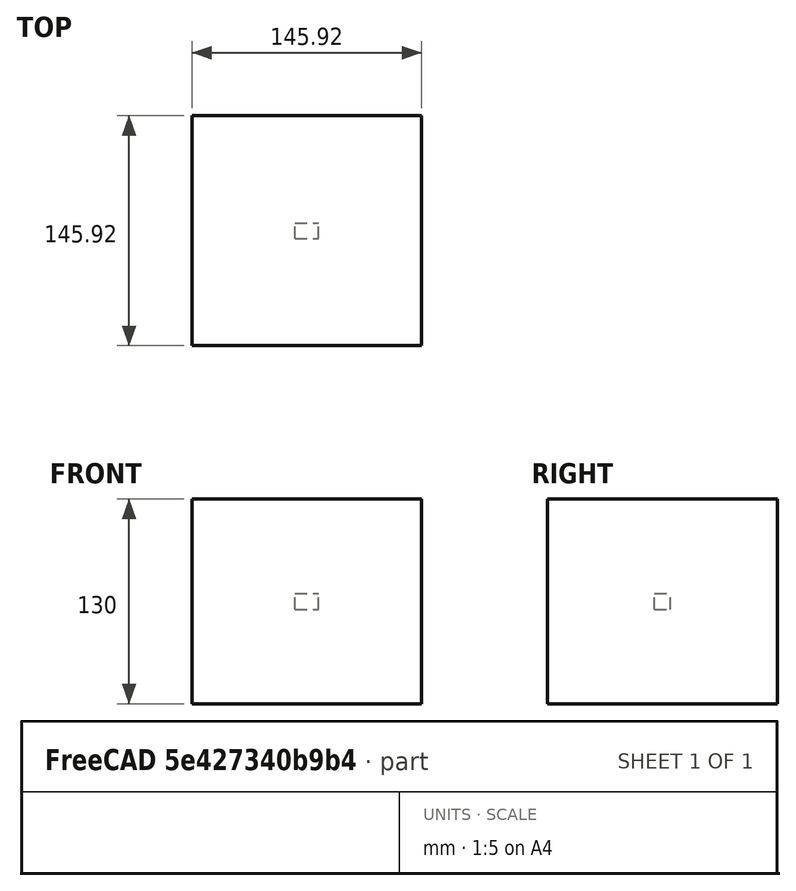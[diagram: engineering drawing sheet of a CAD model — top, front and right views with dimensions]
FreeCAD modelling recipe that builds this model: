
FCSTD DOCUMENT  (FreeCAD 0.20RUnknown)
Label: array-rotation-test
License: All rights reserved
objects: App::DocumentObjectGroupPython×1251, Part::FeaturePython×3, App::Part×3
note: 2 computed .brp shape members not serialized (recipe doc carries the construction recipe); baked Part::Feature solids carry a one-line shape summary decoded from their .brp

FEATURE [App::DocumentObjectGroupPython] HALFPI  # scripted group (container) (typed FeaturePython)
  name = HALFPI
  value = pi/2.
FEATURE [App::DocumentObjectGroupPython] PI  # scripted group (container) (typed FeaturePython)
  name = PI
  value = 1.*pi
FEATURE [App::DocumentObjectGroupPython] TWOPI  # scripted group (container) (typed FeaturePython)
  name = TWOPI
  value = 2.*pi
FEATURE [App::DocumentObjectGroupPython] Constants  # scripted group (container) (typed FeaturePython)
  Group = -> [HALFPI,PI,TWOPI]
FEATURE [App::DocumentObjectGroupPython] Variables  # scripted group (container) (typed FeaturePython)
FEATURE [App::DocumentObjectGroupPython] Quantities  # scripted group (container) (typed FeaturePython)
FEATURE [App::DocumentObjectGroupPython] Isotopes  # scripted group (container) (typed FeaturePython)
FEATURE [App::DocumentObjectGroupPython] Elements  # scripted group (container) (typed FeaturePython)
FEATURE [App::DocumentObjectGroupPython] Matrix  # scripted group (container) (typed FeaturePython)
FEATURE [App::DocumentObjectGroupPython] Surfaces  # scripted group (container) (typed FeaturePython)
FEATURE [App::DocumentObjectGroupPython] Opticals  # scripted group (container) (typed FeaturePython)
  Group = -> [Matrix,Surfaces]
FEATURE [App::DocumentObjectGroupPython] G4Isotopes  # scripted group (container) (typed FeaturePython)
FEATURE [App::DocumentObjectGroupPython] H_element  # scripted group (container) (typed FeaturePython)
  Z = 1
  atom_value = 1.008
  formula = H
  name = H_element
FEATURE [App::DocumentObjectGroupPython] He_element  # scripted group (container) (typed FeaturePython)
  Z = 2
  atom_value = 4.0026
  formula = He
  name = He_element
FEATURE [App::DocumentObjectGroupPython] Li_element  # scripted group (container) (typed FeaturePython)
  Z = 3
  atom_value = 6.94
  formula = Li
  name = Li_element
FEATURE [App::DocumentObjectGroupPython] Be_element  # scripted group (container) (typed FeaturePython)
  Z = 4
  atom_value = 9.01218
  formula = Be
  name = Be_element
FEATURE [App::DocumentObjectGroupPython] B_element  # scripted group (container) (typed FeaturePython)
  Z = 5
  atom_value = 10.81
  formula = B
  name = B_element
FEATURE [App::DocumentObjectGroupPython] C_element  # scripted group (container) (typed FeaturePython)
  Z = 6
  atom_value = 12.011
  formula = C
  name = C_element
FEATURE [App::DocumentObjectGroupPython] N_element  # scripted group (container) (typed FeaturePython)
  Z = 7
  atom_value = 14.007
  formula = N
  name = N_element
FEATURE [App::DocumentObjectGroupPython] O_element  # scripted group (container) (typed FeaturePython)
  Z = 8
  atom_value = 15.999
  formula = O
  name = O_element
FEATURE [App::DocumentObjectGroupPython] F_element  # scripted group (container) (typed FeaturePython)
  Z = 9
  atom_value = 18.9984
  formula = F
  name = F_element
FEATURE [App::DocumentObjectGroupPython] Ne_element  # scripted group (container) (typed FeaturePython)
  Z = 10
  atom_value = 20.1797
  formula = Ne
  name = Ne_element
FEATURE [App::DocumentObjectGroupPython] Na_element  # scripted group (container) (typed FeaturePython)
  Z = 11
  atom_value = 22.9898
  formula = Na
  name = Na_element
FEATURE [App::DocumentObjectGroupPython] Mg_element  # scripted group (container) (typed FeaturePython)
  Z = 12
  atom_value = 24.305
  formula = Mg
  name = Mg_element
FEATURE [App::DocumentObjectGroupPython] Al_element  # scripted group (container) (typed FeaturePython)
  Z = 13
  atom_value = 26.9815
  formula = Al
  name = Al_element
FEATURE [App::DocumentObjectGroupPython] Si_element  # scripted group (container) (typed FeaturePython)
  Z = 14
  atom_value = 28.085
  formula = Si
  name = Si_element
FEATURE [App::DocumentObjectGroupPython] P_element  # scripted group (container) (typed FeaturePython)
  Z = 15
  atom_value = 30.9738
  formula = P
  name = P_element
FEATURE [App::DocumentObjectGroupPython] S_element  # scripted group (container) (typed FeaturePython)
  Z = 16
  atom_value = 32.06
  formula = S
  name = S_element
FEATURE [App::DocumentObjectGroupPython] Cl_element  # scripted group (container) (typed FeaturePython)
  Z = 17
  atom_value = 35.45
  formula = Cl
  name = Cl_element
FEATURE [App::DocumentObjectGroupPython] Ar_element  # scripted group (container) (typed FeaturePython)
  Z = 18
  atom_value = 39.95
  formula = Ar
  name = Ar_element
FEATURE [App::DocumentObjectGroupPython] K_element  # scripted group (container) (typed FeaturePython)
  Z = 19
  atom_value = 39.0983
  formula = K
  name = K_element
FEATURE [App::DocumentObjectGroupPython] Ca_element  # scripted group (container) (typed FeaturePython)
  Z = 20
  atom_value = 40.078
  formula = Ca
  name = Ca_element
FEATURE [App::DocumentObjectGroupPython] Sc_element  # scripted group (container) (typed FeaturePython)
  Z = 21
  atom_value = 44.9559
  formula = Sc
  name = Sc_element
FEATURE [App::DocumentObjectGroupPython] Ti_element  # scripted group (container) (typed FeaturePython)
  Z = 22
  atom_value = 47.867
  formula = Ti
  name = Ti_element
FEATURE [App::DocumentObjectGroupPython] V_element  # scripted group (container) (typed FeaturePython)
  Z = 23
  atom_value = 50.9415
  formula = V
  name = V_element
FEATURE [App::DocumentObjectGroupPython] Cr_element  # scripted group (container) (typed FeaturePython)
  Z = 24
  atom_value = 51.9961
  formula = Cr
  name = Cr_element
FEATURE [App::DocumentObjectGroupPython] Mn_element  # scripted group (container) (typed FeaturePython)
  Z = 25
  atom_value = 54.938
  formula = Mn
  name = Mn_element
FEATURE [App::DocumentObjectGroupPython] Fe_element  # scripted group (container) (typed FeaturePython)
  Z = 26
  atom_value = 55.845
  formula = Fe
  name = Fe_element
FEATURE [App::DocumentObjectGroupPython] Co_element  # scripted group (container) (typed FeaturePython)
  Z = 27
  atom_value = 58.9332
  formula = Co
  name = Co_element
FEATURE [App::DocumentObjectGroupPython] Ni_element  # scripted group (container) (typed FeaturePython)
  Z = 28
  atom_value = 58.6934
  formula = Ni
  name = Ni_element
FEATURE [App::DocumentObjectGroupPython] Cu_element  # scripted group (container) (typed FeaturePython)
  Z = 29
  atom_value = 63.546
  formula = Cu
  name = Cu_element
FEATURE [App::DocumentObjectGroupPython] Zn_element  # scripted group (container) (typed FeaturePython)
  Z = 30
  atom_value = 65.38
  formula = Zn
  name = Zn_element
FEATURE [App::DocumentObjectGroupPython] Ga_element  # scripted group (container) (typed FeaturePython)
  Z = 31
  atom_value = 69.723
  formula = Ga
  name = Ga_element
FEATURE [App::DocumentObjectGroupPython] Ge_element  # scripted group (container) (typed FeaturePython)
  Z = 32
  atom_value = 72.63
  formula = Ge
  name = Ge_element
FEATURE [App::DocumentObjectGroupPython] As_element  # scripted group (container) (typed FeaturePython)
  Z = 33
  atom_value = 74.9216
  formula = As
  name = As_element
FEATURE [App::DocumentObjectGroupPython] Se_element  # scripted group (container) (typed FeaturePython)
  Z = 34
  atom_value = 78.971
  formula = Se
  name = Se_element
FEATURE [App::DocumentObjectGroupPython] Br_element  # scripted group (container) (typed FeaturePython)
  Z = 35
  atom_value = 79.904
  formula = Br
  name = Br_element
FEATURE [App::DocumentObjectGroupPython] Kr_element  # scripted group (container) (typed FeaturePython)
  Z = 36
  atom_value = 83.798
  formula = Kr
  name = Kr_element
FEATURE [App::DocumentObjectGroupPython] Rb_element  # scripted group (container) (typed FeaturePython)
  Z = 37
  atom_value = 85.4678
  formula = Rb
  name = Rb_element
FEATURE [App::DocumentObjectGroupPython] Sr_element  # scripted group (container) (typed FeaturePython)
  Z = 38
  atom_value = 87.62
  formula = Sr
  name = Sr_element
FEATURE [App::DocumentObjectGroupPython] Y_element  # scripted group (container) (typed FeaturePython)
  Z = 39
  atom_value = 88.9058
  formula = Y
  name = Y_element
FEATURE [App::DocumentObjectGroupPython] Zr_element  # scripted group (container) (typed FeaturePython)
  Z = 40
  atom_value = 91.224
  formula = Zr
  name = Zr_element
FEATURE [App::DocumentObjectGroupPython] Nb_element  # scripted group (container) (typed FeaturePython)
  Z = 41
  atom_value = 92.9064
  formula = Nb
  name = Nb_element
FEATURE [App::DocumentObjectGroupPython] Mo_element  # scripted group (container) (typed FeaturePython)
  Z = 42
  atom_value = 95.95
  formula = Mo
  name = Mo_element
FEATURE [App::DocumentObjectGroupPython] Tc_element  # scripted group (container) (typed FeaturePython)
  Z = 43
  atom_value = 97
  formula = Tc
  name = Tc_element
FEATURE [App::DocumentObjectGroupPython] Ru_element  # scripted group (container) (typed FeaturePython)
  Z = 44
  atom_value = 101.07
  formula = Ru
  name = Ru_element
FEATURE [App::DocumentObjectGroupPython] Rh_element  # scripted group (container) (typed FeaturePython)
  Z = 45
  atom_value = 102.905
  formula = Rh
  name = Rh_element
FEATURE [App::DocumentObjectGroupPython] Pd_element  # scripted group (container) (typed FeaturePython)
  Z = 46
  atom_value = 106.42
  formula = Pd
  name = Pd_element
FEATURE [App::DocumentObjectGroupPython] Ag_element  # scripted group (container) (typed FeaturePython)
  Z = 47
  atom_value = 107.868
  formula = Ag
  name = Ag_element
FEATURE [App::DocumentObjectGroupPython] Cd_element  # scripted group (container) (typed FeaturePython)
  Z = 48
  atom_value = 112.414
  formula = Cd
  name = Cd_element
FEATURE [App::DocumentObjectGroupPython] In_element  # scripted group (container) (typed FeaturePython)
  Z = 49
  atom_value = 114.818
  formula = In
  name = In_element
FEATURE [App::DocumentObjectGroupPython] Sn_element  # scripted group (container) (typed FeaturePython)
  Z = 50
  atom_value = 118.71
  formula = Sn
  name = Sn_element
FEATURE [App::DocumentObjectGroupPython] Sb_element  # scripted group (container) (typed FeaturePython)
  Z = 51
  atom_value = 121.76
  formula = Sb
  name = Sb_element
FEATURE [App::DocumentObjectGroupPython] Te_element  # scripted group (container) (typed FeaturePython)
  Z = 52
  atom_value = 127.6
  formula = Te
  name = Te_element
FEATURE [App::DocumentObjectGroupPython] I_element  # scripted group (container) (typed FeaturePython)
  Z = 53
  atom_value = 126.904
  formula = I
  name = I_element
FEATURE [App::DocumentObjectGroupPython] Xe_element  # scripted group (container) (typed FeaturePython)
  Z = 54
  atom_value = 131.293
  formula = Xe
  name = Xe_element
FEATURE [App::DocumentObjectGroupPython] Cs_element  # scripted group (container) (typed FeaturePython)
  Z = 55
  atom_value = 132.905
  formula = Cs
  name = Cs_element
FEATURE [App::DocumentObjectGroupPython] Ba_element  # scripted group (container) (typed FeaturePython)
  Z = 56
  atom_value = 137.327
  formula = Ba
  name = Ba_element
FEATURE [App::DocumentObjectGroupPython] La_element  # scripted group (container) (typed FeaturePython)
  Z = 57
  atom_value = 138.905
  formula = La
  name = La_element
FEATURE [App::DocumentObjectGroupPython] Ce_element  # scripted group (container) (typed FeaturePython)
  Z = 58
  atom_value = 140.116
  formula = Ce
  name = Ce_element
FEATURE [App::DocumentObjectGroupPython] Pr_element  # scripted group (container) (typed FeaturePython)
  Z = 59
  atom_value = 140.908
  formula = Pr
  name = Pr_element
FEATURE [App::DocumentObjectGroupPython] Nd_element  # scripted group (container) (typed FeaturePython)
  Z = 60
  atom_value = 144.242
  formula = Nd
  name = Nd_element
FEATURE [App::DocumentObjectGroupPython] Pm_element  # scripted group (container) (typed FeaturePython)
  Z = 61
  atom_value = 145
  formula = Pm
  name = Pm_element
FEATURE [App::DocumentObjectGroupPython] Sm_element  # scripted group (container) (typed FeaturePython)
  Z = 62
  atom_value = 150.36
  formula = Sm
  name = Sm_element
FEATURE [App::DocumentObjectGroupPython] Eu_element  # scripted group (container) (typed FeaturePython)
  Z = 63
  atom_value = 151.964
  formula = Eu
  name = Eu_element
FEATURE [App::DocumentObjectGroupPython] Gd_element  # scripted group (container) (typed FeaturePython)
  Z = 64
  atom_value = 157.25
  formula = Gd
  name = Gd_element
FEATURE [App::DocumentObjectGroupPython] Tb_element  # scripted group (container) (typed FeaturePython)
  Z = 65
  atom_value = 158.925
  formula = Tb
  name = Tb_element
FEATURE [App::DocumentObjectGroupPython] Dy_element  # scripted group (container) (typed FeaturePython)
  Z = 66
  atom_value = 162.5
  formula = Dy
  name = Dy_element
FEATURE [App::DocumentObjectGroupPython] Ho_element  # scripted group (container) (typed FeaturePython)
  Z = 67
  atom_value = 164.93
  formula = Ho
  name = Ho_element
FEATURE [App::DocumentObjectGroupPython] Er_element  # scripted group (container) (typed FeaturePython)
  Z = 68
  atom_value = 167.259
  formula = Er
  name = Er_element
FEATURE [App::DocumentObjectGroupPython] Tm_element  # scripted group (container) (typed FeaturePython)
  Z = 69
  atom_value = 168.934
  formula = Tm
  name = Tm_element
FEATURE [App::DocumentObjectGroupPython] Yb_element  # scripted group (container) (typed FeaturePython)
  Z = 70
  atom_value = 173.045
  formula = Yb
  name = Yb_element
FEATURE [App::DocumentObjectGroupPython] Lu_element  # scripted group (container) (typed FeaturePython)
  Z = 71
  atom_value = 174.967
  formula = Lu
  name = Lu_element
FEATURE [App::DocumentObjectGroupPython] Hf_element  # scripted group (container) (typed FeaturePython)
  Z = 72
  atom_value = 178.49
  formula = Hf
  name = Hf_element
FEATURE [App::DocumentObjectGroupPython] Ta_element  # scripted group (container) (typed FeaturePython)
  Z = 73
  atom_value = 180.948
  formula = Ta
  name = Ta_element
FEATURE [App::DocumentObjectGroupPython] W_element  # scripted group (container) (typed FeaturePython)
  Z = 74
  atom_value = 183.84
  formula = W
  name = W_element
FEATURE [App::DocumentObjectGroupPython] Re_element  # scripted group (container) (typed FeaturePython)
  Z = 75
  atom_value = 186.207
  formula = Re
  name = Re_element
FEATURE [App::DocumentObjectGroupPython] Os_element  # scripted group (container) (typed FeaturePython)
  Z = 76
  atom_value = 190.23
  formula = Os
  name = Os_element
FEATURE [App::DocumentObjectGroupPython] Ir_element  # scripted group (container) (typed FeaturePython)
  Z = 77
  atom_value = 192.217
  formula = Ir
  name = Ir_element
FEATURE [App::DocumentObjectGroupPython] Pt_element  # scripted group (container) (typed FeaturePython)
  Z = 78
  atom_value = 195.084
  formula = Pt
  name = Pt_element
FEATURE [App::DocumentObjectGroupPython] Au_element  # scripted group (container) (typed FeaturePython)
  Z = 79
  atom_value = 196.967
  formula = Au
  name = Au_element
FEATURE [App::DocumentObjectGroupPython] Hg_element  # scripted group (container) (typed FeaturePython)
  Z = 80
  atom_value = 200.592
  formula = Hg
  name = Hg_element
FEATURE [App::DocumentObjectGroupPython] Tl_element  # scripted group (container) (typed FeaturePython)
  Z = 81
  atom_value = 204.38
  formula = Tl
  name = Tl_element
FEATURE [App::DocumentObjectGroupPython] Pb_element  # scripted group (container) (typed FeaturePython)
  Z = 82
  atom_value = 207.2
  formula = Pb
  name = Pb_element
FEATURE [App::DocumentObjectGroupPython] Bi_element  # scripted group (container) (typed FeaturePython)
  Z = 83
  atom_value = 208.98
  formula = Bi
  name = Bi_element
FEATURE [App::DocumentObjectGroupPython] Po_element  # scripted group (container) (typed FeaturePython)
  Z = 84
  atom_value = 209
  formula = Po
  name = Po_element
FEATURE [App::DocumentObjectGroupPython] At_element  # scripted group (container) (typed FeaturePython)
  Z = 85
  atom_value = 210
  formula = At
  name = At_element
FEATURE [App::DocumentObjectGroupPython] Rn_element  # scripted group (container) (typed FeaturePython)
  Z = 86
  atom_value = 222
  formula = Rn
  name = Rn_element
FEATURE [App::DocumentObjectGroupPython] Fr_element  # scripted group (container) (typed FeaturePython)
  Z = 87
  atom_value = 223
  formula = Fr
  name = Fr_element
FEATURE [App::DocumentObjectGroupPython] Ra_element  # scripted group (container) (typed FeaturePython)
  Z = 88
  atom_value = 226
  formula = Ra
  name = Ra_element
FEATURE [App::DocumentObjectGroupPython] Ac_element  # scripted group (container) (typed FeaturePython)
  Z = 89
  atom_value = 227
  formula = Ac
  name = Ac_element
FEATURE [App::DocumentObjectGroupPython] Th_element  # scripted group (container) (typed FeaturePython)
  Z = 90
  atom_value = 232.038
  formula = Th
  name = Th_element
FEATURE [App::DocumentObjectGroupPython] Pa_element  # scripted group (container) (typed FeaturePython)
  Z = 91
  atom_value = 231.036
  formula = Pa
  name = Pa_element
FEATURE [App::DocumentObjectGroupPython] U_element  # scripted group (container) (typed FeaturePython)
  Z = 92
  atom_value = 238.029
  formula = U
  name = U_element
FEATURE [App::DocumentObjectGroupPython] Np_element  # scripted group (container) (typed FeaturePython)
  Z = 93
  atom_value = 237
  formula = Np
  name = Np_element
FEATURE [App::DocumentObjectGroupPython] Pu_element  # scripted group (container) (typed FeaturePython)
  Z = 94
  atom_value = 244
  formula = Pu
  name = Pu_element
FEATURE [App::DocumentObjectGroupPython] Am_element  # scripted group (container) (typed FeaturePython)
  Z = 95
  atom_value = 243
  formula = Am
  name = Am_element
FEATURE [App::DocumentObjectGroupPython] Cm_element  # scripted group (container) (typed FeaturePython)
  Z = 96
  atom_value = 247
  formula = Cm
  name = Cm_element
FEATURE [App::DocumentObjectGroupPython] Bk_element  # scripted group (container) (typed FeaturePython)
  Z = 97
  atom_value = 247
  formula = Bk
  name = Bk_element
FEATURE [App::DocumentObjectGroupPython] Cf_element  # scripted group (container) (typed FeaturePython)
  Z = 98
  atom_value = 251
  formula = Cf
  name = Cf_element
FEATURE [App::DocumentObjectGroupPython] G4Elements  # scripted group (container) (typed FeaturePython)
  Group = -> [H_element,He_element,Li_element,Be_element,B_element,C_element,N_element,O_element,F_element,Ne_element,Na_element,Mg_element,Al_element,Si_element,P_element,S_element,Cl_element,Ar_element,K_element,Ca_element,Sc_element,Ti_element,V_element,Cr_element,Mn_element,Fe_element,Co_element,Ni_element,Cu_element,Zn_element,Ga_element,Ge_element,As_element,Se_element,Br_element,Kr_element,Rb_element,+61 more]
FEATURE [App::DocumentObjectGroupPython] H_element001  label="H_element : 0.101"  # scripted group (container) (typed FeaturePython)
  n = 0.101327
FEATURE [App::DocumentObjectGroupPython] C_element001  label="C_element : 0.775"  # scripted group (container) (typed FeaturePython)
  n = 0.7755
FEATURE [App::DocumentObjectGroupPython] N_element001  label="N_element : 0.035"  # scripted group (container) (typed FeaturePython)
  n = 0.035057
FEATURE [App::DocumentObjectGroupPython] O_element001  label="O_element : 0.052"  # scripted group (container) (typed FeaturePython)
  n = 0.0523159
FEATURE [App::DocumentObjectGroupPython] F_element001  label="F_element : 0.017"  # scripted group (container) (typed FeaturePython)
  n = 0.017422
FEATURE [App::DocumentObjectGroupPython] Ca_element001  label="Ca_element : 0.018"  # scripted group (container) (typed FeaturePython)
  n = 0.018378
FEATURE [App::DocumentObjectGroupPython] G4_A_150_TISSUE  label="G4_A-150_TISSUE"  # scripted group (container) (typed FeaturePython)
  Dunit = g/cm3
  Dvalue = 1.127
  Group = -> [H_element001,C_element001,N_element001,O_element001,F_element001,Ca_element001]
  conduct = 2
  density = 1
  expand = 3
  formula = G4_A-150_TISSUE
  name = G4_A-150_TISSUE
  specific = 4
FEATURE [App::DocumentObjectGroupPython] C_element002  label="C_element : 3"  # scripted group (container) (typed FeaturePython)
  n = 3
  ref = C_element
FEATURE [App::DocumentObjectGroupPython] H_element002  label="H_element : 6"  # scripted group (container) (typed FeaturePython)
  n = 6
  ref = H_element
FEATURE [App::DocumentObjectGroupPython] O_element002  label="O_element : 1"  # scripted group (container) (typed FeaturePython)
  n = 1
  ref = O_element
FEATURE [App::DocumentObjectGroupPython] G4_ACETONE  # scripted group (container) (typed FeaturePython)
  Dunit = g/cm3
  Dvalue = 0.7899
  Group = -> [C_element002,H_element002,O_element002]
  conduct = 2
  density = 1
  expand = 3
  formula = G4_ACETONE
  name = G4_ACETONE
  specific = 4
FEATURE [App::DocumentObjectGroupPython] C_element003  label="C_element : 2"  # scripted group (container) (typed FeaturePython)
  n = 2
  ref = C_element
FEATURE [App::DocumentObjectGroupPython] H_element003  label="H_element : 2"  # scripted group (container) (typed FeaturePython)
  n = 2
  ref = H_element
FEATURE [App::DocumentObjectGroupPython] G4_ACETYLENE  # scripted group (container) (typed FeaturePython)
  Dunit = g/cm3
  Dvalue = 0.0010967
  Group = -> [C_element003,H_element003]
  conduct = 2
  density = 1
  expand = 3
  formula = G4_ACETYLENE
  name = G4_ACETYLENE
  specific = 4
FEATURE [App::DocumentObjectGroupPython] C_element004  label="C_element : 5"  # scripted group (container) (typed FeaturePython)
  n = 5
  ref = C_element
FEATURE [App::DocumentObjectGroupPython] H_element004  label="H_element : 5"  # scripted group (container) (typed FeaturePython)
  n = 5
  ref = H_element
FEATURE [App::DocumentObjectGroupPython] N_element002  label="N_element : 5"  # scripted group (container) (typed FeaturePython)
  n = 5
  ref = N_element
FEATURE [App::DocumentObjectGroupPython] G4_ADENINE  # scripted group (container) (typed FeaturePython)
  Dunit = g/cm3
  Dvalue = 1.6
  Group = -> [C_element004,H_element004,N_element002]
  conduct = 2
  density = 1
  expand = 3
  formula = G4_ADENINE
  name = G4_ADENINE
  specific = 4
FEATURE [App::DocumentObjectGroupPython] H_element005  label="H_element : 0.114"  # scripted group (container) (typed FeaturePython)
  n = 0.114
FEATURE [App::DocumentObjectGroupPython] C_element005  label="C_element : 0.598"  # scripted group (container) (typed FeaturePython)
  n = 0.598
FEATURE [App::DocumentObjectGroupPython] N_element003  label="N_element : 0.007"  # scripted group (container) (typed FeaturePython)
  n = 0.007
FEATURE [App::DocumentObjectGroupPython] O_element003  label="O_element : 0.278"  # scripted group (container) (typed FeaturePython)
  n = 0.278
FEATURE [App::DocumentObjectGroupPython] Na_element001  label="Na_element : 0.001"  # scripted group (container) (typed FeaturePython)
  n = 0.001
FEATURE [App::DocumentObjectGroupPython] S_element001  label="S_element : 0.001"  # scripted group (container) (typed FeaturePython)
  n = 0.001
FEATURE [App::DocumentObjectGroupPython] Cl_element001  label="Cl_element : 0.001"  # scripted group (container) (typed FeaturePython)
  n = 0.001
FEATURE [App::DocumentObjectGroupPython] G4_ADIPOSE_TISSUE_ICRP  # scripted group (container) (typed FeaturePython)
  Dunit = g/cm3
  Dvalue = 0.95
  Group = -> [H_element005,C_element005,N_element003,O_element003,Na_element001,S_element001,Cl_element001]
  conduct = 2
  density = 1
  expand = 3
  formula = G4_ADIPOSE_TISSUE_ICRP
  name = G4_ADIPOSE_TISSUE_ICRP
  specific = 4
FEATURE [App::DocumentObjectGroupPython] C_element006  label="C_element : 0.000"  # scripted group (container) (typed FeaturePython)
  n = 0.000124
FEATURE [App::DocumentObjectGroupPython] N_element004  label="N_element : 0.755"  # scripted group (container) (typed FeaturePython)
  n = 0.755268
FEATURE [App::DocumentObjectGroupPython] O_element004  label="O_element : 0.232"  # scripted group (container) (typed FeaturePython)
  n = 0.231781
FEATURE [App::DocumentObjectGroupPython] Ar_element001  label="Ar_element : 0.013"  # scripted group (container) (typed FeaturePython)
  n = 0.012827
FEATURE [App::DocumentObjectGroupPython] G4_AIR  # scripted group (container) (typed FeaturePython)
  Dunit = g/cm3
  Dvalue = 0.00120479
  Group = -> [C_element006,N_element004,O_element004,Ar_element001]
  conduct = 2
  density = 1
  expand = 3
  formula = G4_AIR
  name = G4_AIR
  specific = 4
FEATURE [App::DocumentObjectGroupPython] C_element007  label="C_element : 006"  # scripted group (container) (typed FeaturePython)
  n = 3
  ref = C_element
FEATURE [App::DocumentObjectGroupPython] H_element006  label="H_element : 7"  # scripted group (container) (typed FeaturePython)
  n = 7
  ref = H_element
FEATURE [App::DocumentObjectGroupPython] N_element005  label="N_element : 1"  # scripted group (container) (typed FeaturePython)
  n = 1
  ref = N_element
FEATURE [App::DocumentObjectGroupPython] O_element005  label="O_element : 2"  # scripted group (container) (typed FeaturePython)
  n = 2
  ref = O_element
FEATURE [App::DocumentObjectGroupPython] G4_ALANINE  # scripted group (container) (typed FeaturePython)
  Dunit = g/cm3
  Dvalue = 1.42
  Group = -> [C_element007,H_element006,N_element005,O_element005]
  conduct = 2
  density = 1
  expand = 3
  formula = G4_ALANINE
  name = G4_ALANINE
  specific = 4
FEATURE [App::DocumentObjectGroupPython] Al_element001  label="Al_element : 2"  # scripted group (container) (typed FeaturePython)
  n = 2
  ref = Al_element
FEATURE [App::DocumentObjectGroupPython] O_element006  label="O_element : 3"  # scripted group (container) (typed FeaturePython)
  n = 3
  ref = O_element
FEATURE [App::DocumentObjectGroupPython] G4_ALUMINUM_OXIDE  # scripted group (container) (typed FeaturePython)
  Dunit = g/cm3
  Dvalue = 3.97
  Group = -> [Al_element001,O_element006]
  conduct = 2
  density = 1
  expand = 3
  formula = G4_ALUMINUM_OXIDE
  name = G4_ALUMINUM_OXIDE
  specific = 4
FEATURE [App::DocumentObjectGroupPython] H_element007  label="H_element : 0.106"  # scripted group (container) (typed FeaturePython)
  n = 0.10593
FEATURE [App::DocumentObjectGroupPython] C_element008  label="C_element : 0.789"  # scripted group (container) (typed FeaturePython)
  n = 0.788974
FEATURE [App::DocumentObjectGroupPython] O_element007  label="O_element : 0.105"  # scripted group (container) (typed FeaturePython)
  n = 0.105096
FEATURE [App::DocumentObjectGroupPython] G4_AMBER  # scripted group (container) (typed FeaturePython)
  Dunit = g/cm3
  Dvalue = 1.1
  Group = -> [H_element007,C_element008,O_element007]
  conduct = 2
  density = 1
  expand = 3
  formula = G4_AMBER
  name = G4_AMBER
  specific = 4
FEATURE [App::DocumentObjectGroupPython] N_element006  label="N_element : 006"  # scripted group (container) (typed FeaturePython)
  n = 1
  ref = N_element
FEATURE [App::DocumentObjectGroupPython] H_element008  label="H_element : 3"  # scripted group (container) (typed FeaturePython)
  n = 3
  ref = H_element
FEATURE [App::DocumentObjectGroupPython] G4_AMMONIA  # scripted group (container) (typed FeaturePython)
  Dunit = g/cm3
  Dvalue = 0.000826019
  Group = -> [N_element006,H_element008]
  conduct = 2
  density = 1
  expand = 3
  formula = G4_AMMONIA
  name = G4_AMMONIA
  specific = 4
FEATURE [App::DocumentObjectGroupPython] C_element009  label="C_element : 6"  # scripted group (container) (typed FeaturePython)
  n = 6
  ref = C_element
FEATURE [App::DocumentObjectGroupPython] H_element009  label="H_element : 008"  # scripted group (container) (typed FeaturePython)
  n = 7
  ref = H_element
FEATURE [App::DocumentObjectGroupPython] N_element007  label="N_element : 007"  # scripted group (container) (typed FeaturePython)
  n = 1
  ref = N_element
FEATURE [App::DocumentObjectGroupPython] G4_ANILINE  # scripted group (container) (typed FeaturePython)
  Dunit = g/cm3
  Dvalue = 1.0235
  Group = -> [C_element009,H_element009,N_element007]
  conduct = 2
  density = 1
  expand = 3
  formula = G4_ANILINE
  name = G4_ANILINE
  specific = 4
FEATURE [App::DocumentObjectGroupPython] C_element010  label="C_element : 14"  # scripted group (container) (typed FeaturePython)
  n = 14
  ref = C_element
FEATURE [App::DocumentObjectGroupPython] H_element010  label="H_element : 10"  # scripted group (container) (typed FeaturePython)
  n = 10
  ref = H_element
FEATURE [App::DocumentObjectGroupPython] G4_ANTHRACENE  # scripted group (container) (typed FeaturePython)
  Dunit = g/cm3
  Dvalue = 1.283
  Group = -> [C_element010,H_element010]
  conduct = 2
  density = 1
  expand = 3
  formula = G4_ANTHRACENE
  name = G4_ANTHRACENE
  specific = 4
FEATURE [App::DocumentObjectGroupPython] H_element011  label="H_element : 0.065"  # scripted group (container) (typed FeaturePython)
  n = 0.0654709
FEATURE [App::DocumentObjectGroupPython] C_element011  label="C_element : 0.537"  # scripted group (container) (typed FeaturePython)
  n = 0.536944
FEATURE [App::DocumentObjectGroupPython] N_element008  label="N_element : 0.021"  # scripted group (container) (typed FeaturePython)
  n = 0.0215
FEATURE [App::DocumentObjectGroupPython] O_element008  label="O_element : 0.032"  # scripted group (container) (typed FeaturePython)
  n = 0.032085
FEATURE [App::DocumentObjectGroupPython] F_element002  label="F_element : 0.167"  # scripted group (container) (typed FeaturePython)
  n = 0.167411
FEATURE [App::DocumentObjectGroupPython] Ca_element002  label="Ca_element : 0.177"  # scripted group (container) (typed FeaturePython)
  n = 0.176589
FEATURE [App::DocumentObjectGroupPython] G4_B_100_BONE  label="G4_B-100_BONE"  # scripted group (container) (typed FeaturePython)
  Dunit = g/cm3
  Dvalue = 1.45
  Group = -> [H_element011,C_element011,N_element008,O_element008,F_element002,Ca_element002]
  conduct = 2
  density = 1
  expand = 3
  formula = G4_B-100_BONE
  name = G4_B-100_BONE
  specific = 4
FEATURE [App::DocumentObjectGroupPython] H_element012  label="H_element : 0.057"  # scripted group (container) (typed FeaturePython)
  n = 0.057441
FEATURE [App::DocumentObjectGroupPython] C_element012  label="C_element : 0.790"  # scripted group (container) (typed FeaturePython)
  n = 0.774591
FEATURE [App::DocumentObjectGroupPython] O_element009  label="O_element : 0.168"  # scripted group (container) (typed FeaturePython)
  n = 0.167968
FEATURE [App::DocumentObjectGroupPython] G4_BAKELITE  # scripted group (container) (typed FeaturePython)
  Dunit = g/cm3
  Dvalue = 1.25
  Group = -> [H_element012,C_element012,O_element009]
  conduct = 2
  density = 1
  expand = 3
  formula = G4_BAKELITE
  name = G4_BAKELITE
  specific = 4
FEATURE [App::DocumentObjectGroupPython] Ba_element001  label="Ba_element : 1"  # scripted group (container) (typed FeaturePython)
  n = 1
  ref = Ba_element
FEATURE [App::DocumentObjectGroupPython] F_element003  label="F_element : 2"  # scripted group (container) (typed FeaturePython)
  n = 2
  ref = F_element
FEATURE [App::DocumentObjectGroupPython] G4_BARIUM_FLUORIDE  # scripted group (container) (typed FeaturePython)
  Dunit = g/cm3
  Dvalue = 4.89
  Group = -> [Ba_element001,F_element003]
  conduct = 2
  density = 1
  expand = 3
  formula = G4_BARIUM_FLUORIDE
  name = G4_BARIUM_FLUORIDE
  specific = 4
FEATURE [App::DocumentObjectGroupPython] Ba_element002  label="Ba_element : 002"  # scripted group (container) (typed FeaturePython)
  n = 1
  ref = Ba_element
FEATURE [App::DocumentObjectGroupPython] S_element002  label="S_element : 1"  # scripted group (container) (typed FeaturePython)
  n = 1
  ref = S_element
FEATURE [App::DocumentObjectGroupPython] O_element010  label="O_element : 4"  # scripted group (container) (typed FeaturePython)
  n = 4
  ref = O_element
FEATURE [App::DocumentObjectGroupPython] G4_BARIUM_SULFATE  # scripted group (container) (typed FeaturePython)
  Dunit = g/cm3
  Dvalue = 4.5
  Group = -> [Ba_element002,S_element002,O_element010]
  conduct = 2
  density = 1
  expand = 3
  formula = G4_BARIUM_SULFATE
  name = G4_BARIUM_SULFATE
  specific = 4
FEATURE [App::DocumentObjectGroupPython] C_element013  label="C_element : 007"  # scripted group (container) (typed FeaturePython)
  n = 6
  ref = C_element
FEATURE [App::DocumentObjectGroupPython] H_element013  label="H_element : 009"  # scripted group (container) (typed FeaturePython)
  n = 6
  ref = H_element
FEATURE [App::DocumentObjectGroupPython] G4_BENZENE  # scripted group (container) (typed FeaturePython)
  Dunit = g/cm3
  Dvalue = 0.87865
  Group = -> [C_element013,H_element013]
  conduct = 2
  density = 1
  expand = 3
  formula = G4_BENZENE
  name = G4_BENZENE
  specific = 4
FEATURE [App::DocumentObjectGroupPython] Be_element001  label="Be_element : 1"  # scripted group (container) (typed FeaturePython)
  n = 1
  ref = Be_element
FEATURE [App::DocumentObjectGroupPython] O_element011  label="O_element : 005"  # scripted group (container) (typed FeaturePython)
  n = 1
  ref = O_element
FEATURE [App::DocumentObjectGroupPython] G4_BERYLLIUM_OXIDE  # scripted group (container) (typed FeaturePython)
  Dunit = g/cm3
  Dvalue = 3.01
  Group = -> [Be_element001,O_element011]
  conduct = 2
  density = 1
  expand = 3
  formula = G4_BERYLLIUM_OXIDE
  name = G4_BERYLLIUM_OXIDE
  specific = 4
FEATURE [App::DocumentObjectGroupPython] Bi_element001  label="Bi_element : 4"  # scripted group (container) (typed FeaturePython)
  n = 4
  ref = Bi_element
FEATURE [App::DocumentObjectGroupPython] Ge_element001  label="Ge_element : 3"  # scripted group (container) (typed FeaturePython)
  n = 3
  ref = Ge_element
FEATURE [App::DocumentObjectGroupPython] O_element012  label="O_element : 12"  # scripted group (container) (typed FeaturePython)
  n = 12
  ref = O_element
FEATURE [App::DocumentObjectGroupPython] G4_BGO  # scripted group (container) (typed FeaturePython)
  Dunit = g/cm3
  Dvalue = 7.13
  Group = -> [Bi_element001,Ge_element001,O_element012]
  conduct = 2
  density = 1
  expand = 3
  formula = G4_BGO
  name = G4_BGO
  specific = 4
FEATURE [App::DocumentObjectGroupPython] H_element014  label="H_element : 0.102"  # scripted group (container) (typed FeaturePython)
  n = 0.102
FEATURE [App::DocumentObjectGroupPython] C_element014  label="C_element : 0.110"  # scripted group (container) (typed FeaturePython)
  n = 0.11
FEATURE [App::DocumentObjectGroupPython] N_element009  label="N_element : 0.033"  # scripted group (container) (typed FeaturePython)
  n = 0.033
FEATURE [App::DocumentObjectGroupPython] O_element013  label="O_element : 0.745"  # scripted group (container) (typed FeaturePython)
  n = 0.745
FEATURE [App::DocumentObjectGroupPython] Na_element002  label="Na_element : 0.002"  # scripted group (container) (typed FeaturePython)
  n = 0.001
FEATURE [App::DocumentObjectGroupPython] P_element001  label="P_element : 0.001"  # scripted group (container) (typed FeaturePython)
  n = 0.001
FEATURE [App::DocumentObjectGroupPython] S_element003  label="S_element : 0.002"  # scripted group (container) (typed FeaturePython)
  n = 0.002
FEATURE [App::DocumentObjectGroupPython] Cl_element002  label="Cl_element : 0.003"  # scripted group (container) (typed FeaturePython)
  n = 0.003
FEATURE [App::DocumentObjectGroupPython] K_element001  label="K_element : 0.002"  # scripted group (container) (typed FeaturePython)
  n = 0.002
FEATURE [App::DocumentObjectGroupPython] Fe_element001  label="Fe_element : 0.001"  # scripted group (container) (typed FeaturePython)
  n = 0.001
FEATURE [App::DocumentObjectGroupPython] G4_BLOOD_ICRP  # scripted group (container) (typed FeaturePython)
  Dunit = g/cm3
  Dvalue = 1.06
  Group = -> [H_element014,C_element014,N_element009,O_element013,Na_element002,P_element001,S_element003,Cl_element002,K_element001,Fe_element001]
  conduct = 2
  density = 1
  expand = 3
  formula = G4_BLOOD_ICRP
  name = G4_BLOOD_ICRP
  specific = 4
FEATURE [App::DocumentObjectGroupPython] H_element015  label="H_element : 0.064"  # scripted group (container) (typed FeaturePython)
  n = 0.064
FEATURE [App::DocumentObjectGroupPython] C_element015  label="C_element : 0.278"  # scripted group (container) (typed FeaturePython)
  n = 0.278
FEATURE [App::DocumentObjectGroupPython] N_element010  label="N_element : 0.027"  # scripted group (container) (typed FeaturePython)
  n = 0.027
FEATURE [App::DocumentObjectGroupPython] O_element014  label="O_element : 0.410"  # scripted group (container) (typed FeaturePython)
  n = 0.41
FEATURE [App::DocumentObjectGroupPython] Mg_element001  label="Mg_element : 0.002"  # scripted group (container) (typed FeaturePython)
  n = 0.002
FEATURE [App::DocumentObjectGroupPython] P_element002  label="P_element : 0.070"  # scripted group (container) (typed FeaturePython)
  n = 0.07
FEATURE [App::DocumentObjectGroupPython] S_element004  label="S_element : 0.003"  # scripted group (container) (typed FeaturePython)
  n = 0.002
FEATURE [App::DocumentObjectGroupPython] Ca_element003  label="Ca_element : 0.147"  # scripted group (container) (typed FeaturePython)
  n = 0.147
FEATURE [App::DocumentObjectGroupPython] G4_BONE_COMPACT_ICRU  # scripted group (container) (typed FeaturePython)
  Dunit = g/cm3
  Dvalue = 1.85
  Group = -> [H_element015,C_element015,N_element010,O_element014,Mg_element001,P_element002,S_element004,Ca_element003]
  conduct = 2
  density = 1
  expand = 3
  formula = G4_BONE_COMPACT_ICRU
  name = G4_BONE_COMPACT_ICRU
  specific = 4
FEATURE [App::DocumentObjectGroupPython] H_element016  label="H_element : 0.034"  # scripted group (container) (typed FeaturePython)
  n = 0.034
FEATURE [App::DocumentObjectGroupPython] C_element016  label="C_element : 0.155"  # scripted group (container) (typed FeaturePython)
  n = 0.155
FEATURE [App::DocumentObjectGroupPython] N_element011  label="N_element : 0.042"  # scripted group (container) (typed FeaturePython)
  n = 0.042
FEATURE [App::DocumentObjectGroupPython] O_element015  label="O_element : 0.435"  # scripted group (container) (typed FeaturePython)
  n = 0.435
FEATURE [App::DocumentObjectGroupPython] Na_element003  label="Na_element : 0.003"  # scripted group (container) (typed FeaturePython)
  n = 0.001
FEATURE [App::DocumentObjectGroupPython] Mg_element002  label="Mg_element : 0.003"  # scripted group (container) (typed FeaturePython)
  n = 0.002
FEATURE [App::DocumentObjectGroupPython] P_element003  label="P_element : 0.103"  # scripted group (container) (typed FeaturePython)
  n = 0.103
FEATURE [App::DocumentObjectGroupPython] S_element005  label="S_element : 0.004"  # scripted group (container) (typed FeaturePython)
  n = 0.003
FEATURE [App::DocumentObjectGroupPython] Ca_element004  label="Ca_element : 0.225"  # scripted group (container) (typed FeaturePython)
  n = 0.225
FEATURE [App::DocumentObjectGroupPython] G4_BONE_CORTICAL_ICRP  # scripted group (container) (typed FeaturePython)
  Dunit = g/cm3
  Dvalue = 1.92
  Group = -> [H_element016,C_element016,N_element011,O_element015,Na_element003,Mg_element002,P_element003,S_element005,Ca_element004]
  conduct = 2
  density = 1
  expand = 3
  formula = G4_BONE_CORTICAL_ICRP
  name = G4_BONE_CORTICAL_ICRP
  specific = 4
FEATURE [App::DocumentObjectGroupPython] B_element001  label="B_element : 4"  # scripted group (container) (typed FeaturePython)
  n = 4
  ref = B_element
FEATURE [App::DocumentObjectGroupPython] C_element017  label="C_element : 1"  # scripted group (container) (typed FeaturePython)
  n = 1
  ref = C_element
FEATURE [App::DocumentObjectGroupPython] G4_BORON_CARBIDE  # scripted group (container) (typed FeaturePython)
  Dunit = g/cm3
  Dvalue = 2.52
  Group = -> [B_element001,C_element017]
  conduct = 2
  density = 1
  expand = 3
  formula = G4_BORON_CARBIDE
  name = G4_BORON_CARBIDE
  specific = 4
FEATURE [App::DocumentObjectGroupPython] B_element002  label="B_element : 2"  # scripted group (container) (typed FeaturePython)
  n = 2
  ref = B_element
FEATURE [App::DocumentObjectGroupPython] O_element016  label="O_element : 006"  # scripted group (container) (typed FeaturePython)
  n = 3
  ref = O_element
FEATURE [App::DocumentObjectGroupPython] G4_BORON_OXIDE  # scripted group (container) (typed FeaturePython)
  Dunit = g/cm3
  Dvalue = 1.812
  Group = -> [B_element002,O_element016]
  conduct = 2
  density = 1
  expand = 3
  formula = G4_BORON_OXIDE
  name = G4_BORON_OXIDE
  specific = 4
FEATURE [App::DocumentObjectGroupPython] H_element017  label="H_element : 0.107"  # scripted group (container) (typed FeaturePython)
  n = 0.107
FEATURE [App::DocumentObjectGroupPython] C_element018  label="C_element : 0.145"  # scripted group (container) (typed FeaturePython)
  n = 0.145
FEATURE [App::DocumentObjectGroupPython] N_element012  label="N_element : 0.022"  # scripted group (container) (typed FeaturePython)
  n = 0.022
FEATURE [App::DocumentObjectGroupPython] O_element017  label="O_element : 0.712"  # scripted group (container) (typed FeaturePython)
  n = 0.712
FEATURE [App::DocumentObjectGroupPython] Na_element004  label="Na_element : 0.004"  # scripted group (container) (typed FeaturePython)
  n = 0.002
FEATURE [App::DocumentObjectGroupPython] P_element004  label="P_element : 0.004"  # scripted group (container) (typed FeaturePython)
  n = 0.004
FEATURE [App::DocumentObjectGroupPython] S_element006  label="S_element : 0.005"  # scripted group (container) (typed FeaturePython)
  n = 0.002
FEATURE [App::DocumentObjectGroupPython] Cl_element003  label="Cl_element : 0.004"  # scripted group (container) (typed FeaturePython)
  n = 0.003
FEATURE [App::DocumentObjectGroupPython] K_element002  label="K_element : 0.003"  # scripted group (container) (typed FeaturePython)
  n = 0.003
FEATURE [App::DocumentObjectGroupPython] G4_BRAIN_ICRP  # scripted group (container) (typed FeaturePython)
  Dunit = g/cm3
  Dvalue = 1.04
  Group = -> [H_element017,C_element018,N_element012,O_element017,Na_element004,P_element004,S_element006,Cl_element003,K_element002]
  conduct = 2
  density = 1
  expand = 3
  formula = G4_BRAIN_ICRP
  name = G4_BRAIN_ICRP
  specific = 4
FEATURE [App::DocumentObjectGroupPython] C_element019  label="C_element : 4"  # scripted group (container) (typed FeaturePython)
  n = 4
  ref = C_element
FEATURE [App::DocumentObjectGroupPython] H_element018  label="H_element : 010"  # scripted group (container) (typed FeaturePython)
  n = 10
  ref = H_element
FEATURE [App::DocumentObjectGroupPython] G4_BUTANE  # scripted group (container) (typed FeaturePython)
  Dunit = g/cm3
  Dvalue = 0.00249343
  Group = -> [C_element019,H_element018]
  conduct = 2
  density = 1
  expand = 3
  formula = G4_BUTANE
  name = G4_BUTANE
  specific = 4
FEATURE [App::DocumentObjectGroupPython] C_element020  label="C_element : 008"  # scripted group (container) (typed FeaturePython)
  n = 4
  ref = C_element
FEATURE [App::DocumentObjectGroupPython] H_element019  label="H_element : 011"  # scripted group (container) (typed FeaturePython)
  n = 10
  ref = H_element
FEATURE [App::DocumentObjectGroupPython] O_element018  label="O_element : 007"  # scripted group (container) (typed FeaturePython)
  n = 1
  ref = O_element
FEATURE [App::DocumentObjectGroupPython] G4_N_BUTYL_ALCOHOL  label="G4_N-BUTYL_ALCOHOL"  # scripted group (container) (typed FeaturePython)
  Dunit = g/cm3
  Dvalue = 0.8098
  Group = -> [C_element020,H_element019,O_element018]
  conduct = 2
  density = 1
  expand = 3
  formula = G4_N-BUTYL_ALCOHOL
  name = G4_N-BUTYL_ALCOHOL
  specific = 4
FEATURE [App::DocumentObjectGroupPython] H_element020  label="H_element : 0.025"  # scripted group (container) (typed FeaturePython)
  n = 0.02468
FEATURE [App::DocumentObjectGroupPython] C_element021  label="C_element : 0.502"  # scripted group (container) (typed FeaturePython)
  n = 0.501611
FEATURE [App::DocumentObjectGroupPython] O_element019  label="O_element : 0.005"  # scripted group (container) (typed FeaturePython)
  n = 0.004527
FEATURE [App::DocumentObjectGroupPython] F_element004  label="F_element : 0.465"  # scripted group (container) (typed FeaturePython)
  n = 0.465209
FEATURE [App::DocumentObjectGroupPython] Si_element001  label="Si_element : 0.004"  # scripted group (container) (typed FeaturePython)
  n = 0.003973
FEATURE [App::DocumentObjectGroupPython] G4_C_552  label="G4_C-552"  # scripted group (container) (typed FeaturePython)
  Dunit = g/cm3
  Dvalue = 1.76
  Group = -> [H_element020,C_element021,O_element019,F_element004,Si_element001]
  conduct = 2
  density = 1
  expand = 3
  formula = G4_C-552
  name = G4_C-552
  specific = 4
FEATURE [App::DocumentObjectGroupPython] Cd_element001  label="Cd_element : 1"  # scripted group (container) (typed FeaturePython)
  n = 1
  ref = Cd_element
FEATURE [App::DocumentObjectGroupPython] Te_element001  label="Te_element : 1"  # scripted group (container) (typed FeaturePython)
  n = 1
  ref = Te_element
FEATURE [App::DocumentObjectGroupPython] G4_CADMIUM_TELLURIDE  # scripted group (container) (typed FeaturePython)
  Dunit = g/cm3
  Dvalue = 6.2
  Group = -> [Cd_element001,Te_element001]
  conduct = 2
  density = 1
  expand = 3
  formula = G4_CADMIUM_TELLURIDE
  name = G4_CADMIUM_TELLURIDE
  specific = 4
FEATURE [App::DocumentObjectGroupPython] Cd_element002  label="Cd_element : 002"  # scripted group (container) (typed FeaturePython)
  n = 1
  ref = Cd_element
FEATURE [App::DocumentObjectGroupPython] W_element001  label="W_element : 1"  # scripted group (container) (typed FeaturePython)
  n = 1
  ref = W_element
FEATURE [App::DocumentObjectGroupPython] O_element020  label="O_element : 008"  # scripted group (container) (typed FeaturePython)
  n = 4
  ref = O_element
FEATURE [App::DocumentObjectGroupPython] G4_CADMIUM_TUNGSTATE  # scripted group (container) (typed FeaturePython)
  Dunit = g/cm3
  Dvalue = 7.9
  Group = -> [Cd_element002,W_element001,O_element020]
  conduct = 2
  density = 1
  expand = 3
  formula = G4_CADMIUM_TUNGSTATE
  name = G4_CADMIUM_TUNGSTATE
  specific = 4
FEATURE [App::DocumentObjectGroupPython] Ca_element005  label="Ca_element : 1"  # scripted group (container) (typed FeaturePython)
  n = 1
  ref = Ca_element
FEATURE [App::DocumentObjectGroupPython] C_element022  label="C_element : 009"  # scripted group (container) (typed FeaturePython)
  n = 1
  ref = C_element
FEATURE [App::DocumentObjectGroupPython] O_element021  label="O_element : 009"  # scripted group (container) (typed FeaturePython)
  n = 3
  ref = O_element
FEATURE [App::DocumentObjectGroupPython] G4_CALCIUM_CARBONATE  # scripted group (container) (typed FeaturePython)
  Dunit = g/cm3
  Dvalue = 2.8
  Group = -> [Ca_element005,C_element022,O_element021]
  conduct = 2
  density = 1
  expand = 3
  formula = G4_CALCIUM_CARBONATE
  name = G4_CALCIUM_CARBONATE
  specific = 4
FEATURE [App::DocumentObjectGroupPython] Ca_element006  label="Ca_element : 002"  # scripted group (container) (typed FeaturePython)
  n = 1
  ref = Ca_element
FEATURE [App::DocumentObjectGroupPython] F_element005  label="F_element : 003"  # scripted group (container) (typed FeaturePython)
  n = 2
  ref = F_element
FEATURE [App::DocumentObjectGroupPython] G4_CALCIUM_FLUORIDE  # scripted group (container) (typed FeaturePython)
  Dunit = g/cm3
  Dvalue = 3.18
  Group = -> [Ca_element006,F_element005]
  conduct = 2
  density = 1
  expand = 3
  formula = G4_CALCIUM_FLUORIDE
  name = G4_CALCIUM_FLUORIDE
  specific = 4
FEATURE [App::DocumentObjectGroupPython] Ca_element007  label="Ca_element : 003"  # scripted group (container) (typed FeaturePython)
  n = 1
  ref = Ca_element
FEATURE [App::DocumentObjectGroupPython] O_element022  label="O_element : 010"  # scripted group (container) (typed FeaturePython)
  n = 1
  ref = O_element
FEATURE [App::DocumentObjectGroupPython] G4_CALCIUM_OXIDE  # scripted group (container) (typed FeaturePython)
  Dunit = g/cm3
  Dvalue = 3.3
  Group = -> [Ca_element007,O_element022]
  conduct = 2
  density = 1
  expand = 3
  formula = G4_CALCIUM_OXIDE
  name = G4_CALCIUM_OXIDE
  specific = 4
FEATURE [App::DocumentObjectGroupPython] Ca_element008  label="Ca_element : 004"  # scripted group (container) (typed FeaturePython)
  n = 1
  ref = Ca_element
FEATURE [App::DocumentObjectGroupPython] S_element007  label="S_element : 002"  # scripted group (container) (typed FeaturePython)
  n = 1
  ref = S_element
FEATURE [App::DocumentObjectGroupPython] O_element023  label="O_element : 011"  # scripted group (container) (typed FeaturePython)
  n = 4
  ref = O_element
FEATURE [App::DocumentObjectGroupPython] G4_CALCIUM_SULFATE  # scripted group (container) (typed FeaturePython)
  Dunit = g/cm3
  Dvalue = 2.96
  Group = -> [Ca_element008,S_element007,O_element023]
  conduct = 2
  density = 1
  expand = 3
  formula = G4_CALCIUM_SULFATE
  name = G4_CALCIUM_SULFATE
  specific = 4
FEATURE [App::DocumentObjectGroupPython] Ca_element009  label="Ca_element : 005"  # scripted group (container) (typed FeaturePython)
  n = 1
  ref = Ca_element
FEATURE [App::DocumentObjectGroupPython] W_element002  label="W_element : 002"  # scripted group (container) (typed FeaturePython)
  n = 1
  ref = W_element
FEATURE [App::DocumentObjectGroupPython] O_element024  label="O_element : 012"  # scripted group (container) (typed FeaturePython)
  n = 4
  ref = O_element
FEATURE [App::DocumentObjectGroupPython] G4_CALCIUM_TUNGSTATE  # scripted group (container) (typed FeaturePython)
  Dunit = g/cm3
  Dvalue = 6.062
  Group = -> [Ca_element009,W_element002,O_element024]
  conduct = 2
  density = 1
  expand = 3
  formula = G4_CALCIUM_TUNGSTATE
  name = G4_CALCIUM_TUNGSTATE
  specific = 4
FEATURE [App::DocumentObjectGroupPython] C_element023  label="C_element : 010"  # scripted group (container) (typed FeaturePython)
  n = 1
  ref = C_element
FEATURE [App::DocumentObjectGroupPython] O_element025  label="O_element : 013"  # scripted group (container) (typed FeaturePython)
  n = 2
  ref = O_element
FEATURE [App::DocumentObjectGroupPython] G4_CARBON_DIOXIDE  # scripted group (container) (typed FeaturePython)
  Dunit = g/cm3
  Dvalue = 0.00184212
  Group = -> [C_element023,O_element025]
  conduct = 2
  density = 1
  expand = 3
  formula = G4_CARBON_DIOXIDE
  name = G4_CARBON_DIOXIDE
  specific = 4
FEATURE [App::DocumentObjectGroupPython] C_element024  label="C_element : 011"  # scripted group (container) (typed FeaturePython)
  n = 1
  ref = C_element
FEATURE [App::DocumentObjectGroupPython] Cl_element004  label="Cl_element : 4"  # scripted group (container) (typed FeaturePython)
  n = 4
  ref = Cl_element
FEATURE [App::DocumentObjectGroupPython] G4_CARBON_TETRACHLORIDE  # scripted group (container) (typed FeaturePython)
  Dunit = g/cm3
  Dvalue = 1.594
  Group = -> [C_element024,Cl_element004]
  conduct = 2
  density = 1
  expand = 3
  formula = G4_CARBON_TETRACHLORIDE
  name = G4_CARBON_TETRACHLORIDE
  specific = 4
FEATURE [App::DocumentObjectGroupPython] C_element025  label="C_element : 012"  # scripted group (container) (typed FeaturePython)
  n = 6
  ref = C_element
FEATURE [App::DocumentObjectGroupPython] H_element021  label="H_element : 012"  # scripted group (container) (typed FeaturePython)
  n = 10
  ref = H_element
FEATURE [App::DocumentObjectGroupPython] O_element026  label="O_element : 5"  # scripted group (container) (typed FeaturePython)
  n = 5
  ref = O_element
FEATURE [App::DocumentObjectGroupPython] G4_CELLULOSE_CELLOPHANE  # scripted group (container) (typed FeaturePython)
  Dunit = g/cm3
  Dvalue = 1.42
  Group = -> [C_element025,H_element021,O_element026]
  conduct = 2
  density = 1
  expand = 3
  formula = G4_CELLULOSE_CELLOPHANE
  name = G4_CELLULOSE_CELLOPHANE
  specific = 4
FEATURE [App::DocumentObjectGroupPython] H_element022  label="H_element : 0.067"  # scripted group (container) (typed FeaturePython)
  n = 0.067125
FEATURE [App::DocumentObjectGroupPython] C_element026  label="C_element : 0.545"  # scripted group (container) (typed FeaturePython)
  n = 0.545403
FEATURE [App::DocumentObjectGroupPython] O_element027  label="O_element : 0.387"  # scripted group (container) (typed FeaturePython)
  n = 0.387472
FEATURE [App::DocumentObjectGroupPython] G4_CELLULOSE_BUTYRATE  # scripted group (container) (typed FeaturePython)
  Dunit = g/cm3
  Dvalue = 1.2
  Group = -> [H_element022,C_element026,O_element027]
  conduct = 2
  density = 1
  expand = 3
  formula = G4_CELLULOSE_BUTYRATE
  name = G4_CELLULOSE_BUTYRATE
  specific = 4
FEATURE [App::DocumentObjectGroupPython] H_element023  label="H_element : 0.029"  # scripted group (container) (typed FeaturePython)
  n = 0.029216
FEATURE [App::DocumentObjectGroupPython] C_element027  label="C_element : 0.271"  # scripted group (container) (typed FeaturePython)
  n = 0.271296
FEATURE [App::DocumentObjectGroupPython] N_element013  label="N_element : 0.121"  # scripted group (container) (typed FeaturePython)
  n = 0.121276
FEATURE [App::DocumentObjectGroupPython] O_element028  label="O_element : 0.578"  # scripted group (container) (typed FeaturePython)
  n = 0.578212
FEATURE [App::DocumentObjectGroupPython] G4_CELLULOSE_NITRATE  # scripted group (container) (typed FeaturePython)
  Dunit = g/cm3
  Dvalue = 1.49
  Group = -> [H_element023,C_element027,N_element013,O_element028]
  conduct = 2
  density = 1
  expand = 3
  formula = G4_CELLULOSE_NITRATE
  name = G4_CELLULOSE_NITRATE
  specific = 4
FEATURE [App::DocumentObjectGroupPython] H_element024  label="H_element : 0.108"  # scripted group (container) (typed FeaturePython)
  n = 0.107596
FEATURE [App::DocumentObjectGroupPython] N_element014  label="N_element : 0.001"  # scripted group (container) (typed FeaturePython)
  n = 0.0008
FEATURE [App::DocumentObjectGroupPython] O_element029  label="O_element : 0.875"  # scripted group (container) (typed FeaturePython)
  n = 0.874976
FEATURE [App::DocumentObjectGroupPython] S_element008  label="S_element : 0.015"  # scripted group (container) (typed FeaturePython)
  n = 0.014627
FEATURE [App::DocumentObjectGroupPython] Ce_element001  label="Ce_element : 0.002"  # scripted group (container) (typed FeaturePython)
  n = 0.002001
FEATURE [App::DocumentObjectGroupPython] G4_CERIC_SULFATE  # scripted group (container) (typed FeaturePython)
  Dunit = g/cm3
  Dvalue = 1.03
  Group = -> [H_element024,N_element014,O_element029,S_element008,Ce_element001]
  conduct = 2
  density = 1
  expand = 3
  formula = G4_CERIC_SULFATE
  name = G4_CERIC_SULFATE
  specific = 4
FEATURE [App::DocumentObjectGroupPython] Cs_element001  label="Cs_element : 1"  # scripted group (container) (typed FeaturePython)
  n = 1
  ref = Cs_element
FEATURE [App::DocumentObjectGroupPython] F_element006  label="F_element : 1"  # scripted group (container) (typed FeaturePython)
  n = 1
  ref = F_element
FEATURE [App::DocumentObjectGroupPython] G4_CESIUM_FLUORIDE  # scripted group (container) (typed FeaturePython)
  Dunit = g/cm3
  Dvalue = 4.115
  Group = -> [Cs_element001,F_element006]
  conduct = 2
  density = 1
  expand = 3
  formula = G4_CESIUM_FLUORIDE
  name = G4_CESIUM_FLUORIDE
  specific = 4
FEATURE [App::DocumentObjectGroupPython] Cs_element002  label="Cs_element : 002"  # scripted group (container) (typed FeaturePython)
  n = 1
  ref = Cs_element
FEATURE [App::DocumentObjectGroupPython] I_element001  label="I_element : 1"  # scripted group (container) (typed FeaturePython)
  n = 1
  ref = I_element
FEATURE [App::DocumentObjectGroupPython] G4_CESIUM_IODIDE  # scripted group (container) (typed FeaturePython)
  Dunit = g/cm3
  Dvalue = 4.51
  Group = -> [Cs_element002,I_element001]
  conduct = 2
  density = 1
  expand = 3
  formula = G4_CESIUM_IODIDE
  name = G4_CESIUM_IODIDE
  specific = 4
FEATURE [App::DocumentObjectGroupPython] C_element028  label="C_element : 013"  # scripted group (container) (typed FeaturePython)
  n = 6
  ref = C_element
FEATURE [App::DocumentObjectGroupPython] H_element025  label="H_element : 013"  # scripted group (container) (typed FeaturePython)
  n = 5
  ref = H_element
FEATURE [App::DocumentObjectGroupPython] Cl_element005  label="Cl_element : 1"  # scripted group (container) (typed FeaturePython)
  n = 1
  ref = Cl_element
FEATURE [App::DocumentObjectGroupPython] G4_CHLOROBENZENE  # scripted group (container) (typed FeaturePython)
  Dunit = g/cm3
  Dvalue = 1.1058
  Group = -> [C_element028,H_element025,Cl_element005]
  conduct = 2
  density = 1
  expand = 3
  formula = G4_CHLOROBENZENE
  name = G4_CHLOROBENZENE
  specific = 4
FEATURE [App::DocumentObjectGroupPython] C_element029  label="C_element : 014"  # scripted group (container) (typed FeaturePython)
  n = 1
  ref = C_element
FEATURE [App::DocumentObjectGroupPython] H_element026  label="H_element : 1"  # scripted group (container) (typed FeaturePython)
  n = 1
  ref = H_element
FEATURE [App::DocumentObjectGroupPython] Cl_element006  label="Cl_element : 3"  # scripted group (container) (typed FeaturePython)
  n = 3
  ref = Cl_element
FEATURE [App::DocumentObjectGroupPython] G4_CHLOROFORM  # scripted group (container) (typed FeaturePython)
  Dunit = g/cm3
  Dvalue = 1.4832
  Group = -> [C_element029,H_element026,Cl_element006]
  conduct = 2
  density = 1
  expand = 3
  formula = G4_CHLOROFORM
  name = G4_CHLOROFORM
  specific = 4
FEATURE [App::DocumentObjectGroupPython] H_element027  label="H_element : 0.010"  # scripted group (container) (typed FeaturePython)
  n = 0.01
FEATURE [App::DocumentObjectGroupPython] C_element030  label="C_element : 0.001"  # scripted group (container) (typed FeaturePython)
  n = 0.001
FEATURE [App::DocumentObjectGroupPython] O_element030  label="O_element : 0.529"  # scripted group (container) (typed FeaturePython)
  n = 0.529107
FEATURE [App::DocumentObjectGroupPython] Na_element005  label="Na_element : 0.016"  # scripted group (container) (typed FeaturePython)
  n = 0.016
FEATURE [App::DocumentObjectGroupPython] Mg_element003  label="Mg_element : 0.004"  # scripted group (container) (typed FeaturePython)
  n = 0.002
FEATURE [App::DocumentObjectGroupPython] Al_element002  label="Al_element : 0.034"  # scripted group (container) (typed FeaturePython)
  n = 0.033872
FEATURE [App::DocumentObjectGroupPython] Si_element002  label="Si_element : 0.337"  # scripted group (container) (typed FeaturePython)
  n = 0.337021
FEATURE [App::DocumentObjectGroupPython] K_element003  label="K_element : 0.013"  # scripted group (container) (typed FeaturePython)
  n = 0.013
FEATURE [App::DocumentObjectGroupPython] Ca_element010  label="Ca_element : 0.044"  # scripted group (container) (typed FeaturePython)
  n = 0.044
FEATURE [App::DocumentObjectGroupPython] Fe_element002  label="Fe_element : 0.014"  # scripted group (container) (typed FeaturePython)
  n = 0.014
FEATURE [App::DocumentObjectGroupPython] G4_CONCRETE  # scripted group (container) (typed FeaturePython)
  Dunit = g/cm3
  Dvalue = 2.3
  Group = -> [H_element027,C_element030,O_element030,Na_element005,Mg_element003,Al_element002,Si_element002,K_element003,Ca_element010,Fe_element002]
  conduct = 2
  density = 1
  expand = 3
  formula = G4_CONCRETE
  name = G4_CONCRETE
  specific = 4
FEATURE [App::DocumentObjectGroupPython] C_element031  label="C_element : 015"  # scripted group (container) (typed FeaturePython)
  n = 6
  ref = C_element
FEATURE [App::DocumentObjectGroupPython] H_element028  label="H_element : 12"  # scripted group (container) (typed FeaturePython)
  n = 12
  ref = H_element
FEATURE [App::DocumentObjectGroupPython] G4_CYCLOHEXANE  # scripted group (container) (typed FeaturePython)
  Dunit = g/cm3
  Dvalue = 0.779
  Group = -> [C_element031,H_element028]
  conduct = 2
  density = 1
  expand = 3
  formula = G4_CYCLOHEXANE
  name = G4_CYCLOHEXANE
  specific = 4
FEATURE [App::DocumentObjectGroupPython] C_element032  label="C_element : 016"  # scripted group (container) (typed FeaturePython)
  n = 6
  ref = C_element
FEATURE [App::DocumentObjectGroupPython] H_element029  label="H_element : 4"  # scripted group (container) (typed FeaturePython)
  n = 4
  ref = H_element
FEATURE [App::DocumentObjectGroupPython] Cl_element007  label="Cl_element : 2"  # scripted group (container) (typed FeaturePython)
  n = 2
  ref = Cl_element
FEATURE [App::DocumentObjectGroupPython] G4_1_2_DICHLOROBENZENE  label="G4_1.2-DICHLOROBENZENE"  # scripted group (container) (typed FeaturePython)
  Dunit = g/cm3
  Dvalue = 1.3048
  Group = -> [C_element032,H_element029,Cl_element007]
  conduct = 2
  density = 1
  expand = 3
  formula = G4_1.2-DICHLOROBENZENE
  name = G4_1.2-DICHLOROBENZENE
  specific = 4
FEATURE [App::DocumentObjectGroupPython] C_element033  label="C_element : 017"  # scripted group (container) (typed FeaturePython)
  n = 4
  ref = C_element
FEATURE [App::DocumentObjectGroupPython] H_element030  label="H_element : 8"  # scripted group (container) (typed FeaturePython)
  n = 8
  ref = H_element
FEATURE [App::DocumentObjectGroupPython] O_element031  label="O_element : 014"  # scripted group (container) (typed FeaturePython)
  n = 1
  ref = O_element
FEATURE [App::DocumentObjectGroupPython] Cl_element008  label="Cl_element : 005"  # scripted group (container) (typed FeaturePython)
  n = 2
  ref = Cl_element
FEATURE [App::DocumentObjectGroupPython] G4_DICHLORODIETHYL_ETHER  # scripted group (container) (typed FeaturePython)
  Dunit = g/cm3
  Dvalue = 1.2199
  Group = -> [C_element033,H_element030,O_element031,Cl_element008]
  conduct = 2
  density = 1
  expand = 3
  formula = G4_DICHLORODIETHYL_ETHER
  name = G4_DICHLORODIETHYL_ETHER
  specific = 4
FEATURE [App::DocumentObjectGroupPython] C_element034  label="C_element : 018"  # scripted group (container) (typed FeaturePython)
  n = 2
  ref = C_element
FEATURE [App::DocumentObjectGroupPython] H_element031  label="H_element : 014"  # scripted group (container) (typed FeaturePython)
  n = 4
  ref = H_element
FEATURE [App::DocumentObjectGroupPython] Cl_element009  label="Cl_element : 006"  # scripted group (container) (typed FeaturePython)
  n = 2
  ref = Cl_element
FEATURE [App::DocumentObjectGroupPython] G4_1_2_DICHLOROETHANE  label="G4_1.2-DICHLOROETHANE"  # scripted group (container) (typed FeaturePython)
  Dunit = g/cm3
  Dvalue = 1.2351
  Group = -> [C_element034,H_element031,Cl_element009]
  conduct = 2
  density = 1
  expand = 3
  formula = G4_1.2-DICHLOROETHANE
  name = G4_1.2-DICHLOROETHANE
  specific = 4
FEATURE [App::DocumentObjectGroupPython] C_element035  label="C_element : 019"  # scripted group (container) (typed FeaturePython)
  n = 4
  ref = C_element
FEATURE [App::DocumentObjectGroupPython] H_element032  label="H_element : 015"  # scripted group (container) (typed FeaturePython)
  n = 10
  ref = H_element
FEATURE [App::DocumentObjectGroupPython] O_element032  label="O_element : 015"  # scripted group (container) (typed FeaturePython)
  n = 1
  ref = O_element
FEATURE [App::DocumentObjectGroupPython] G4_DIETHYL_ETHER  # scripted group (container) (typed FeaturePython)
  Dunit = g/cm3
  Dvalue = 0.71378
  Group = -> [C_element035,H_element032,O_element032]
  conduct = 2
  density = 1
  expand = 3
  formula = G4_DIETHYL_ETHER
  name = G4_DIETHYL_ETHER
  specific = 4
FEATURE [App::DocumentObjectGroupPython] C_element036  label="C_element : 020"  # scripted group (container) (typed FeaturePython)
  n = 3
  ref = C_element
FEATURE [App::DocumentObjectGroupPython] H_element033  label="H_element : 016"  # scripted group (container) (typed FeaturePython)
  n = 7
  ref = H_element
FEATURE [App::DocumentObjectGroupPython] N_element015  label="N_element : 008"  # scripted group (container) (typed FeaturePython)
  n = 1
  ref = N_element
FEATURE [App::DocumentObjectGroupPython] O_element033  label="O_element : 016"  # scripted group (container) (typed FeaturePython)
  n = 1
  ref = O_element
FEATURE [App::DocumentObjectGroupPython] G4_N_N_DIMETHYL_FORMAMIDE  label="G4_N.N-DIMETHYL_FORMAMIDE"  # scripted group (container) (typed FeaturePython)
  Dunit = g/cm3
  Dvalue = 0.9487
  Group = -> [C_element036,H_element033,N_element015,O_element033]
  conduct = 2
  density = 1
  expand = 3
  formula = G4_N.N-DIMETHYL_FORMAMIDE
  name = G4_N.N-DIMETHYL_FORMAMIDE
  specific = 4
FEATURE [App::DocumentObjectGroupPython] C_element037  label="C_element : 021"  # scripted group (container) (typed FeaturePython)
  n = 2
  ref = C_element
FEATURE [App::DocumentObjectGroupPython] H_element034  label="H_element : 017"  # scripted group (container) (typed FeaturePython)
  n = 6
  ref = H_element
FEATURE [App::DocumentObjectGroupPython] O_element034  label="O_element : 017"  # scripted group (container) (typed FeaturePython)
  n = 1
  ref = O_element
FEATURE [App::DocumentObjectGroupPython] S_element009  label="S_element : 003"  # scripted group (container) (typed FeaturePython)
  n = 1
  ref = S_element
FEATURE [App::DocumentObjectGroupPython] G4_DIMETHYL_SULFOXIDE  # scripted group (container) (typed FeaturePython)
  Dunit = g/cm3
  Dvalue = 1.1014
  Group = -> [C_element037,H_element034,O_element034,S_element009]
  conduct = 2
  density = 1
  expand = 3
  formula = G4_DIMETHYL_SULFOXIDE
  name = G4_DIMETHYL_SULFOXIDE
  specific = 4
FEATURE [App::DocumentObjectGroupPython] C_element038  label="C_element : 022"  # scripted group (container) (typed FeaturePython)
  n = 2
  ref = C_element
FEATURE [App::DocumentObjectGroupPython] H_element035  label="H_element : 018"  # scripted group (container) (typed FeaturePython)
  n = 6
  ref = H_element
FEATURE [App::DocumentObjectGroupPython] G4_ETHANE  # scripted group (container) (typed FeaturePython)
  Dunit = g/cm3
  Dvalue = 0.00125324
  Group = -> [C_element038,H_element035]
  conduct = 2
  density = 1
  expand = 3
  formula = G4_ETHANE
  name = G4_ETHANE
  specific = 4
FEATURE [App::DocumentObjectGroupPython] C_element039  label="C_element : 023"  # scripted group (container) (typed FeaturePython)
  n = 2
  ref = C_element
FEATURE [App::DocumentObjectGroupPython] H_element036  label="H_element : 019"  # scripted group (container) (typed FeaturePython)
  n = 6
  ref = H_element
FEATURE [App::DocumentObjectGroupPython] O_element035  label="O_element : 018"  # scripted group (container) (typed FeaturePython)
  n = 1
  ref = O_element
FEATURE [App::DocumentObjectGroupPython] G4_ETHYL_ALCOHOL  # scripted group (container) (typed FeaturePython)
  Dunit = g/cm3
  Dvalue = 0.7893
  Group = -> [C_element039,H_element036,O_element035]
  conduct = 2
  density = 1
  expand = 3
  formula = G4_ETHYL_ALCOHOL
  name = G4_ETHYL_ALCOHOL
  specific = 4
FEATURE [App::DocumentObjectGroupPython] H_element037  label="H_element : 0.090"  # scripted group (container) (typed FeaturePython)
  n = 0.090027
FEATURE [App::DocumentObjectGroupPython] C_element040  label="C_element : 0.585"  # scripted group (container) (typed FeaturePython)
  n = 0.585182
FEATURE [App::DocumentObjectGroupPython] O_element036  label="O_element : 0.325"  # scripted group (container) (typed FeaturePython)
  n = 0.324791
FEATURE [App::DocumentObjectGroupPython] G4_ETHYL_CELLULOSE  # scripted group (container) (typed FeaturePython)
  Dunit = g/cm3
  Dvalue = 1.13
  Group = -> [H_element037,C_element040,O_element036]
  conduct = 2
  density = 1
  expand = 3
  formula = G4_ETHYL_CELLULOSE
  name = G4_ETHYL_CELLULOSE
  specific = 4
FEATURE [App::DocumentObjectGroupPython] C_element041  label="C_element : 024"  # scripted group (container) (typed FeaturePython)
  n = 2
  ref = C_element
FEATURE [App::DocumentObjectGroupPython] H_element038  label="H_element : 020"  # scripted group (container) (typed FeaturePython)
  n = 4
  ref = H_element
FEATURE [App::DocumentObjectGroupPython] G4_ETHYLENE  # scripted group (container) (typed FeaturePython)
  Dunit = g/cm3
  Dvalue = 0.00117497
  Group = -> [C_element041,H_element038]
  conduct = 2
  density = 1
  expand = 3
  formula = G4_ETHYLENE
  name = G4_ETHYLENE
  specific = 4
FEATURE [App::DocumentObjectGroupPython] H_element039  label="H_element : 0.096"  # scripted group (container) (typed FeaturePython)
  n = 0.096
FEATURE [App::DocumentObjectGroupPython] C_element042  label="C_element : 0.195"  # scripted group (container) (typed FeaturePython)
  n = 0.195
FEATURE [App::DocumentObjectGroupPython] N_element016  label="N_element : 0.057"  # scripted group (container) (typed FeaturePython)
  n = 0.057
FEATURE [App::DocumentObjectGroupPython] O_element037  label="O_element : 0.646"  # scripted group (container) (typed FeaturePython)
  n = 0.646
FEATURE [App::DocumentObjectGroupPython] Na_element006  label="Na_element : 0.017"  # scripted group (container) (typed FeaturePython)
  n = 0.001
FEATURE [App::DocumentObjectGroupPython] P_element005  label="P_element : 0.104"  # scripted group (container) (typed FeaturePython)
  n = 0.001
FEATURE [App::DocumentObjectGroupPython] S_element010  label="S_element : 0.016"  # scripted group (container) (typed FeaturePython)
  n = 0.003
FEATURE [App::DocumentObjectGroupPython] Cl_element010  label="Cl_element : 0.005"  # scripted group (container) (typed FeaturePython)
  n = 0.001
FEATURE [App::DocumentObjectGroupPython] G4_EYE_LENS_ICRP  # scripted group (container) (typed FeaturePython)
  Dunit = g/cm3
  Dvalue = 1.07
  Group = -> [H_element039,C_element042,N_element016,O_element037,Na_element006,P_element005,S_element010,Cl_element010]
  conduct = 2
  density = 1
  expand = 3
  formula = G4_EYE_LENS_ICRP
  name = G4_EYE_LENS_ICRP
  specific = 4
FEATURE [App::DocumentObjectGroupPython] Fe_element003  label="Fe_element : 2"  # scripted group (container) (typed FeaturePython)
  n = 2
  ref = Fe_element
FEATURE [App::DocumentObjectGroupPython] O_element038  label="O_element : 019"  # scripted group (container) (typed FeaturePython)
  n = 3
  ref = O_element
FEATURE [App::DocumentObjectGroupPython] G4_FERRIC_OXIDE  # scripted group (container) (typed FeaturePython)
  Dunit = g/cm3
  Dvalue = 5.2
  Group = -> [Fe_element003,O_element038]
  conduct = 2
  density = 1
  expand = 3
  formula = G4_FERRIC_OXIDE
  name = G4_FERRIC_OXIDE
  specific = 4
FEATURE [App::DocumentObjectGroupPython] Fe_element004  label="Fe_element : 1"  # scripted group (container) (typed FeaturePython)
  n = 1
  ref = Fe_element
FEATURE [App::DocumentObjectGroupPython] B_element003  label="B_element : 1"  # scripted group (container) (typed FeaturePython)
  n = 1
  ref = B_element
FEATURE [App::DocumentObjectGroupPython] G4_FERROBORIDE  # scripted group (container) (typed FeaturePython)
  Dunit = g/cm3
  Dvalue = 7.15
  Group = -> [Fe_element004,B_element003]
  conduct = 2
  density = 1
  expand = 3
  formula = G4_FERROBORIDE
  name = G4_FERROBORIDE
  specific = 4
FEATURE [App::DocumentObjectGroupPython] Fe_element005  label="Fe_element : 003"  # scripted group (container) (typed FeaturePython)
  n = 1
  ref = Fe_element
FEATURE [App::DocumentObjectGroupPython] O_element039  label="O_element : 020"  # scripted group (container) (typed FeaturePython)
  n = 1
  ref = O_element
FEATURE [App::DocumentObjectGroupPython] G4_FERROUS_OXIDE  # scripted group (container) (typed FeaturePython)
  Dunit = g/cm3
  Dvalue = 5.7
  Group = -> [Fe_element005,O_element039]
  conduct = 2
  density = 1
  expand = 3
  formula = G4_FERROUS_OXIDE
  name = G4_FERROUS_OXIDE
  specific = 4
FEATURE [App::DocumentObjectGroupPython] H_element040  label="H_element : 0.115"  # scripted group (container) (typed FeaturePython)
  n = 0.108259
FEATURE [App::DocumentObjectGroupPython] N_element017  label="N_element : 0.000"  # scripted group (container) (typed FeaturePython)
  n = 2.7e-05
FEATURE [App::DocumentObjectGroupPython] O_element040  label="O_element : 0.879"  # scripted group (container) (typed FeaturePython)
  n = 0.878636
FEATURE [App::DocumentObjectGroupPython] Na_element007  label="Na_element : 0.000"  # scripted group (container) (typed FeaturePython)
  n = 2.2e-05
FEATURE [App::DocumentObjectGroupPython] S_element011  label="S_element : 0.013"  # scripted group (container) (typed FeaturePython)
  n = 0.012968
FEATURE [App::DocumentObjectGroupPython] Cl_element011  label="Cl_element : 0.000"  # scripted group (container) (typed FeaturePython)
  n = 3.4e-05
FEATURE [App::DocumentObjectGroupPython] Fe_element006  label="Fe_element : 0.000"  # scripted group (container) (typed FeaturePython)
  n = 5.4e-05
FEATURE [App::DocumentObjectGroupPython] G4_FERROUS_SULFATE  # scripted group (container) (typed FeaturePython)
  Dunit = g/cm3
  Dvalue = 1.024
  Group = -> [H_element040,N_element017,O_element040,Na_element007,S_element011,Cl_element011,Fe_element006]
  conduct = 2
  density = 1
  expand = 3
  formula = G4_FERROUS_SULFATE
  name = G4_FERROUS_SULFATE
  specific = 4
FEATURE [App::DocumentObjectGroupPython] C_element043  label="C_element : 0.099"  # scripted group (container) (typed FeaturePython)
  n = 0.099335
FEATURE [App::DocumentObjectGroupPython] F_element007  label="F_element : 0.314"  # scripted group (container) (typed FeaturePython)
  n = 0.314247
FEATURE [App::DocumentObjectGroupPython] Cl_element012  label="Cl_element : 0.586"  # scripted group (container) (typed FeaturePython)
  n = 0.586418
FEATURE [App::DocumentObjectGroupPython] G4_FREON_12  label="G4_FREON-12"  # scripted group (container) (typed FeaturePython)
  Dunit = g/cm3
  Dvalue = 1.12
  Group = -> [C_element043,F_element007,Cl_element012]
  conduct = 2
  density = 1
  expand = 3
  formula = G4_FREON-12
  name = G4_FREON-12
  specific = 4
FEATURE [App::DocumentObjectGroupPython] C_element044  label="C_element : 0.057"  # scripted group (container) (typed FeaturePython)
  n = 0.057245
FEATURE [App::DocumentObjectGroupPython] F_element008  label="F_element : 0.181"  # scripted group (container) (typed FeaturePython)
  n = 0.181096
FEATURE [App::DocumentObjectGroupPython] Br_element001  label="Br_element : 0.762"  # scripted group (container) (typed FeaturePython)
  n = 0.761659
FEATURE [App::DocumentObjectGroupPython] G4_FREON_12B2  label="G4_FREON-12B2"  # scripted group (container) (typed FeaturePython)
  Dunit = g/cm3
  Dvalue = 1.8
  Group = -> [C_element044,F_element008,Br_element001]
  conduct = 2
  density = 1
  expand = 3
  formula = G4_FREON-12B2
  name = G4_FREON-12B2
  specific = 4
FEATURE [App::DocumentObjectGroupPython] C_element045  label="C_element : 0.115"  # scripted group (container) (typed FeaturePython)
  n = 0.114983
FEATURE [App::DocumentObjectGroupPython] F_element009  label="F_element : 0.546"  # scripted group (container) (typed FeaturePython)
  n = 0.545621
FEATURE [App::DocumentObjectGroupPython] Cl_element013  label="Cl_element : 0.339"  # scripted group (container) (typed FeaturePython)
  n = 0.339396
FEATURE [App::DocumentObjectGroupPython] G4_FREON_13  label="G4_FREON-13"  # scripted group (container) (typed FeaturePython)
  Dunit = g/cm3
  Dvalue = 0.95
  Group = -> [C_element045,F_element009,Cl_element013]
  conduct = 2
  density = 1
  expand = 3
  formula = G4_FREON-13
  name = G4_FREON-13
  specific = 4
FEATURE [App::DocumentObjectGroupPython] C_element046  label="C_element : 025"  # scripted group (container) (typed FeaturePython)
  n = 1
  ref = C_element
FEATURE [App::DocumentObjectGroupPython] F_element010  label="F_element : 3"  # scripted group (container) (typed FeaturePython)
  n = 3
  ref = F_element
FEATURE [App::DocumentObjectGroupPython] Br_element002  label="Br_element : 1"  # scripted group (container) (typed FeaturePython)
  n = 1
  ref = Br_element
FEATURE [App::DocumentObjectGroupPython] G4_FREON_13B1  label="G4_FREON-13B1"  # scripted group (container) (typed FeaturePython)
  Dunit = g/cm3
  Dvalue = 1.5
  Group = -> [C_element046,F_element010,Br_element002]
  conduct = 2
  density = 1
  expand = 3
  formula = G4_FREON-13B1
  name = G4_FREON-13B1
  specific = 4
FEATURE [App::DocumentObjectGroupPython] C_element047  label="C_element : 0.061"  # scripted group (container) (typed FeaturePython)
  n = 0.061309
FEATURE [App::DocumentObjectGroupPython] F_element011  label="F_element : 0.291"  # scripted group (container) (typed FeaturePython)
  n = 0.290924
FEATURE [App::DocumentObjectGroupPython] I_element002  label="I_element : 0.648"  # scripted group (container) (typed FeaturePython)
  n = 0.647767
FEATURE [App::DocumentObjectGroupPython] G4_FREON_13I1  label="G4_FREON-13I1"  # scripted group (container) (typed FeaturePython)
  Dunit = g/cm3
  Dvalue = 1.8
  Group = -> [C_element047,F_element011,I_element002]
  conduct = 2
  density = 1
  expand = 3
  formula = G4_FREON-13I1
  name = G4_FREON-13I1
  specific = 4
FEATURE [App::DocumentObjectGroupPython] Gd_element001  label="Gd_element : 2"  # scripted group (container) (typed FeaturePython)
  n = 2
  ref = Gd_element
FEATURE [App::DocumentObjectGroupPython] O_element041  label="O_element : 021"  # scripted group (container) (typed FeaturePython)
  n = 2
  ref = O_element
FEATURE [App::DocumentObjectGroupPython] S_element012  label="S_element : 004"  # scripted group (container) (typed FeaturePython)
  n = 1
  ref = S_element
FEATURE [App::DocumentObjectGroupPython] G4_GADOLINIUM_OXYSULFIDE  # scripted group (container) (typed FeaturePython)
  Dunit = g/cm3
  Dvalue = 7.44
  Group = -> [Gd_element001,O_element041,S_element012]
  conduct = 2
  density = 1
  expand = 3
  formula = G4_GADOLINIUM_OXYSULFIDE
  name = G4_GADOLINIUM_OXYSULFIDE
  specific = 4
FEATURE [App::DocumentObjectGroupPython] Ga_element001  label="Ga_element : 1"  # scripted group (container) (typed FeaturePython)
  n = 1
  ref = Ga_element
FEATURE [App::DocumentObjectGroupPython] As_element001  label="As_element : 1"  # scripted group (container) (typed FeaturePython)
  n = 1
  ref = As_element
FEATURE [App::DocumentObjectGroupPython] G4_GALLIUM_ARSENIDE  # scripted group (container) (typed FeaturePython)
  Dunit = g/cm3
  Dvalue = 5.31
  Group = -> [Ga_element001,As_element001]
  conduct = 2
  density = 1
  expand = 3
  formula = G4_GALLIUM_ARSENIDE
  name = G4_GALLIUM_ARSENIDE
  specific = 4
FEATURE [App::DocumentObjectGroupPython] H_element041  label="H_element : 0.081"  # scripted group (container) (typed FeaturePython)
  n = 0.08118
FEATURE [App::DocumentObjectGroupPython] C_element048  label="C_element : 0.416"  # scripted group (container) (typed FeaturePython)
  n = 0.41606
FEATURE [App::DocumentObjectGroupPython] N_element018  label="N_element : 0.111"  # scripted group (container) (typed FeaturePython)
  n = 0.11124
FEATURE [App::DocumentObjectGroupPython] O_element042  label="O_element : 0.381"  # scripted group (container) (typed FeaturePython)
  n = 0.38064
FEATURE [App::DocumentObjectGroupPython] S_element013  label="S_element : 0.011"  # scripted group (container) (typed FeaturePython)
  n = 0.01088
FEATURE [App::DocumentObjectGroupPython] G4_GEL_PHOTO_EMULSION  # scripted group (container) (typed FeaturePython)
  Dunit = g/cm3
  Dvalue = 1.2914
  Group = -> [H_element041,C_element048,N_element018,O_element042,S_element013]
  conduct = 2
  density = 1
  expand = 3
  formula = G4_GEL_PHOTO_EMULSION
  name = G4_GEL_PHOTO_EMULSION
  specific = 4
FEATURE [App::DocumentObjectGroupPython] B_element004  label="B_element : 0.040"  # scripted group (container) (typed FeaturePython)
  n = 0.0400639
FEATURE [App::DocumentObjectGroupPython] O_element043  label="O_element : 0.540"  # scripted group (container) (typed FeaturePython)
  n = 0.539561
FEATURE [App::DocumentObjectGroupPython] Na_element008  label="Na_element : 0.028"  # scripted group (container) (typed FeaturePython)
  n = 0.0281909
FEATURE [App::DocumentObjectGroupPython] Al_element003  label="Al_element : 0.012"  # scripted group (container) (typed FeaturePython)
  n = 0.011644
FEATURE [App::DocumentObjectGroupPython] Si_element003  label="Si_element : 0.377"  # scripted group (container) (typed FeaturePython)
  n = 0.377219
FEATURE [App::DocumentObjectGroupPython] K_element004  label="K_element : 0.014"  # scripted group (container) (typed FeaturePython)
  n = 0.00332099
FEATURE [App::DocumentObjectGroupPython] G4_Pyrex_Glass  # scripted group (container) (typed FeaturePython)
  Dunit = g/cm3
  Dvalue = 2.23
  Group = -> [B_element004,O_element043,Na_element008,Al_element003,Si_element003,K_element004]
  conduct = 2
  density = 1
  expand = 3
  formula = G4_Pyrex_Glass
  name = G4_Pyrex_Glass
  specific = 4
FEATURE [App::DocumentObjectGroupPython] O_element044  label="O_element : 0.156"  # scripted group (container) (typed FeaturePython)
  n = 0.156453
FEATURE [App::DocumentObjectGroupPython] Si_element004  label="Si_element : 0.081"  # scripted group (container) (typed FeaturePython)
  n = 0.080866
FEATURE [App::DocumentObjectGroupPython] Ti_element001  label="Ti_element : 0.008"  # scripted group (container) (typed FeaturePython)
  n = 0.008092
FEATURE [App::DocumentObjectGroupPython] As_element002  label="As_element : 0.003"  # scripted group (container) (typed FeaturePython)
  n = 0.002651
FEATURE [App::DocumentObjectGroupPython] Pb_element001  label="Pb_element : 0.752"  # scripted group (container) (typed FeaturePython)
  n = 0.751938
FEATURE [App::DocumentObjectGroupPython] G4_GLASS_LEAD  # scripted group (container) (typed FeaturePython)
  Dunit = g/cm3
  Dvalue = 6.22
  Group = -> [O_element044,Si_element004,Ti_element001,As_element002,Pb_element001]
  conduct = 2
  density = 1
  expand = 3
  formula = G4_GLASS_LEAD
  name = G4_GLASS_LEAD
  specific = 4
FEATURE [App::DocumentObjectGroupPython] O_element045  label="O_element : 0.460"  # scripted group (container) (typed FeaturePython)
  n = 0.4598
FEATURE [App::DocumentObjectGroupPython] Na_element009  label="Na_element : 0.096"  # scripted group (container) (typed FeaturePython)
  n = 0.0964411
FEATURE [App::DocumentObjectGroupPython] Si_element005  label="Si_element : 0.378"  # scripted group (container) (typed FeaturePython)
  n = 0.336553
FEATURE [App::DocumentObjectGroupPython] Ca_element011  label="Ca_element : 0.107"  # scripted group (container) (typed FeaturePython)
  n = 0.107205
FEATURE [App::DocumentObjectGroupPython] G4_GLASS_PLATE  # scripted group (container) (typed FeaturePython)
  Dunit = g/cm3
  Dvalue = 2.4
  Group = -> [O_element045,Na_element009,Si_element005,Ca_element011]
  conduct = 2
  density = 1
  expand = 3
  formula = G4_GLASS_PLATE
  name = G4_GLASS_PLATE
  specific = 4
FEATURE [App::DocumentObjectGroupPython] C_element049  label="C_element : 026"  # scripted group (container) (typed FeaturePython)
  n = 5
  ref = C_element
FEATURE [App::DocumentObjectGroupPython] H_element042  label="H_element : 021"  # scripted group (container) (typed FeaturePython)
  n = 10
  ref = H_element
FEATURE [App::DocumentObjectGroupPython] N_element019  label="N_element : 2"  # scripted group (container) (typed FeaturePython)
  n = 2
  ref = N_element
FEATURE [App::DocumentObjectGroupPython] O_element046  label="O_element : 022"  # scripted group (container) (typed FeaturePython)
  n = 3
  ref = O_element
FEATURE [App::DocumentObjectGroupPython] G4_GLUTAMINE  # scripted group (container) (typed FeaturePython)
  Dunit = g/cm3
  Dvalue = 1.46
  Group = -> [C_element049,H_element042,N_element019,O_element046]
  conduct = 2
  density = 1
  expand = 3
  formula = G4_GLUTAMINE
  name = G4_GLUTAMINE
  specific = 4
FEATURE [App::DocumentObjectGroupPython] C_element050  label="C_element : 027"  # scripted group (container) (typed FeaturePython)
  n = 3
  ref = C_element
FEATURE [App::DocumentObjectGroupPython] H_element043  label="H_element : 022"  # scripted group (container) (typed FeaturePython)
  n = 8
  ref = H_element
FEATURE [App::DocumentObjectGroupPython] O_element047  label="O_element : 023"  # scripted group (container) (typed FeaturePython)
  n = 3
  ref = O_element
FEATURE [App::DocumentObjectGroupPython] G4_GLYCEROL  # scripted group (container) (typed FeaturePython)
  Dunit = g/cm3
  Dvalue = 1.2613
  Group = -> [C_element050,H_element043,O_element047]
  conduct = 2
  density = 1
  expand = 3
  formula = G4_GLYCEROL
  name = G4_GLYCEROL
  specific = 4
FEATURE [App::DocumentObjectGroupPython] C_element051  label="C_element : 028"  # scripted group (container) (typed FeaturePython)
  n = 5
  ref = C_element
FEATURE [App::DocumentObjectGroupPython] H_element044  label="H_element : 023"  # scripted group (container) (typed FeaturePython)
  n = 5
  ref = H_element
FEATURE [App::DocumentObjectGroupPython] N_element020  label="N_element : 009"  # scripted group (container) (typed FeaturePython)
  n = 5
  ref = N_element
FEATURE [App::DocumentObjectGroupPython] O_element048  label="O_element : 024"  # scripted group (container) (typed FeaturePython)
  n = 1
  ref = O_element
FEATURE [App::DocumentObjectGroupPython] G4_GUANINE  # scripted group (container) (typed FeaturePython)
  Dunit = g/cm3
  Dvalue = 2.2
  Group = -> [C_element051,H_element044,N_element020,O_element048]
  conduct = 2
  density = 1
  expand = 3
  formula = G4_GUANINE
  name = G4_GUANINE
  specific = 4
FEATURE [App::DocumentObjectGroupPython] Ca_element012  label="Ca_element : 006"  # scripted group (container) (typed FeaturePython)
  n = 1
  ref = Ca_element
FEATURE [App::DocumentObjectGroupPython] S_element014  label="S_element : 005"  # scripted group (container) (typed FeaturePython)
  n = 1
  ref = S_element
FEATURE [App::DocumentObjectGroupPython] O_element049  label="O_element : 6"  # scripted group (container) (typed FeaturePython)
  n = 6
  ref = O_element
FEATURE [App::DocumentObjectGroupPython] H_element045  label="H_element : 024"  # scripted group (container) (typed FeaturePython)
  n = 4
  ref = H_element
FEATURE [App::DocumentObjectGroupPython] G4_GYPSUM  # scripted group (container) (typed FeaturePython)
  Dunit = g/cm3
  Dvalue = 2.32
  Group = -> [Ca_element012,S_element014,O_element049,H_element045]
  conduct = 2
  density = 1
  expand = 3
  formula = G4_GYPSUM
  name = G4_GYPSUM
  specific = 4
FEATURE [App::DocumentObjectGroupPython] C_element052  label="C_element : 7"  # scripted group (container) (typed FeaturePython)
  n = 7
  ref = C_element
FEATURE [App::DocumentObjectGroupPython] H_element046  label="H_element : 16"  # scripted group (container) (typed FeaturePython)
  n = 16
  ref = H_element
FEATURE [App::DocumentObjectGroupPython] G4_N_HEPTANE  label="G4_N-HEPTANE"  # scripted group (container) (typed FeaturePython)
  Dunit = g/cm3
  Dvalue = 0.68376
  Group = -> [C_element052,H_element046]
  conduct = 2
  density = 1
  expand = 3
  formula = G4_N-HEPTANE
  name = G4_N-HEPTANE
  specific = 4
FEATURE [App::DocumentObjectGroupPython] C_element053  label="C_element : 029"  # scripted group (container) (typed FeaturePython)
  n = 6
  ref = C_element
FEATURE [App::DocumentObjectGroupPython] H_element047  label="H_element : 14"  # scripted group (container) (typed FeaturePython)
  n = 14
  ref = H_element
FEATURE [App::DocumentObjectGroupPython] G4_N_HEXANE  label="G4_N-HEXANE"  # scripted group (container) (typed FeaturePython)
  Dunit = g/cm3
  Dvalue = 0.6603
  Group = -> [C_element053,H_element047]
  conduct = 2
  density = 1
  expand = 3
  formula = G4_N-HEXANE
  name = G4_N-HEXANE
  specific = 4
FEATURE [App::DocumentObjectGroupPython] C_element054  label="C_element : 22"  # scripted group (container) (typed FeaturePython)
  n = 22
  ref = C_element
FEATURE [App::DocumentObjectGroupPython] H_element048  label="H_element : 025"  # scripted group (container) (typed FeaturePython)
  n = 10
  ref = H_element
FEATURE [App::DocumentObjectGroupPython] N_element021  label="N_element : 010"  # scripted group (container) (typed FeaturePython)
  n = 2
  ref = N_element
FEATURE [App::DocumentObjectGroupPython] O_element050  label="O_element : 025"  # scripted group (container) (typed FeaturePython)
  n = 5
  ref = O_element
FEATURE [App::DocumentObjectGroupPython] G4_KAPTON  # scripted group (container) (typed FeaturePython)
  Dunit = g/cm3
  Dvalue = 1.42
  Group = -> [C_element054,H_element048,N_element021,O_element050]
  conduct = 2
  density = 1
  expand = 3
  formula = G4_KAPTON
  name = G4_KAPTON
  specific = 4
FEATURE [App::DocumentObjectGroupPython] La_element001  label="La_element : 1"  # scripted group (container) (typed FeaturePython)
  n = 1
  ref = La_element
FEATURE [App::DocumentObjectGroupPython] Br_element003  label="Br_element : 002"  # scripted group (container) (typed FeaturePython)
  n = 1
  ref = Br_element
FEATURE [App::DocumentObjectGroupPython] O_element051  label="O_element : 026"  # scripted group (container) (typed FeaturePython)
  n = 1
  ref = O_element
FEATURE [App::DocumentObjectGroupPython] G4_LANTHANUM_OXYBROMIDE  # scripted group (container) (typed FeaturePython)
  Dunit = g/cm3
  Dvalue = 6.28
  Group = -> [La_element001,Br_element003,O_element051]
  conduct = 2
  density = 1
  expand = 3
  formula = G4_LANTHANUM_OXYBROMIDE
  name = G4_LANTHANUM_OXYBROMIDE
  specific = 4
FEATURE [App::DocumentObjectGroupPython] La_element002  label="La_element : 2"  # scripted group (container) (typed FeaturePython)
  n = 2
  ref = La_element
FEATURE [App::DocumentObjectGroupPython] O_element052  label="O_element : 027"  # scripted group (container) (typed FeaturePython)
  n = 2
  ref = O_element
FEATURE [App::DocumentObjectGroupPython] S_element015  label="S_element : 006"  # scripted group (container) (typed FeaturePython)
  n = 1
  ref = S_element
FEATURE [App::DocumentObjectGroupPython] G4_LANTHANUM_OXYSULFIDE  # scripted group (container) (typed FeaturePython)
  Dunit = g/cm3
  Dvalue = 5.86
  Group = -> [La_element002,O_element052,S_element015]
  conduct = 2
  density = 1
  expand = 3
  formula = G4_LANTHANUM_OXYSULFIDE
  name = G4_LANTHANUM_OXYSULFIDE
  specific = 4
FEATURE [App::DocumentObjectGroupPython] O_element053  label="O_element : 0.072"  # scripted group (container) (typed FeaturePython)
  n = 0.071682
FEATURE [App::DocumentObjectGroupPython] Pb_element002  label="Pb_element : 0.928"  # scripted group (container) (typed FeaturePython)
  n = 0.928318
FEATURE [App::DocumentObjectGroupPython] G4_LEAD_OXIDE  # scripted group (container) (typed FeaturePython)
  Dunit = g/cm3
  Dvalue = 9.53
  Group = -> [O_element053,Pb_element002]
  conduct = 2
  density = 1
  expand = 3
  formula = G4_LEAD_OXIDE
  name = G4_LEAD_OXIDE
  specific = 4
FEATURE [App::DocumentObjectGroupPython] Li_element001  label="Li_element : 1"  # scripted group (container) (typed FeaturePython)
  n = 1
  ref = Li_element
FEATURE [App::DocumentObjectGroupPython] N_element022  label="N_element : 011"  # scripted group (container) (typed FeaturePython)
  n = 1
  ref = N_element
FEATURE [App::DocumentObjectGroupPython] H_element049  label="H_element : 026"  # scripted group (container) (typed FeaturePython)
  n = 2
  ref = H_element
FEATURE [App::DocumentObjectGroupPython] G4_LITHIUM_AMIDE  # scripted group (container) (typed FeaturePython)
  Dunit = g/cm3
  Dvalue = 1.178
  Group = -> [Li_element001,N_element022,H_element049]
  conduct = 2
  density = 1
  expand = 3
  formula = G4_LITHIUM_AMIDE
  name = G4_LITHIUM_AMIDE
  specific = 4
FEATURE [App::DocumentObjectGroupPython] Li_element002  label="Li_element : 2"  # scripted group (container) (typed FeaturePython)
  n = 2
  ref = Li_element
FEATURE [App::DocumentObjectGroupPython] C_element055  label="C_element : 030"  # scripted group (container) (typed FeaturePython)
  n = 1
  ref = C_element
FEATURE [App::DocumentObjectGroupPython] O_element054  label="O_element : 028"  # scripted group (container) (typed FeaturePython)
  n = 3
  ref = O_element
FEATURE [App::DocumentObjectGroupPython] G4_LITHIUM_CARBONATE  # scripted group (container) (typed FeaturePython)
  Dunit = g/cm3
  Dvalue = 2.11
  Group = -> [Li_element002,C_element055,O_element054]
  conduct = 2
  density = 1
  expand = 3
  formula = G4_LITHIUM_CARBONATE
  name = G4_LITHIUM_CARBONATE
  specific = 4
FEATURE [App::DocumentObjectGroupPython] Li_element003  label="Li_element : 003"  # scripted group (container) (typed FeaturePython)
  n = 1
  ref = Li_element
FEATURE [App::DocumentObjectGroupPython] F_element012  label="F_element : 004"  # scripted group (container) (typed FeaturePython)
  n = 1
  ref = F_element
FEATURE [App::DocumentObjectGroupPython] G4_LITHIUM_FLUORIDE  # scripted group (container) (typed FeaturePython)
  Dunit = g/cm3
  Dvalue = 2.635
  Group = -> [Li_element003,F_element012]
  conduct = 2
  density = 1
  expand = 3
  formula = G4_LITHIUM_FLUORIDE
  name = G4_LITHIUM_FLUORIDE
  specific = 4
FEATURE [App::DocumentObjectGroupPython] Li_element004  label="Li_element : 004"  # scripted group (container) (typed FeaturePython)
  n = 1
  ref = Li_element
FEATURE [App::DocumentObjectGroupPython] H_element050  label="H_element : 027"  # scripted group (container) (typed FeaturePython)
  n = 1
  ref = H_element
FEATURE [App::DocumentObjectGroupPython] G4_LITHIUM_HYDRIDE  # scripted group (container) (typed FeaturePython)
  Dunit = g/cm3
  Dvalue = 0.82
  Group = -> [Li_element004,H_element050]
  conduct = 2
  density = 1
  expand = 3
  formula = G4_LITHIUM_HYDRIDE
  name = G4_LITHIUM_HYDRIDE
  specific = 4
FEATURE [App::DocumentObjectGroupPython] Li_element005  label="Li_element : 005"  # scripted group (container) (typed FeaturePython)
  n = 1
  ref = Li_element
FEATURE [App::DocumentObjectGroupPython] I_element003  label="I_element : 002"  # scripted group (container) (typed FeaturePython)
  n = 1
  ref = I_element
FEATURE [App::DocumentObjectGroupPython] G4_LITHIUM_IODIDE  # scripted group (container) (typed FeaturePython)
  Dunit = g/cm3
  Dvalue = 3.494
  Group = -> [Li_element005,I_element003]
  conduct = 2
  density = 1
  expand = 3
  formula = G4_LITHIUM_IODIDE
  name = G4_LITHIUM_IODIDE
  specific = 4
FEATURE [App::DocumentObjectGroupPython] Li_element006  label="Li_element : 006"  # scripted group (container) (typed FeaturePython)
  n = 2
  ref = Li_element
FEATURE [App::DocumentObjectGroupPython] O_element055  label="O_element : 029"  # scripted group (container) (typed FeaturePython)
  n = 1
  ref = O_element
FEATURE [App::DocumentObjectGroupPython] G4_LITHIUM_OXIDE  # scripted group (container) (typed FeaturePython)
  Dunit = g/cm3
  Dvalue = 2.013
  Group = -> [Li_element006,O_element055]
  conduct = 2
  density = 1
  expand = 3
  formula = G4_LITHIUM_OXIDE
  name = G4_LITHIUM_OXIDE
  specific = 4
FEATURE [App::DocumentObjectGroupPython] Li_element007  label="Li_element : 007"  # scripted group (container) (typed FeaturePython)
  n = 2
  ref = Li_element
FEATURE [App::DocumentObjectGroupPython] B_element005  label="B_element : 005"  # scripted group (container) (typed FeaturePython)
  n = 4
  ref = B_element
FEATURE [App::DocumentObjectGroupPython] O_element056  label="O_element : 7"  # scripted group (container) (typed FeaturePython)
  n = 7
  ref = O_element
FEATURE [App::DocumentObjectGroupPython] G4_LITHIUM_TETRABORATE  # scripted group (container) (typed FeaturePython)
  Dunit = g/cm3
  Dvalue = 2.44
  Group = -> [Li_element007,B_element005,O_element056]
  conduct = 2
  density = 1
  expand = 3
  formula = G4_LITHIUM_TETRABORATE
  name = G4_LITHIUM_TETRABORATE
  specific = 4
FEATURE [App::DocumentObjectGroupPython] H_element051  label="H_element : 0.105"  # scripted group (container) (typed FeaturePython)
  n = 0.105
FEATURE [App::DocumentObjectGroupPython] C_element056  label="C_element : 0.083"  # scripted group (container) (typed FeaturePython)
  n = 0.083
FEATURE [App::DocumentObjectGroupPython] N_element023  label="N_element : 0.023"  # scripted group (container) (typed FeaturePython)
  n = 0.023
FEATURE [App::DocumentObjectGroupPython] O_element057  label="O_element : 0.779"  # scripted group (container) (typed FeaturePython)
  n = 0.779
FEATURE [App::DocumentObjectGroupPython] Na_element010  label="Na_element : 0.097"  # scripted group (container) (typed FeaturePython)
  n = 0.002
FEATURE [App::DocumentObjectGroupPython] P_element006  label="P_element : 0.105"  # scripted group (container) (typed FeaturePython)
  n = 0.001
FEATURE [App::DocumentObjectGroupPython] S_element016  label="S_element : 0.017"  # scripted group (container) (typed FeaturePython)
  n = 0.002
FEATURE [App::DocumentObjectGroupPython] Cl_element014  label="Cl_element : 0.587"  # scripted group (container) (typed FeaturePython)
  n = 0.003
FEATURE [App::DocumentObjectGroupPython] K_element005  label="K_element : 0.015"  # scripted group (container) (typed FeaturePython)
  n = 0.002
FEATURE [App::DocumentObjectGroupPython] G4_LUNG_ICRP  # scripted group (container) (typed FeaturePython)
  Dunit = g/cm3
  Dvalue = 1.04
  Group = -> [H_element051,C_element056,N_element023,O_element057,Na_element010,P_element006,S_element016,Cl_element014,K_element005]
  conduct = 2
  density = 1
  expand = 3
  formula = G4_LUNG_ICRP
  name = G4_LUNG_ICRP
  specific = 4
FEATURE [App::DocumentObjectGroupPython] H_element052  label="H_element : 0.116"  # scripted group (container) (typed FeaturePython)
  n = 0.114318
FEATURE [App::DocumentObjectGroupPython] C_element057  label="C_element : 0.656"  # scripted group (container) (typed FeaturePython)
  n = 0.655824
FEATURE [App::DocumentObjectGroupPython] O_element058  label="O_element : 0.092"  # scripted group (container) (typed FeaturePython)
  n = 0.0921831
FEATURE [App::DocumentObjectGroupPython] Mg_element004  label="Mg_element : 0.135"  # scripted group (container) (typed FeaturePython)
  n = 0.134792
FEATURE [App::DocumentObjectGroupPython] Ca_element013  label="Ca_element : 0.003"  # scripted group (container) (typed FeaturePython)
  n = 0.002883
FEATURE [App::DocumentObjectGroupPython] G4_M3_WAX  # scripted group (container) (typed FeaturePython)
  Dunit = g/cm3
  Dvalue = 1.05
  Group = -> [H_element052,C_element057,O_element058,Mg_element004,Ca_element013]
  conduct = 2
  density = 1
  expand = 3
  formula = G4_M3_WAX
  name = G4_M3_WAX
  specific = 4
FEATURE [App::DocumentObjectGroupPython] Mg_element005  label="Mg_element : 1"  # scripted group (container) (typed FeaturePython)
  n = 1
  ref = Mg_element
FEATURE [App::DocumentObjectGroupPython] C_element058  label="C_element : 031"  # scripted group (container) (typed FeaturePython)
  n = 1
  ref = C_element
FEATURE [App::DocumentObjectGroupPython] O_element059  label="O_element : 030"  # scripted group (container) (typed FeaturePython)
  n = 3
  ref = O_element
FEATURE [App::DocumentObjectGroupPython] G4_MAGNESIUM_CARBONATE  # scripted group (container) (typed FeaturePython)
  Dunit = g/cm3
  Dvalue = 2.958
  Group = -> [Mg_element005,C_element058,O_element059]
  conduct = 2
  density = 1
  expand = 3
  formula = G4_MAGNESIUM_CARBONATE
  name = G4_MAGNESIUM_CARBONATE
  specific = 4
FEATURE [App::DocumentObjectGroupPython] Mg_element006  label="Mg_element : 002"  # scripted group (container) (typed FeaturePython)
  n = 1
  ref = Mg_element
FEATURE [App::DocumentObjectGroupPython] F_element013  label="F_element : 005"  # scripted group (container) (typed FeaturePython)
  n = 2
  ref = F_element
FEATURE [App::DocumentObjectGroupPython] G4_MAGNESIUM_FLUORIDE  # scripted group (container) (typed FeaturePython)
  Dunit = g/cm3
  Dvalue = 3
  Group = -> [Mg_element006,F_element013]
  conduct = 2
  density = 1
  expand = 3
  formula = G4_MAGNESIUM_FLUORIDE
  name = G4_MAGNESIUM_FLUORIDE
  specific = 4
FEATURE [App::DocumentObjectGroupPython] Mg_element007  label="Mg_element : 003"  # scripted group (container) (typed FeaturePython)
  n = 1
  ref = Mg_element
FEATURE [App::DocumentObjectGroupPython] O_element060  label="O_element : 031"  # scripted group (container) (typed FeaturePython)
  n = 1
  ref = O_element
FEATURE [App::DocumentObjectGroupPython] G4_MAGNESIUM_OXIDE  # scripted group (container) (typed FeaturePython)
  Dunit = g/cm3
  Dvalue = 3.58
  Group = -> [Mg_element007,O_element060]
  conduct = 2
  density = 1
  expand = 3
  formula = G4_MAGNESIUM_OXIDE
  name = G4_MAGNESIUM_OXIDE
  specific = 4
FEATURE [App::DocumentObjectGroupPython] Mg_element008  label="Mg_element : 004"  # scripted group (container) (typed FeaturePython)
  n = 1
  ref = Mg_element
FEATURE [App::DocumentObjectGroupPython] B_element006  label="B_element : 006"  # scripted group (container) (typed FeaturePython)
  n = 4
  ref = B_element
FEATURE [App::DocumentObjectGroupPython] O_element061  label="O_element : 032"  # scripted group (container) (typed FeaturePython)
  n = 7
  ref = O_element
FEATURE [App::DocumentObjectGroupPython] G4_MAGNESIUM_TETRABORATE  # scripted group (container) (typed FeaturePython)
  Dunit = g/cm3
  Dvalue = 2.53
  Group = -> [Mg_element008,B_element006,O_element061]
  conduct = 2
  density = 1
  expand = 3
  formula = G4_MAGNESIUM_TETRABORATE
  name = G4_MAGNESIUM_TETRABORATE
  specific = 4
FEATURE [App::DocumentObjectGroupPython] Hg_element001  label="Hg_element : 1"  # scripted group (container) (typed FeaturePython)
  n = 1
  ref = Hg_element
FEATURE [App::DocumentObjectGroupPython] I_element004  label="I_element : 2"  # scripted group (container) (typed FeaturePython)
  n = 2
  ref = I_element
FEATURE [App::DocumentObjectGroupPython] G4_MERCURIC_IODIDE  # scripted group (container) (typed FeaturePython)
  Dunit = g/cm3
  Dvalue = 6.36
  Group = -> [Hg_element001,I_element004]
  conduct = 2
  density = 1
  expand = 3
  formula = G4_MERCURIC_IODIDE
  name = G4_MERCURIC_IODIDE
  specific = 4
FEATURE [App::DocumentObjectGroupPython] C_element059  label="C_element : 032"  # scripted group (container) (typed FeaturePython)
  n = 1
  ref = C_element
FEATURE [App::DocumentObjectGroupPython] H_element053  label="H_element : 028"  # scripted group (container) (typed FeaturePython)
  n = 4
  ref = H_element
FEATURE [App::DocumentObjectGroupPython] G4_METHANE  # scripted group (container) (typed FeaturePython)
  Dunit = g/cm3
  Dvalue = 0.000667151
  Group = -> [C_element059,H_element053]
  conduct = 2
  density = 1
  expand = 3
  formula = G4_METHANE
  name = G4_METHANE
  specific = 4
FEATURE [App::DocumentObjectGroupPython] C_element060  label="C_element : 033"  # scripted group (container) (typed FeaturePython)
  n = 1
  ref = C_element
FEATURE [App::DocumentObjectGroupPython] H_element054  label="H_element : 029"  # scripted group (container) (typed FeaturePython)
  n = 4
  ref = H_element
FEATURE [App::DocumentObjectGroupPython] O_element062  label="O_element : 033"  # scripted group (container) (typed FeaturePython)
  n = 1
  ref = O_element
FEATURE [App::DocumentObjectGroupPython] G4_METHANOL  # scripted group (container) (typed FeaturePython)
  Dunit = g/cm3
  Dvalue = 0.7914
  Group = -> [C_element060,H_element054,O_element062]
  conduct = 2
  density = 1
  expand = 3
  formula = G4_METHANOL
  name = G4_METHANOL
  specific = 4
FEATURE [App::DocumentObjectGroupPython] H_element055  label="H_element : 0.134"  # scripted group (container) (typed FeaturePython)
  n = 0.13404
FEATURE [App::DocumentObjectGroupPython] C_element061  label="C_element : 0.778"  # scripted group (container) (typed FeaturePython)
  n = 0.77796
FEATURE [App::DocumentObjectGroupPython] O_element063  label="O_element : 0.035"  # scripted group (container) (typed FeaturePython)
  n = 0.03502
FEATURE [App::DocumentObjectGroupPython] Mg_element009  label="Mg_element : 0.039"  # scripted group (container) (typed FeaturePython)
  n = 0.038594
FEATURE [App::DocumentObjectGroupPython] Ti_element002  label="Ti_element : 0.014"  # scripted group (container) (typed FeaturePython)
  n = 0.014386
FEATURE [App::DocumentObjectGroupPython] G4_MIX_D_WAX  # scripted group (container) (typed FeaturePython)
  Dunit = g/cm3
  Dvalue = 0.99
  Group = -> [H_element055,C_element061,O_element063,Mg_element009,Ti_element002]
  conduct = 2
  density = 1
  expand = 3
  formula = G4_MIX_D_WAX
  name = G4_MIX_D_WAX
  specific = 4
FEATURE [App::DocumentObjectGroupPython] H_element056  label="H_element : 0.135"  # scripted group (container) (typed FeaturePython)
  n = 0.081192
FEATURE [App::DocumentObjectGroupPython] C_element062  label="C_element : 0.583"  # scripted group (container) (typed FeaturePython)
  n = 0.583442
FEATURE [App::DocumentObjectGroupPython] N_element024  label="N_element : 0.018"  # scripted group (container) (typed FeaturePython)
  n = 0.017798
FEATURE [App::DocumentObjectGroupPython] O_element064  label="O_element : 0.186"  # scripted group (container) (typed FeaturePython)
  n = 0.186381
FEATURE [App::DocumentObjectGroupPython] Mg_element010  label="Mg_element : 0.130"  # scripted group (container) (typed FeaturePython)
  n = 0.130287
FEATURE [App::DocumentObjectGroupPython] Cl_element015  label="Cl_element : 0.588"  # scripted group (container) (typed FeaturePython)
  n = 0.0009
FEATURE [App::DocumentObjectGroupPython] G4_MS20_TISSUE  # scripted group (container) (typed FeaturePython)
  Dunit = g/cm3
  Dvalue = 1
  Group = -> [H_element056,C_element062,N_element024,O_element064,Mg_element010,Cl_element015]
  conduct = 2
  density = 1
  expand = 3
  formula = G4_MS20_TISSUE
  name = G4_MS20_TISSUE
  specific = 4
FEATURE [App::DocumentObjectGroupPython] H_element057  label="H_element : 0.136"  # scripted group (container) (typed FeaturePython)
  n = 0.102
FEATURE [App::DocumentObjectGroupPython] C_element063  label="C_element : 0.143"  # scripted group (container) (typed FeaturePython)
  n = 0.143
FEATURE [App::DocumentObjectGroupPython] N_element025  label="N_element : 0.034"  # scripted group (container) (typed FeaturePython)
  n = 0.034
FEATURE [App::DocumentObjectGroupPython] O_element065  label="O_element : 0.710"  # scripted group (container) (typed FeaturePython)
  n = 0.71
FEATURE [App::DocumentObjectGroupPython] Na_element011  label="Na_element : 0.098"  # scripted group (container) (typed FeaturePython)
  n = 0.001
FEATURE [App::DocumentObjectGroupPython] P_element007  label="P_element : 0.002"  # scripted group (container) (typed FeaturePython)
  n = 0.002
FEATURE [App::DocumentObjectGroupPython] S_element017  label="S_element : 0.018"  # scripted group (container) (typed FeaturePython)
  n = 0.003
FEATURE [App::DocumentObjectGroupPython] Cl_element016  label="Cl_element : 0.589"  # scripted group (container) (typed FeaturePython)
  n = 0.001
FEATURE [App::DocumentObjectGroupPython] K_element006  label="K_element : 0.004"  # scripted group (container) (typed FeaturePython)
  n = 0.004
FEATURE [App::DocumentObjectGroupPython] G4_MUSCLE_SKELETAL_ICRP  # scripted group (container) (typed FeaturePython)
  Dunit = g/cm3
  Dvalue = 1.05
  Group = -> [H_element057,C_element063,N_element025,O_element065,Na_element011,P_element007,S_element017,Cl_element016,K_element006]
  conduct = 2
  density = 1
  expand = 3
  formula = G4_MUSCLE_SKELETAL_ICRP
  name = G4_MUSCLE_SKELETAL_ICRP
  specific = 4
FEATURE [App::DocumentObjectGroupPython] H_element058  label="H_element : 0.137"  # scripted group (container) (typed FeaturePython)
  n = 0.102102
FEATURE [App::DocumentObjectGroupPython] C_element064  label="C_element : 0.123"  # scripted group (container) (typed FeaturePython)
  n = 0.123123
FEATURE [App::DocumentObjectGroupPython] N_element026  label="N_element : 0.756"  # scripted group (container) (typed FeaturePython)
  n = 0.035035
FEATURE [App::DocumentObjectGroupPython] O_element066  label="O_element : 0.730"  # scripted group (container) (typed FeaturePython)
  n = 0.72973
FEATURE [App::DocumentObjectGroupPython] Na_element012  label="Na_element : 0.099"  # scripted group (container) (typed FeaturePython)
  n = 0.001001
FEATURE [App::DocumentObjectGroupPython] P_element008  label="P_element : 0.106"  # scripted group (container) (typed FeaturePython)
  n = 0.002002
FEATURE [App::DocumentObjectGroupPython] S_element018  label="S_element : 0.019"  # scripted group (container) (typed FeaturePython)
  n = 0.004004
FEATURE [App::DocumentObjectGroupPython] K_element007  label="K_element : 0.016"  # scripted group (container) (typed FeaturePython)
  n = 0.003003
FEATURE [App::DocumentObjectGroupPython] G4_MUSCLE_STRIATED_ICRU  # scripted group (container) (typed FeaturePython)
  Dunit = g/cm3
  Dvalue = 1.04
  Group = -> [H_element058,C_element064,N_element026,O_element066,Na_element012,P_element008,S_element018,K_element007]
  conduct = 2
  density = 1
  expand = 3
  formula = G4_MUSCLE_STRIATED_ICRU
  name = G4_MUSCLE_STRIATED_ICRU
  specific = 4
FEATURE [App::DocumentObjectGroupPython] H_element059  label="H_element : 0.098"  # scripted group (container) (typed FeaturePython)
  n = 0.0982341
FEATURE [App::DocumentObjectGroupPython] C_element065  label="C_element : 0.156"  # scripted group (container) (typed FeaturePython)
  n = 0.156214
FEATURE [App::DocumentObjectGroupPython] N_element027  label="N_element : 0.757"  # scripted group (container) (typed FeaturePython)
  n = 0.035451
FEATURE [App::DocumentObjectGroupPython] O_element067  label="O_element : 0.880"  # scripted group (container) (typed FeaturePython)
  n = 0.710101
FEATURE [App::DocumentObjectGroupPython] G4_MUSCLE_WITH_SUCROSE  # scripted group (container) (typed FeaturePython)
  Dunit = g/cm3
  Dvalue = 1.11
  Group = -> [H_element059,C_element065,N_element027,O_element067]
  conduct = 2
  density = 1
  expand = 3
  formula = G4_MUSCLE_WITH_SUCROSE
  name = G4_MUSCLE_WITH_SUCROSE
  specific = 4
FEATURE [App::DocumentObjectGroupPython] H_element060  label="H_element : 0.138"  # scripted group (container) (typed FeaturePython)
  n = 0.101969
FEATURE [App::DocumentObjectGroupPython] C_element066  label="C_element : 0.120"  # scripted group (container) (typed FeaturePython)
  n = 0.120058
FEATURE [App::DocumentObjectGroupPython] N_element028  label="N_element : 0.758"  # scripted group (container) (typed FeaturePython)
  n = 0.035451
FEATURE [App::DocumentObjectGroupPython] O_element068  label="O_element : 0.743"  # scripted group (container) (typed FeaturePython)
  n = 0.742522
FEATURE [App::DocumentObjectGroupPython] G4_MUSCLE_WITHOUT_SUCROSE  # scripted group (container) (typed FeaturePython)
  Dunit = g/cm3
  Dvalue = 1.07
  Group = -> [H_element060,C_element066,N_element028,O_element068]
  conduct = 2
  density = 1
  expand = 3
  formula = G4_MUSCLE_WITHOUT_SUCROSE
  name = G4_MUSCLE_WITHOUT_SUCROSE
  specific = 4
FEATURE [App::DocumentObjectGroupPython] C_element067  label="C_element : 10"  # scripted group (container) (typed FeaturePython)
  n = 10
  ref = C_element
FEATURE [App::DocumentObjectGroupPython] H_element061  label="H_element : 030"  # scripted group (container) (typed FeaturePython)
  n = 8
  ref = H_element
FEATURE [App::DocumentObjectGroupPython] G4_NAPHTHALENE  # scripted group (container) (typed FeaturePython)
  Dunit = g/cm3
  Dvalue = 1.145
  Group = -> [C_element067,H_element061]
  conduct = 2
  density = 1
  expand = 3
  formula = G4_NAPHTHALENE
  name = G4_NAPHTHALENE
  specific = 4
FEATURE [App::DocumentObjectGroupPython] C_element068  label="C_element : 034"  # scripted group (container) (typed FeaturePython)
  n = 6
  ref = C_element
FEATURE [App::DocumentObjectGroupPython] H_element062  label="H_element : 031"  # scripted group (container) (typed FeaturePython)
  n = 5
  ref = H_element
FEATURE [App::DocumentObjectGroupPython] N_element029  label="N_element : 012"  # scripted group (container) (typed FeaturePython)
  n = 1
  ref = N_element
FEATURE [App::DocumentObjectGroupPython] O_element069  label="O_element : 034"  # scripted group (container) (typed FeaturePython)
  n = 2
  ref = O_element
FEATURE [App::DocumentObjectGroupPython] G4_NITROBENZENE  # scripted group (container) (typed FeaturePython)
  Dunit = g/cm3
  Dvalue = 1.19867
  Group = -> [C_element068,H_element062,N_element029,O_element069]
  conduct = 2
  density = 1
  expand = 3
  formula = G4_NITROBENZENE
  name = G4_NITROBENZENE
  specific = 4
FEATURE [App::DocumentObjectGroupPython] N_element030  label="N_element : 013"  # scripted group (container) (typed FeaturePython)
  n = 2
  ref = N_element
FEATURE [App::DocumentObjectGroupPython] O_element070  label="O_element : 035"  # scripted group (container) (typed FeaturePython)
  n = 1
  ref = O_element
FEATURE [App::DocumentObjectGroupPython] G4_NITROUS_OXIDE  # scripted group (container) (typed FeaturePython)
  Dunit = g/cm3
  Dvalue = 0.00183094
  Group = -> [N_element030,O_element070]
  conduct = 2
  density = 1
  expand = 3
  formula = G4_NITROUS_OXIDE
  name = G4_NITROUS_OXIDE
  specific = 4
FEATURE [App::DocumentObjectGroupPython] H_element063  label="H_element : 0.104"  # scripted group (container) (typed FeaturePython)
  n = 0.103509
FEATURE [App::DocumentObjectGroupPython] C_element069  label="C_element : 0.648"  # scripted group (container) (typed FeaturePython)
  n = 0.648416
FEATURE [App::DocumentObjectGroupPython] N_element031  label="N_element : 0.100"  # scripted group (container) (typed FeaturePython)
  n = 0.0995361
FEATURE [App::DocumentObjectGroupPython] O_element071  label="O_element : 0.149"  # scripted group (container) (typed FeaturePython)
  n = 0.148539
FEATURE [App::DocumentObjectGroupPython] G4_NYLON_8062  label="G4_NYLON-8062"  # scripted group (container) (typed FeaturePython)
  Dunit = g/cm3
  Dvalue = 1.08
  Group = -> [H_element063,C_element069,N_element031,O_element071]
  conduct = 2
  density = 1
  expand = 3
  formula = G4_NYLON-8062
  name = G4_NYLON-8062
  specific = 4
FEATURE [App::DocumentObjectGroupPython] C_element070  label="C_element : 035"  # scripted group (container) (typed FeaturePython)
  n = 6
  ref = C_element
FEATURE [App::DocumentObjectGroupPython] H_element064  label="H_element : 11"  # scripted group (container) (typed FeaturePython)
  n = 11
  ref = H_element
FEATURE [App::DocumentObjectGroupPython] N_element032  label="N_element : 014"  # scripted group (container) (typed FeaturePython)
  n = 1
  ref = N_element
FEATURE [App::DocumentObjectGroupPython] O_element072  label="O_element : 036"  # scripted group (container) (typed FeaturePython)
  n = 1
  ref = O_element
FEATURE [App::DocumentObjectGroupPython] G4_NYLON_6_6  label="G4_NYLON-6-6"  # scripted group (container) (typed FeaturePython)
  Dunit = g/cm3
  Dvalue = 1.14
  Group = -> [C_element070,H_element064,N_element032,O_element072]
  conduct = 2
  density = 1
  expand = 3
  formula = G4_NYLON-6-6
  name = G4_NYLON-6-6
  specific = 4
FEATURE [App::DocumentObjectGroupPython] H_element065  label="H_element : 0.139"  # scripted group (container) (typed FeaturePython)
  n = 0.107062
FEATURE [App::DocumentObjectGroupPython] C_element071  label="C_element : 0.680"  # scripted group (container) (typed FeaturePython)
  n = 0.680449
FEATURE [App::DocumentObjectGroupPython] N_element033  label="N_element : 0.099"  # scripted group (container) (typed FeaturePython)
  n = 0.099189
FEATURE [App::DocumentObjectGroupPython] O_element073  label="O_element : 0.113"  # scripted group (container) (typed FeaturePython)
  n = 0.1133
FEATURE [App::DocumentObjectGroupPython] G4_NYLON_6_10  label="G4_NYLON-6-10"  # scripted group (container) (typed FeaturePython)
  Dunit = g/cm3
  Dvalue = 1.14
  Group = -> [H_element065,C_element071,N_element033,O_element073]
  conduct = 2
  density = 1
  expand = 3
  formula = G4_NYLON-6-10
  name = G4_NYLON-6-10
  specific = 4
FEATURE [App::DocumentObjectGroupPython] H_element066  label="H_element : 0.140"  # scripted group (container) (typed FeaturePython)
  n = 0.115476
FEATURE [App::DocumentObjectGroupPython] C_element072  label="C_element : 0.721"  # scripted group (container) (typed FeaturePython)
  n = 0.720818
FEATURE [App::DocumentObjectGroupPython] N_element034  label="N_element : 0.076"  # scripted group (container) (typed FeaturePython)
  n = 0.0764169
FEATURE [App::DocumentObjectGroupPython] O_element074  label="O_element : 0.087"  # scripted group (container) (typed FeaturePython)
  n = 0.0872889
FEATURE [App::DocumentObjectGroupPython] G4_NYLON_11_RILSAN  label="G4_NYLON-11_RILSAN"  # scripted group (container) (typed FeaturePython)
  Dunit = g/cm3
  Dvalue = 1.425
  Group = -> [H_element066,C_element072,N_element034,O_element074]
  conduct = 2
  density = 1
  expand = 3
  formula = G4_NYLON-11_RILSAN
  name = G4_NYLON-11_RILSAN
  specific = 4
FEATURE [App::DocumentObjectGroupPython] C_element073  label="C_element : 8"  # scripted group (container) (typed FeaturePython)
  n = 8
  ref = C_element
FEATURE [App::DocumentObjectGroupPython] H_element067  label="H_element : 18"  # scripted group (container) (typed FeaturePython)
  n = 18
  ref = H_element
FEATURE [App::DocumentObjectGroupPython] G4_OCTANE  # scripted group (container) (typed FeaturePython)
  Dunit = g/cm3
  Dvalue = 0.7026
  Group = -> [C_element073,H_element067]
  conduct = 2
  density = 1
  expand = 3
  formula = G4_OCTANE
  name = G4_OCTANE
  specific = 4
FEATURE [App::DocumentObjectGroupPython] C_element074  label="C_element : 25"  # scripted group (container) (typed FeaturePython)
  n = 25
  ref = C_element
FEATURE [App::DocumentObjectGroupPython] H_element068  label="H_element : 52"  # scripted group (container) (typed FeaturePython)
  n = 52
  ref = H_element
FEATURE [App::DocumentObjectGroupPython] G4_PARAFFIN  # scripted group (container) (typed FeaturePython)
  Dunit = g/cm3
  Dvalue = 0.93
  Group = -> [C_element074,H_element068]
  conduct = 2
  density = 1
  expand = 3
  formula = G4_PARAFFIN
  name = G4_PARAFFIN
  specific = 4
FEATURE [App::DocumentObjectGroupPython] C_element075  label="C_element : 036"  # scripted group (container) (typed FeaturePython)
  n = 5
  ref = C_element
FEATURE [App::DocumentObjectGroupPython] H_element069  label="H_element : 032"  # scripted group (container) (typed FeaturePython)
  n = 12
  ref = H_element
FEATURE [App::DocumentObjectGroupPython] G4_N_PENTANE  label="G4_N-PENTANE"  # scripted group (container) (typed FeaturePython)
  Dunit = g/cm3
  Dvalue = 0.6262
  Group = -> [C_element075,H_element069]
  conduct = 2
  density = 1
  expand = 3
  formula = G4_N-PENTANE
  name = G4_N-PENTANE
  specific = 4
FEATURE [App::DocumentObjectGroupPython] H_element070  label="H_element : 0.014"  # scripted group (container) (typed FeaturePython)
  n = 0.0141
FEATURE [App::DocumentObjectGroupPython] C_element076  label="C_element : 0.072"  # scripted group (container) (typed FeaturePython)
  n = 0.072261
FEATURE [App::DocumentObjectGroupPython] N_element035  label="N_element : 0.019"  # scripted group (container) (typed FeaturePython)
  n = 0.01932
FEATURE [App::DocumentObjectGroupPython] O_element075  label="O_element : 0.066"  # scripted group (container) (typed FeaturePython)
  n = 0.066101
FEATURE [App::DocumentObjectGroupPython] S_element019  label="S_element : 0.020"  # scripted group (container) (typed FeaturePython)
  n = 0.00189
FEATURE [App::DocumentObjectGroupPython] Br_element004  label="Br_element : 0.349"  # scripted group (container) (typed FeaturePython)
  n = 0.349103
FEATURE [App::DocumentObjectGroupPython] Ag_element001  label="Ag_element : 0.474"  # scripted group (container) (typed FeaturePython)
  n = 0.474105
FEATURE [App::DocumentObjectGroupPython] I_element005  label="I_element : 0.003"  # scripted group (container) (typed FeaturePython)
  n = 0.00312
FEATURE [App::DocumentObjectGroupPython] G4_PHOTO_EMULSION  # scripted group (container) (typed FeaturePython)
  Dunit = g/cm3
  Dvalue = 3.815
  Group = -> [H_element070,C_element076,N_element035,O_element075,S_element019,Br_element004,Ag_element001,I_element005]
  conduct = 2
  density = 1
  expand = 3
  formula = G4_PHOTO_EMULSION
  name = G4_PHOTO_EMULSION
  specific = 4
FEATURE [App::DocumentObjectGroupPython] C_element077  label="C_element : 9"  # scripted group (container) (typed FeaturePython)
  n = 9
  ref = C_element
FEATURE [App::DocumentObjectGroupPython] H_element071  label="H_element : 033"  # scripted group (container) (typed FeaturePython)
  n = 10
  ref = H_element
FEATURE [App::DocumentObjectGroupPython] G4_PLASTIC_SC_VINYLTOLUENE  # scripted group (container) (typed FeaturePython)
  Dunit = g/cm3
  Dvalue = 1.032
  Group = -> [C_element077,H_element071]
  conduct = 2
  density = 1
  expand = 3
  formula = G4_PLASTIC_SC_VINYLTOLUENE
  name = G4_PLASTIC_SC_VINYLTOLUENE
  specific = 4
FEATURE [App::DocumentObjectGroupPython] Pu_element001  label="Pu_element : 1"  # scripted group (container) (typed FeaturePython)
  n = 1
  ref = Pu_element
FEATURE [App::DocumentObjectGroupPython] O_element076  label="O_element : 037"  # scripted group (container) (typed FeaturePython)
  n = 2
  ref = O_element
FEATURE [App::DocumentObjectGroupPython] G4_PLUTONIUM_DIOXIDE  # scripted group (container) (typed FeaturePython)
  Dunit = g/cm3
  Dvalue = 11.46
  Group = -> [Pu_element001,O_element076]
  conduct = 2
  density = 1
  expand = 3
  formula = G4_PLUTONIUM_DIOXIDE
  name = G4_PLUTONIUM_DIOXIDE
  specific = 4
FEATURE [App::DocumentObjectGroupPython] C_element078  label="C_element : 037"  # scripted group (container) (typed FeaturePython)
  n = 3
  ref = C_element
FEATURE [App::DocumentObjectGroupPython] H_element072  label="H_element : 034"  # scripted group (container) (typed FeaturePython)
  n = 3
  ref = H_element
FEATURE [App::DocumentObjectGroupPython] N_element036  label="N_element : 015"  # scripted group (container) (typed FeaturePython)
  n = 1
  ref = N_element
FEATURE [App::DocumentObjectGroupPython] G4_POLYACRYLONITRILE  # scripted group (container) (typed FeaturePython)
  Dunit = g/cm3
  Dvalue = 1.17
  Group = -> [C_element078,H_element072,N_element036]
  conduct = 2
  density = 1
  expand = 3
  formula = G4_POLYACRYLONITRILE
  name = G4_POLYACRYLONITRILE
  specific = 4
FEATURE [App::DocumentObjectGroupPython] C_element079  label="C_element : 16"  # scripted group (container) (typed FeaturePython)
  n = 16
  ref = C_element
FEATURE [App::DocumentObjectGroupPython] H_element073  label="H_element : 035"  # scripted group (container) (typed FeaturePython)
  n = 14
  ref = H_element
FEATURE [App::DocumentObjectGroupPython] O_element077  label="O_element : 038"  # scripted group (container) (typed FeaturePython)
  n = 3
  ref = O_element
FEATURE [App::DocumentObjectGroupPython] G4_POLYCARBONATE  # scripted group (container) (typed FeaturePython)
  Dunit = g/cm3
  Dvalue = 1.2
  Group = -> [C_element079,H_element073,O_element077]
  conduct = 2
  density = 1
  expand = 3
  formula = G4_POLYCARBONATE
  name = G4_POLYCARBONATE
  specific = 4
FEATURE [App::DocumentObjectGroupPython] C_element080  label="C_element : 038"  # scripted group (container) (typed FeaturePython)
  n = 8
  ref = C_element
FEATURE [App::DocumentObjectGroupPython] H_element074  label="H_element : 036"  # scripted group (container) (typed FeaturePython)
  n = 7
  ref = H_element
FEATURE [App::DocumentObjectGroupPython] Cl_element017  label="Cl_element : 007"  # scripted group (container) (typed FeaturePython)
  n = 1
  ref = Cl_element
FEATURE [App::DocumentObjectGroupPython] G4_POLYCHLOROSTYRENE  # scripted group (container) (typed FeaturePython)
  Dunit = g/cm3
  Dvalue = 1.3
  Group = -> [C_element080,H_element074,Cl_element017]
  conduct = 2
  density = 1
  expand = 3
  formula = G4_POLYCHLOROSTYRENE
  name = G4_POLYCHLOROSTYRENE
  specific = 4
FEATURE [App::DocumentObjectGroupPython] C_element081  label="C_element : 039"  # scripted group (container) (typed FeaturePython)
  n = 1
  ref = C_element
FEATURE [App::DocumentObjectGroupPython] H_element075  label="H_element : 037"  # scripted group (container) (typed FeaturePython)
  n = 2
  ref = H_element
FEATURE [App::DocumentObjectGroupPython] G4_POLYETHYLENE  # scripted group (container) (typed FeaturePython)
  Dunit = g/cm3
  Dvalue = 0.94
  Group = -> [C_element081,H_element075]
  conduct = 2
  density = 1
  expand = 3
  formula = G4_POLYETHYLENE
  name = G4_POLYETHYLENE
  specific = 4
FEATURE [App::DocumentObjectGroupPython] C_element082  label="C_element : 040"  # scripted group (container) (typed FeaturePython)
  n = 10
  ref = C_element
FEATURE [App::DocumentObjectGroupPython] H_element076  label="H_element : 038"  # scripted group (container) (typed FeaturePython)
  n = 8
  ref = H_element
FEATURE [App::DocumentObjectGroupPython] O_element078  label="O_element : 039"  # scripted group (container) (typed FeaturePython)
  n = 4
  ref = O_element
FEATURE [App::DocumentObjectGroupPython] G4_MYLAR  # scripted group (container) (typed FeaturePython)
  Dunit = g/cm3
  Dvalue = 1.4
  Group = -> [C_element082,H_element076,O_element078]
  conduct = 2
  density = 1
  expand = 3
  formula = G4_MYLAR
  name = G4_MYLAR
  specific = 4
FEATURE [App::DocumentObjectGroupPython] C_element083  label="C_element : 041"  # scripted group (container) (typed FeaturePython)
  n = 5
  ref = C_element
FEATURE [App::DocumentObjectGroupPython] H_element077  label="H_element : 039"  # scripted group (container) (typed FeaturePython)
  n = 8
  ref = H_element
FEATURE [App::DocumentObjectGroupPython] O_element079  label="O_element : 040"  # scripted group (container) (typed FeaturePython)
  n = 2
  ref = O_element
FEATURE [App::DocumentObjectGroupPython] G4_PLEXIGLASS  # scripted group (container) (typed FeaturePython)
  Dunit = g/cm3
  Dvalue = 1.19
  Group = -> [C_element083,H_element077,O_element079]
  conduct = 2
  density = 1
  expand = 3
  formula = G4_PLEXIGLASS
  name = G4_PLEXIGLASS
  specific = 4
FEATURE [App::DocumentObjectGroupPython] C_element084  label="C_element : 042"  # scripted group (container) (typed FeaturePython)
  n = 1
  ref = C_element
FEATURE [App::DocumentObjectGroupPython] H_element078  label="H_element : 040"  # scripted group (container) (typed FeaturePython)
  n = 2
  ref = H_element
FEATURE [App::DocumentObjectGroupPython] O_element080  label="O_element : 041"  # scripted group (container) (typed FeaturePython)
  n = 1
  ref = O_element
FEATURE [App::DocumentObjectGroupPython] G4_POLYOXYMETHYLENE  # scripted group (container) (typed FeaturePython)
  Dunit = g/cm3
  Dvalue = 1.425
  Group = -> [C_element084,H_element078,O_element080]
  conduct = 2
  density = 1
  expand = 3
  formula = G4_POLYOXYMETHYLENE
  name = G4_POLYOXYMETHYLENE
  specific = 4
FEATURE [App::DocumentObjectGroupPython] C_element085  label="C_element : 043"  # scripted group (container) (typed FeaturePython)
  n = 2
  ref = C_element
FEATURE [App::DocumentObjectGroupPython] H_element079  label="H_element : 041"  # scripted group (container) (typed FeaturePython)
  n = 4
  ref = H_element
FEATURE [App::DocumentObjectGroupPython] G4_POLYPROPYLENE  # scripted group (container) (typed FeaturePython)
  Dunit = g/cm3
  Dvalue = 0.9
  Group = -> [C_element085,H_element079]
  conduct = 2
  density = 1
  expand = 3
  formula = G4_POLYPROPYLENE
  name = G4_POLYPROPYLENE
  specific = 4
FEATURE [App::DocumentObjectGroupPython] C_element086  label="C_element : 044"  # scripted group (container) (typed FeaturePython)
  n = 8
  ref = C_element
FEATURE [App::DocumentObjectGroupPython] H_element080  label="H_element : 042"  # scripted group (container) (typed FeaturePython)
  n = 8
  ref = H_element
FEATURE [App::DocumentObjectGroupPython] G4_POLYSTYRENE  # scripted group (container) (typed FeaturePython)
  Dunit = g/cm3
  Dvalue = 1.06
  Group = -> [C_element086,H_element080]
  conduct = 2
  density = 1
  expand = 3
  formula = G4_POLYSTYRENE
  name = G4_POLYSTYRENE
  specific = 4
FEATURE [App::DocumentObjectGroupPython] C_element087  label="C_element : 045"  # scripted group (container) (typed FeaturePython)
  n = 2
  ref = C_element
FEATURE [App::DocumentObjectGroupPython] F_element014  label="F_element : 4"  # scripted group (container) (typed FeaturePython)
  n = 4
  ref = F_element
FEATURE [App::DocumentObjectGroupPython] G4_TEFLON  # scripted group (container) (typed FeaturePython)
  Dunit = g/cm3
  Dvalue = 2.2
  Group = -> [C_element087,F_element014]
  conduct = 2
  density = 1
  expand = 3
  formula = G4_TEFLON
  name = G4_TEFLON
  specific = 4
FEATURE [App::DocumentObjectGroupPython] C_element088  label="C_element : 046"  # scripted group (container) (typed FeaturePython)
  n = 2
  ref = C_element
FEATURE [App::DocumentObjectGroupPython] F_element015  label="F_element : 006"  # scripted group (container) (typed FeaturePython)
  n = 3
  ref = F_element
FEATURE [App::DocumentObjectGroupPython] Cl_element018  label="Cl_element : 008"  # scripted group (container) (typed FeaturePython)
  n = 1
  ref = Cl_element
FEATURE [App::DocumentObjectGroupPython] G4_POLYTRIFLUOROCHLOROETHYLENE  # scripted group (container) (typed FeaturePython)
  Dunit = g/cm3
  Dvalue = 2.1
  Group = -> [C_element088,F_element015,Cl_element018]
  conduct = 2
  density = 1
  expand = 3
  formula = G4_POLYTRIFLUOROCHLOROETHYLENE
  name = G4_POLYTRIFLUOROCHLOROETHYLENE
  specific = 4
FEATURE [App::DocumentObjectGroupPython] C_element089  label="C_element : 047"  # scripted group (container) (typed FeaturePython)
  n = 4
  ref = C_element
FEATURE [App::DocumentObjectGroupPython] H_element081  label="H_element : 043"  # scripted group (container) (typed FeaturePython)
  n = 6
  ref = H_element
FEATURE [App::DocumentObjectGroupPython] O_element081  label="O_element : 042"  # scripted group (container) (typed FeaturePython)
  n = 2
  ref = O_element
FEATURE [App::DocumentObjectGroupPython] G4_POLYVINYL_ACETATE  # scripted group (container) (typed FeaturePython)
  Dunit = g/cm3
  Dvalue = 1.19
  Group = -> [C_element089,H_element081,O_element081]
  conduct = 2
  density = 1
  expand = 3
  formula = G4_POLYVINYL_ACETATE
  name = G4_POLYVINYL_ACETATE
  specific = 4
FEATURE [App::DocumentObjectGroupPython] C_element090  label="C_element : 048"  # scripted group (container) (typed FeaturePython)
  n = 2
  ref = C_element
FEATURE [App::DocumentObjectGroupPython] H_element082  label="H_element : 044"  # scripted group (container) (typed FeaturePython)
  n = 4
  ref = H_element
FEATURE [App::DocumentObjectGroupPython] O_element082  label="O_element : 043"  # scripted group (container) (typed FeaturePython)
  n = 1
  ref = O_element
FEATURE [App::DocumentObjectGroupPython] G4_POLYVINYL_ALCOHOL  # scripted group (container) (typed FeaturePython)
  Dunit = g/cm3
  Dvalue = 1.3
  Group = -> [C_element090,H_element082,O_element082]
  conduct = 2
  density = 1
  expand = 3
  formula = G4_POLYVINYL_ALCOHOL
  name = G4_POLYVINYL_ALCOHOL
  specific = 4
FEATURE [App::DocumentObjectGroupPython] C_element091  label="C_element : 049"  # scripted group (container) (typed FeaturePython)
  n = 8
  ref = C_element
FEATURE [App::DocumentObjectGroupPython] H_element083  label="H_element : 045"  # scripted group (container) (typed FeaturePython)
  n = 14
  ref = H_element
FEATURE [App::DocumentObjectGroupPython] O_element083  label="O_element : 044"  # scripted group (container) (typed FeaturePython)
  n = 2
  ref = O_element
FEATURE [App::DocumentObjectGroupPython] G4_POLYVINYL_BUTYRAL  # scripted group (container) (typed FeaturePython)
  Dunit = g/cm3
  Dvalue = 1.12
  Group = -> [C_element091,H_element083,O_element083]
  conduct = 2
  density = 1
  expand = 3
  formula = G4_POLYVINYL_BUTYRAL
  name = G4_POLYVINYL_BUTYRAL
  specific = 4
FEATURE [App::DocumentObjectGroupPython] C_element092  label="C_element : 050"  # scripted group (container) (typed FeaturePython)
  n = 2
  ref = C_element
FEATURE [App::DocumentObjectGroupPython] H_element084  label="H_element : 046"  # scripted group (container) (typed FeaturePython)
  n = 3
  ref = H_element
FEATURE [App::DocumentObjectGroupPython] Cl_element019  label="Cl_element : 009"  # scripted group (container) (typed FeaturePython)
  n = 1
  ref = Cl_element
FEATURE [App::DocumentObjectGroupPython] G4_POLYVINYL_CHLORIDE  # scripted group (container) (typed FeaturePython)
  Dunit = g/cm3
  Dvalue = 1.3
  Group = -> [C_element092,H_element084,Cl_element019]
  conduct = 2
  density = 1
  expand = 3
  formula = G4_POLYVINYL_CHLORIDE
  name = G4_POLYVINYL_CHLORIDE
  specific = 4
FEATURE [App::DocumentObjectGroupPython] C_element093  label="C_element : 051"  # scripted group (container) (typed FeaturePython)
  n = 2
  ref = C_element
FEATURE [App::DocumentObjectGroupPython] H_element085  label="H_element : 047"  # scripted group (container) (typed FeaturePython)
  n = 2
  ref = H_element
FEATURE [App::DocumentObjectGroupPython] Cl_element020  label="Cl_element : 010"  # scripted group (container) (typed FeaturePython)
  n = 2
  ref = Cl_element
FEATURE [App::DocumentObjectGroupPython] G4_POLYVINYLIDENE_CHLORIDE  # scripted group (container) (typed FeaturePython)
  Dunit = g/cm3
  Dvalue = 1.7
  Group = -> [C_element093,H_element085,Cl_element020]
  conduct = 2
  density = 1
  expand = 3
  formula = G4_POLYVINYLIDENE_CHLORIDE
  name = G4_POLYVINYLIDENE_CHLORIDE
  specific = 4
FEATURE [App::DocumentObjectGroupPython] C_element094  label="C_element : 052"  # scripted group (container) (typed FeaturePython)
  n = 2
  ref = C_element
FEATURE [App::DocumentObjectGroupPython] H_element086  label="H_element : 048"  # scripted group (container) (typed FeaturePython)
  n = 2
  ref = H_element
FEATURE [App::DocumentObjectGroupPython] F_element016  label="F_element : 007"  # scripted group (container) (typed FeaturePython)
  n = 2
  ref = F_element
FEATURE [App::DocumentObjectGroupPython] G4_POLYVINYLIDENE_FLUORIDE  # scripted group (container) (typed FeaturePython)
  Dunit = g/cm3
  Dvalue = 1.76
  Group = -> [C_element094,H_element086,F_element016]
  conduct = 2
  density = 1
  expand = 3
  formula = G4_POLYVINYLIDENE_FLUORIDE
  name = G4_POLYVINYLIDENE_FLUORIDE
  specific = 4
FEATURE [App::DocumentObjectGroupPython] C_element095  label="C_element : 053"  # scripted group (container) (typed FeaturePython)
  n = 6
  ref = C_element
FEATURE [App::DocumentObjectGroupPython] H_element087  label="H_element : 9"  # scripted group (container) (typed FeaturePython)
  n = 9
  ref = H_element
FEATURE [App::DocumentObjectGroupPython] N_element037  label="N_element : 016"  # scripted group (container) (typed FeaturePython)
  n = 1
  ref = N_element
FEATURE [App::DocumentObjectGroupPython] O_element084  label="O_element : 045"  # scripted group (container) (typed FeaturePython)
  n = 1
  ref = O_element
FEATURE [App::DocumentObjectGroupPython] G4_POLYVINYL_PYRROLIDONE  # scripted group (container) (typed FeaturePython)
  Dunit = g/cm3
  Dvalue = 1.25
  Group = -> [C_element095,H_element087,N_element037,O_element084]
  conduct = 2
  density = 1
  expand = 3
  formula = G4_POLYVINYL_PYRROLIDONE
  name = G4_POLYVINYL_PYRROLIDONE
  specific = 4
FEATURE [App::DocumentObjectGroupPython] K_element008  label="K_element : 1"  # scripted group (container) (typed FeaturePython)
  n = 1
  ref = K_element
FEATURE [App::DocumentObjectGroupPython] I_element006  label="I_element : 003"  # scripted group (container) (typed FeaturePython)
  n = 1
  ref = I_element
FEATURE [App::DocumentObjectGroupPython] G4_POTASSIUM_IODIDE  # scripted group (container) (typed FeaturePython)
  Dunit = g/cm3
  Dvalue = 3.13
  Group = -> [K_element008,I_element006]
  conduct = 2
  density = 1
  expand = 3
  formula = G4_POTASSIUM_IODIDE
  name = G4_POTASSIUM_IODIDE
  specific = 4
FEATURE [App::DocumentObjectGroupPython] K_element009  label="K_element : 2"  # scripted group (container) (typed FeaturePython)
  n = 2
  ref = K_element
FEATURE [App::DocumentObjectGroupPython] O_element085  label="O_element : 046"  # scripted group (container) (typed FeaturePython)
  n = 1
  ref = O_element
FEATURE [App::DocumentObjectGroupPython] G4_POTASSIUM_OXIDE  # scripted group (container) (typed FeaturePython)
  Dunit = g/cm3
  Dvalue = 2.32
  Group = -> [K_element009,O_element085]
  conduct = 2
  density = 1
  expand = 3
  formula = G4_POTASSIUM_OXIDE
  name = G4_POTASSIUM_OXIDE
  specific = 4
FEATURE [App::DocumentObjectGroupPython] C_element096  label="C_element : 054"  # scripted group (container) (typed FeaturePython)
  n = 3
  ref = C_element
FEATURE [App::DocumentObjectGroupPython] H_element088  label="H_element : 049"  # scripted group (container) (typed FeaturePython)
  n = 8
  ref = H_element
FEATURE [App::DocumentObjectGroupPython] G4_PROPANE  # scripted group (container) (typed FeaturePython)
  Dunit = g/cm3
  Dvalue = 0.00187939
  Group = -> [C_element096,H_element088]
  conduct = 2
  density = 1
  expand = 3
  formula = G4_PROPANE
  name = G4_PROPANE
  specific = 4
FEATURE [App::DocumentObjectGroupPython] C_element097  label="C_element : 055"  # scripted group (container) (typed FeaturePython)
  n = 3
  ref = C_element
FEATURE [App::DocumentObjectGroupPython] H_element089  label="H_element : 050"  # scripted group (container) (typed FeaturePython)
  n = 8
  ref = H_element
FEATURE [App::DocumentObjectGroupPython] G4_lPROPANE  # scripted group (container) (typed FeaturePython)
  Dunit = g/cm3
  Dvalue = 0.43
  Group = -> [C_element097,H_element089]
  conduct = 2
  density = 1
  expand = 3
  formula = G4_lPROPANE
  name = G4_lPROPANE
  specific = 4
FEATURE [App::DocumentObjectGroupPython] C_element098  label="C_element : 056"  # scripted group (container) (typed FeaturePython)
  n = 3
  ref = C_element
FEATURE [App::DocumentObjectGroupPython] H_element090  label="H_element : 051"  # scripted group (container) (typed FeaturePython)
  n = 8
  ref = H_element
FEATURE [App::DocumentObjectGroupPython] O_element086  label="O_element : 047"  # scripted group (container) (typed FeaturePython)
  n = 1
  ref = O_element
FEATURE [App::DocumentObjectGroupPython] G4_N_PROPYL_ALCOHOL  label="G4_N-PROPYL_ALCOHOL"  # scripted group (container) (typed FeaturePython)
  Dunit = g/cm3
  Dvalue = 0.8035
  Group = -> [C_element098,H_element090,O_element086]
  conduct = 2
  density = 1
  expand = 3
  formula = G4_N-PROPYL_ALCOHOL
  name = G4_N-PROPYL_ALCOHOL
  specific = 4
FEATURE [App::DocumentObjectGroupPython] C_element099  label="C_element : 057"  # scripted group (container) (typed FeaturePython)
  n = 5
  ref = C_element
FEATURE [App::DocumentObjectGroupPython] H_element091  label="H_element : 052"  # scripted group (container) (typed FeaturePython)
  n = 5
  ref = H_element
FEATURE [App::DocumentObjectGroupPython] N_element038  label="N_element : 017"  # scripted group (container) (typed FeaturePython)
  n = 1
  ref = N_element
FEATURE [App::DocumentObjectGroupPython] G4_PYRIDINE  # scripted group (container) (typed FeaturePython)
  Dunit = g/cm3
  Dvalue = 0.9819
  Group = -> [C_element099,H_element091,N_element038]
  conduct = 2
  density = 1
  expand = 3
  formula = G4_PYRIDINE
  name = G4_PYRIDINE
  specific = 4
FEATURE [App::DocumentObjectGroupPython] H_element092  label="H_element : 0.144"  # scripted group (container) (typed FeaturePython)
  n = 0.143711
FEATURE [App::DocumentObjectGroupPython] C_element100  label="C_element : 0.856"  # scripted group (container) (typed FeaturePython)
  n = 0.856289
FEATURE [App::DocumentObjectGroupPython] G4_RUBBER_BUTYL  # scripted group (container) (typed FeaturePython)
  Dunit = g/cm3
  Dvalue = 0.92
  Group = -> [H_element092,C_element100]
  conduct = 2
  density = 1
  expand = 3
  formula = G4_RUBBER_BUTYL
  name = G4_RUBBER_BUTYL
  specific = 4
FEATURE [App::DocumentObjectGroupPython] H_element093  label="H_element : 0.118"  # scripted group (container) (typed FeaturePython)
  n = 0.118371
FEATURE [App::DocumentObjectGroupPython] C_element101  label="C_element : 0.882"  # scripted group (container) (typed FeaturePython)
  n = 0.881629
FEATURE [App::DocumentObjectGroupPython] G4_RUBBER_NATURAL  # scripted group (container) (typed FeaturePython)
  Dunit = g/cm3
  Dvalue = 0.92
  Group = -> [H_element093,C_element101]
  conduct = 2
  density = 1
  expand = 3
  formula = G4_RUBBER_NATURAL
  name = G4_RUBBER_NATURAL
  specific = 4
FEATURE [App::DocumentObjectGroupPython] H_element094  label="H_element : 0.145"  # scripted group (container) (typed FeaturePython)
  n = 0.05692
FEATURE [App::DocumentObjectGroupPython] C_element102  label="C_element : 0.543"  # scripted group (container) (typed FeaturePython)
  n = 0.542646
FEATURE [App::DocumentObjectGroupPython] Cl_element021  label="Cl_element : 0.400"  # scripted group (container) (typed FeaturePython)
  n = 0.400434
FEATURE [App::DocumentObjectGroupPython] G4_RUBBER_NEOPRENE  # scripted group (container) (typed FeaturePython)
  Dunit = g/cm3
  Dvalue = 1.23
  Group = -> [H_element094,C_element102,Cl_element021]
  conduct = 2
  density = 1
  expand = 3
  formula = G4_RUBBER_NEOPRENE
  name = G4_RUBBER_NEOPRENE
  specific = 4
FEATURE [App::DocumentObjectGroupPython] Si_element006  label="Si_element : 1"  # scripted group (container) (typed FeaturePython)
  n = 1
  ref = Si_element
FEATURE [App::DocumentObjectGroupPython] O_element087  label="O_element : 048"  # scripted group (container) (typed FeaturePython)
  n = 2
  ref = O_element
FEATURE [App::DocumentObjectGroupPython] G4_SILICON_DIOXIDE  # scripted group (container) (typed FeaturePython)
  Dunit = g/cm3
  Dvalue = 2.32
  Group = -> [Si_element006,O_element087]
  conduct = 2
  density = 1
  expand = 3
  formula = G4_SILICON_DIOXIDE
  name = G4_SILICON_DIOXIDE
  specific = 4
FEATURE [App::DocumentObjectGroupPython] Ag_element002  label="Ag_element : 1"  # scripted group (container) (typed FeaturePython)
  n = 1
  ref = Ag_element
FEATURE [App::DocumentObjectGroupPython] Br_element005  label="Br_element : 003"  # scripted group (container) (typed FeaturePython)
  n = 1
  ref = Br_element
FEATURE [App::DocumentObjectGroupPython] G4_SILVER_BROMIDE  # scripted group (container) (typed FeaturePython)
  Dunit = g/cm3
  Dvalue = 6.473
  Group = -> [Ag_element002,Br_element005]
  conduct = 2
  density = 1
  expand = 3
  formula = G4_SILVER_BROMIDE
  name = G4_SILVER_BROMIDE
  specific = 4
FEATURE [App::DocumentObjectGroupPython] Ag_element003  label="Ag_element : 002"  # scripted group (container) (typed FeaturePython)
  n = 1
  ref = Ag_element
FEATURE [App::DocumentObjectGroupPython] Cl_element022  label="Cl_element : 011"  # scripted group (container) (typed FeaturePython)
  n = 1
  ref = Cl_element
FEATURE [App::DocumentObjectGroupPython] G4_SILVER_CHLORIDE  # scripted group (container) (typed FeaturePython)
  Dunit = g/cm3
  Dvalue = 5.56
  Group = -> [Ag_element003,Cl_element022]
  conduct = 2
  density = 1
  expand = 3
  formula = G4_SILVER_CHLORIDE
  name = G4_SILVER_CHLORIDE
  specific = 4
FEATURE [App::DocumentObjectGroupPython] Br_element006  label="Br_element : 0.423"  # scripted group (container) (typed FeaturePython)
  n = 0.422895
FEATURE [App::DocumentObjectGroupPython] Ag_element004  label="Ag_element : 0.574"  # scripted group (container) (typed FeaturePython)
  n = 0.573748
FEATURE [App::DocumentObjectGroupPython] I_element007  label="I_element : 0.649"  # scripted group (container) (typed FeaturePython)
  n = 0.003357
FEATURE [App::DocumentObjectGroupPython] G4_SILVER_HALIDES  # scripted group (container) (typed FeaturePython)
  Dunit = g/cm3
  Dvalue = 6.47
  Group = -> [Br_element006,Ag_element004,I_element007]
  conduct = 2
  density = 1
  expand = 3
  formula = G4_SILVER_HALIDES
  name = G4_SILVER_HALIDES
  specific = 4
FEATURE [App::DocumentObjectGroupPython] Ag_element005  label="Ag_element : 003"  # scripted group (container) (typed FeaturePython)
  n = 1
  ref = Ag_element
FEATURE [App::DocumentObjectGroupPython] I_element008  label="I_element : 004"  # scripted group (container) (typed FeaturePython)
  n = 1
  ref = I_element
FEATURE [App::DocumentObjectGroupPython] G4_SILVER_IODIDE  # scripted group (container) (typed FeaturePython)
  Dunit = g/cm3
  Dvalue = 6.01
  Group = -> [Ag_element005,I_element008]
  conduct = 2
  density = 1
  expand = 3
  formula = G4_SILVER_IODIDE
  name = G4_SILVER_IODIDE
  specific = 4
FEATURE [App::DocumentObjectGroupPython] H_element095  label="H_element : 0.100"  # scripted group (container) (typed FeaturePython)
  n = 0.1
FEATURE [App::DocumentObjectGroupPython] C_element103  label="C_element : 0.204"  # scripted group (container) (typed FeaturePython)
  n = 0.204
FEATURE [App::DocumentObjectGroupPython] N_element039  label="N_element : 0.759"  # scripted group (container) (typed FeaturePython)
  n = 0.042
FEATURE [App::DocumentObjectGroupPython] O_element088  label="O_element : 0.645"  # scripted group (container) (typed FeaturePython)
  n = 0.645
FEATURE [App::DocumentObjectGroupPython] Na_element013  label="Na_element : 0.100"  # scripted group (container) (typed FeaturePython)
  n = 0.002
FEATURE [App::DocumentObjectGroupPython] P_element009  label="P_element : 0.107"  # scripted group (container) (typed FeaturePython)
  n = 0.001
FEATURE [App::DocumentObjectGroupPython] S_element020  label="S_element : 0.021"  # scripted group (container) (typed FeaturePython)
  n = 0.002
FEATURE [App::DocumentObjectGroupPython] Cl_element023  label="Cl_element : 0.590"  # scripted group (container) (typed FeaturePython)
  n = 0.003
FEATURE [App::DocumentObjectGroupPython] K_element010  label="K_element : 0.001"  # scripted group (container) (typed FeaturePython)
  n = 0.001
FEATURE [App::DocumentObjectGroupPython] G4_SKIN_ICRP  # scripted group (container) (typed FeaturePython)
  Dunit = g/cm3
  Dvalue = 1.09
  Group = -> [H_element095,C_element103,N_element039,O_element088,Na_element013,P_element009,S_element020,Cl_element023,K_element010]
  conduct = 2
  density = 1
  expand = 3
  formula = G4_SKIN_ICRP
  name = G4_SKIN_ICRP
  specific = 4
FEATURE [App::DocumentObjectGroupPython] Na_element014  label="Na_element : 2"  # scripted group (container) (typed FeaturePython)
  n = 2
  ref = Na_element
FEATURE [App::DocumentObjectGroupPython] C_element104  label="C_element : 058"  # scripted group (container) (typed FeaturePython)
  n = 1
  ref = C_element
FEATURE [App::DocumentObjectGroupPython] O_element089  label="O_element : 049"  # scripted group (container) (typed FeaturePython)
  n = 3
  ref = O_element
FEATURE [App::DocumentObjectGroupPython] G4_SODIUM_CARBONATE  # scripted group (container) (typed FeaturePython)
  Dunit = g/cm3
  Dvalue = 2.532
  Group = -> [Na_element014,C_element104,O_element089]
  conduct = 2
  density = 1
  expand = 3
  formula = G4_SODIUM_CARBONATE
  name = G4_SODIUM_CARBONATE
  specific = 4
FEATURE [App::DocumentObjectGroupPython] Na_element015  label="Na_element : 1"  # scripted group (container) (typed FeaturePython)
  n = 1
  ref = Na_element
FEATURE [App::DocumentObjectGroupPython] I_element009  label="I_element : 005"  # scripted group (container) (typed FeaturePython)
  n = 1
  ref = I_element
FEATURE [App::DocumentObjectGroupPython] G4_SODIUM_IODIDE  # scripted group (container) (typed FeaturePython)
  Dunit = g/cm3
  Dvalue = 3.667
  Group = -> [Na_element015,I_element009]
  conduct = 2
  density = 1
  expand = 3
  formula = G4_SODIUM_IODIDE
  name = G4_SODIUM_IODIDE
  specific = 4
FEATURE [App::DocumentObjectGroupPython] Na_element016  label="Na_element : 003"  # scripted group (container) (typed FeaturePython)
  n = 2
  ref = Na_element
FEATURE [App::DocumentObjectGroupPython] O_element090  label="O_element : 050"  # scripted group (container) (typed FeaturePython)
  n = 1
  ref = O_element
FEATURE [App::DocumentObjectGroupPython] G4_SODIUM_MONOXIDE  # scripted group (container) (typed FeaturePython)
  Dunit = g/cm3
  Dvalue = 2.27
  Group = -> [Na_element016,O_element090]
  conduct = 2
  density = 1
  expand = 3
  formula = G4_SODIUM_MONOXIDE
  name = G4_SODIUM_MONOXIDE
  specific = 4
FEATURE [App::DocumentObjectGroupPython] Na_element017  label="Na_element : 004"  # scripted group (container) (typed FeaturePython)
  n = 1
  ref = Na_element
FEATURE [App::DocumentObjectGroupPython] N_element040  label="N_element : 018"  # scripted group (container) (typed FeaturePython)
  n = 1
  ref = N_element
FEATURE [App::DocumentObjectGroupPython] O_element091  label="O_element : 051"  # scripted group (container) (typed FeaturePython)
  n = 3
  ref = O_element
FEATURE [App::DocumentObjectGroupPython] G4_SODIUM_NITRATE  # scripted group (container) (typed FeaturePython)
  Dunit = g/cm3
  Dvalue = 2.261
  Group = -> [Na_element017,N_element040,O_element091]
  conduct = 2
  density = 1
  expand = 3
  formula = G4_SODIUM_NITRATE
  name = G4_SODIUM_NITRATE
  specific = 4
FEATURE [App::DocumentObjectGroupPython] C_element105  label="C_element : 059"  # scripted group (container) (typed FeaturePython)
  n = 14
  ref = C_element
FEATURE [App::DocumentObjectGroupPython] H_element096  label="H_element : 053"  # scripted group (container) (typed FeaturePython)
  n = 12
  ref = H_element
FEATURE [App::DocumentObjectGroupPython] G4_STILBENE  # scripted group (container) (typed FeaturePython)
  Dunit = g/cm3
  Dvalue = 0.9707
  Group = -> [C_element105,H_element096]
  conduct = 2
  density = 1
  expand = 3
  formula = G4_STILBENE
  name = G4_STILBENE
  specific = 4
FEATURE [App::DocumentObjectGroupPython] C_element106  label="C_element : 12"  # scripted group (container) (typed FeaturePython)
  n = 12
  ref = C_element
FEATURE [App::DocumentObjectGroupPython] H_element097  label="H_element : 22"  # scripted group (container) (typed FeaturePython)
  n = 22
  ref = H_element
FEATURE [App::DocumentObjectGroupPython] O_element092  label="O_element : 11"  # scripted group (container) (typed FeaturePython)
  n = 11
  ref = O_element
FEATURE [App::DocumentObjectGroupPython] G4_SUCROSE  # scripted group (container) (typed FeaturePython)
  Dunit = g/cm3
  Dvalue = 1.5805
  Group = -> [C_element106,H_element097,O_element092]
  conduct = 2
  density = 1
  expand = 3
  formula = G4_SUCROSE
  name = G4_SUCROSE
  specific = 4
FEATURE [App::DocumentObjectGroupPython] C_element107  label="C_element : 18"  # scripted group (container) (typed FeaturePython)
  n = 18
  ref = C_element
FEATURE [App::DocumentObjectGroupPython] H_element098  label="H_element : 054"  # scripted group (container) (typed FeaturePython)
  n = 14
  ref = H_element
FEATURE [App::DocumentObjectGroupPython] G4_TERPHENYL  # scripted group (container) (typed FeaturePython)
  Dunit = g/cm3
  Dvalue = 1.24
  Group = -> [C_element107,H_element098]
  conduct = 2
  density = 1
  expand = 3
  formula = G4_TERPHENYL
  name = G4_TERPHENYL
  specific = 4
FEATURE [App::DocumentObjectGroupPython] H_element099  label="H_element : 0.146"  # scripted group (container) (typed FeaturePython)
  n = 0.106
FEATURE [App::DocumentObjectGroupPython] C_element108  label="C_element : 0.883"  # scripted group (container) (typed FeaturePython)
  n = 0.099
FEATURE [App::DocumentObjectGroupPython] N_element041  label="N_element : 0.020"  # scripted group (container) (typed FeaturePython)
  n = 0.02
FEATURE [App::DocumentObjectGroupPython] O_element093  label="O_element : 0.766"  # scripted group (container) (typed FeaturePython)
  n = 0.766
FEATURE [App::DocumentObjectGroupPython] Na_element018  label="Na_element : 0.101"  # scripted group (container) (typed FeaturePython)
  n = 0.002
FEATURE [App::DocumentObjectGroupPython] P_element010  label="P_element : 0.108"  # scripted group (container) (typed FeaturePython)
  n = 0.001
FEATURE [App::DocumentObjectGroupPython] S_element021  label="S_element : 0.022"  # scripted group (container) (typed FeaturePython)
  n = 0.002
FEATURE [App::DocumentObjectGroupPython] Cl_element024  label="Cl_element : 0.002"  # scripted group (container) (typed FeaturePython)
  n = 0.002
FEATURE [App::DocumentObjectGroupPython] K_element011  label="K_element : 0.017"  # scripted group (container) (typed FeaturePython)
  n = 0.002
FEATURE [App::DocumentObjectGroupPython] G4_TESTIS_ICRP  # scripted group (container) (typed FeaturePython)
  Dunit = g/cm3
  Dvalue = 1.04
  Group = -> [H_element099,C_element108,N_element041,O_element093,Na_element018,P_element010,S_element021,Cl_element024,K_element011]
  conduct = 2
  density = 1
  expand = 3
  formula = G4_TESTIS_ICRP
  name = G4_TESTIS_ICRP
  specific = 4
FEATURE [App::DocumentObjectGroupPython] C_element109  label="C_element : 060"  # scripted group (container) (typed FeaturePython)
  n = 2
  ref = C_element
FEATURE [App::DocumentObjectGroupPython] Cl_element025  label="Cl_element : 012"  # scripted group (container) (typed FeaturePython)
  n = 4
  ref = Cl_element
FEATURE [App::DocumentObjectGroupPython] G4_TETRACHLOROETHYLENE  # scripted group (container) (typed FeaturePython)
  Dunit = g/cm3
  Dvalue = 1.625
  Group = -> [C_element109,Cl_element025]
  conduct = 2
  density = 1
  expand = 3
  formula = G4_TETRACHLOROETHYLENE
  name = G4_TETRACHLOROETHYLENE
  specific = 4
FEATURE [App::DocumentObjectGroupPython] Tl_element001  label="Tl_element : 1"  # scripted group (container) (typed FeaturePython)
  n = 1
  ref = Tl_element
FEATURE [App::DocumentObjectGroupPython] Cl_element026  label="Cl_element : 013"  # scripted group (container) (typed FeaturePython)
  n = 1
  ref = Cl_element
FEATURE [App::DocumentObjectGroupPython] G4_THALLIUM_CHLORIDE  # scripted group (container) (typed FeaturePython)
  Dunit = g/cm3
  Dvalue = 7.004
  Group = -> [Tl_element001,Cl_element026]
  conduct = 2
  density = 1
  expand = 3
  formula = G4_THALLIUM_CHLORIDE
  name = G4_THALLIUM_CHLORIDE
  specific = 4
FEATURE [App::DocumentObjectGroupPython] H_element100  label="H_element : 0.147"  # scripted group (container) (typed FeaturePython)
  n = 0.105
FEATURE [App::DocumentObjectGroupPython] C_element110  label="C_element : 0.256"  # scripted group (container) (typed FeaturePython)
  n = 0.256
FEATURE [App::DocumentObjectGroupPython] N_element042  label="N_element : 0.760"  # scripted group (container) (typed FeaturePython)
  n = 0.027
FEATURE [App::DocumentObjectGroupPython] O_element094  label="O_element : 0.602"  # scripted group (container) (typed FeaturePython)
  n = 0.602
FEATURE [App::DocumentObjectGroupPython] Na_element019  label="Na_element : 0.102"  # scripted group (container) (typed FeaturePython)
  n = 0.001
FEATURE [App::DocumentObjectGroupPython] P_element011  label="P_element : 0.109"  # scripted group (container) (typed FeaturePython)
  n = 0.002
FEATURE [App::DocumentObjectGroupPython] S_element022  label="S_element : 0.023"  # scripted group (container) (typed FeaturePython)
  n = 0.003
FEATURE [App::DocumentObjectGroupPython] Cl_element027  label="Cl_element : 0.591"  # scripted group (container) (typed FeaturePython)
  n = 0.002
FEATURE [App::DocumentObjectGroupPython] K_element012  label="K_element : 0.018"  # scripted group (container) (typed FeaturePython)
  n = 0.002
FEATURE [App::DocumentObjectGroupPython] G4_TISSUE_SOFT_ICRP  # scripted group (container) (typed FeaturePython)
  Dunit = g/cm3
  Dvalue = 1.03
  Group = -> [H_element100,C_element110,N_element042,O_element094,Na_element019,P_element011,S_element022,Cl_element027,K_element012]
  conduct = 2
  density = 1
  expand = 3
  formula = G4_TISSUE_SOFT_ICRP
  name = G4_TISSUE_SOFT_ICRP
  specific = 4
FEATURE [App::DocumentObjectGroupPython] H_element101  label="H_element : 0.148"  # scripted group (container) (typed FeaturePython)
  n = 0.101
FEATURE [App::DocumentObjectGroupPython] C_element111  label="C_element : 0.111"  # scripted group (container) (typed FeaturePython)
  n = 0.111
FEATURE [App::DocumentObjectGroupPython] N_element043  label="N_element : 0.026"  # scripted group (container) (typed FeaturePython)
  n = 0.026
FEATURE [App::DocumentObjectGroupPython] O_element095  label="O_element : 0.762"  # scripted group (container) (typed FeaturePython)
  n = 0.762
FEATURE [App::DocumentObjectGroupPython] G4_TISSUE_SOFT_ICRU_4  label="G4_TISSUE_SOFT_ICRU-4"  # scripted group (container) (typed FeaturePython)
  Dunit = g/cm3
  Dvalue = 1
  Group = -> [H_element101,C_element111,N_element043,O_element095]
  conduct = 2
  density = 1
  expand = 3
  formula = G4_TISSUE_SOFT_ICRU-4
  name = G4_TISSUE_SOFT_ICRU-4
  specific = 4
FEATURE [App::DocumentObjectGroupPython] H_element102  label="H_element : 0.149"  # scripted group (container) (typed FeaturePython)
  n = 0.101869
FEATURE [App::DocumentObjectGroupPython] C_element112  label="C_element : 0.456"  # scripted group (container) (typed FeaturePython)
  n = 0.456179
FEATURE [App::DocumentObjectGroupPython] N_element044  label="N_element : 0.761"  # scripted group (container) (typed FeaturePython)
  n = 0.035172
FEATURE [App::DocumentObjectGroupPython] O_element096  label="O_element : 0.407"  # scripted group (container) (typed FeaturePython)
  n = 0.40678
FEATURE [App::DocumentObjectGroupPython] G4_TISSUE_METHANE  label="G4_TISSUE-METHANE"  # scripted group (container) (typed FeaturePython)
  Dunit = g/cm3
  Dvalue = 0.00106409
  Group = -> [H_element102,C_element112,N_element044,O_element096]
  conduct = 2
  density = 1
  expand = 3
  formula = G4_TISSUE-METHANE
  name = G4_TISSUE-METHANE
  specific = 4
FEATURE [App::DocumentObjectGroupPython] H_element103  label="H_element : 0.103"  # scripted group (container) (typed FeaturePython)
  n = 0.102672
FEATURE [App::DocumentObjectGroupPython] C_element113  label="C_element : 0.569"  # scripted group (container) (typed FeaturePython)
  n = 0.56894
FEATURE [App::DocumentObjectGroupPython] N_element045  label="N_element : 0.762"  # scripted group (container) (typed FeaturePython)
  n = 0.035022
FEATURE [App::DocumentObjectGroupPython] O_element097  label="O_element : 0.293"  # scripted group (container) (typed FeaturePython)
  n = 0.293366
FEATURE [App::DocumentObjectGroupPython] G4_TISSUE_PROPANE  label="G4_TISSUE-PROPANE"  # scripted group (container) (typed FeaturePython)
  Dunit = g/cm3
  Dvalue = 0.00182628
  Group = -> [H_element103,C_element113,N_element045,O_element097]
  conduct = 2
  density = 1
  expand = 3
  formula = G4_TISSUE-PROPANE
  name = G4_TISSUE-PROPANE
  specific = 4
FEATURE [App::DocumentObjectGroupPython] Ti_element003  label="Ti_element : 1"  # scripted group (container) (typed FeaturePython)
  n = 1
  ref = Ti_element
FEATURE [App::DocumentObjectGroupPython] O_element098  label="O_element : 052"  # scripted group (container) (typed FeaturePython)
  n = 2
  ref = O_element
FEATURE [App::DocumentObjectGroupPython] G4_TITANIUM_DIOXIDE  # scripted group (container) (typed FeaturePython)
  Dunit = g/cm3
  Dvalue = 4.26
  Group = -> [Ti_element003,O_element098]
  conduct = 2
  density = 1
  expand = 3
  formula = G4_TITANIUM_DIOXIDE
  name = G4_TITANIUM_DIOXIDE
  specific = 4
FEATURE [App::DocumentObjectGroupPython] C_element114  label="C_element : 061"  # scripted group (container) (typed FeaturePython)
  n = 7
  ref = C_element
FEATURE [App::DocumentObjectGroupPython] H_element104  label="H_element : 055"  # scripted group (container) (typed FeaturePython)
  n = 8
  ref = H_element
FEATURE [App::DocumentObjectGroupPython] G4_TOLUENE  # scripted group (container) (typed FeaturePython)
  Dunit = g/cm3
  Dvalue = 0.8669
  Group = -> [C_element114,H_element104]
  conduct = 2
  density = 1
  expand = 3
  formula = G4_TOLUENE
  name = G4_TOLUENE
  specific = 4
FEATURE [App::DocumentObjectGroupPython] C_element115  label="C_element : 062"  # scripted group (container) (typed FeaturePython)
  n = 2
  ref = C_element
FEATURE [App::DocumentObjectGroupPython] H_element105  label="H_element : 056"  # scripted group (container) (typed FeaturePython)
  n = 1
  ref = H_element
FEATURE [App::DocumentObjectGroupPython] Cl_element028  label="Cl_element : 014"  # scripted group (container) (typed FeaturePython)
  n = 3
  ref = Cl_element
FEATURE [App::DocumentObjectGroupPython] G4_TRICHLOROETHYLENE  # scripted group (container) (typed FeaturePython)
  Dunit = g/cm3
  Dvalue = 1.46
  Group = -> [C_element115,H_element105,Cl_element028]
  conduct = 2
  density = 1
  expand = 3
  formula = G4_TRICHLOROETHYLENE
  name = G4_TRICHLOROETHYLENE
  specific = 4
FEATURE [App::DocumentObjectGroupPython] C_element116  label="C_element : 063"  # scripted group (container) (typed FeaturePython)
  n = 6
  ref = C_element
FEATURE [App::DocumentObjectGroupPython] H_element106  label="H_element : 15"  # scripted group (container) (typed FeaturePython)
  n = 15
  ref = H_element
FEATURE [App::DocumentObjectGroupPython] O_element099  label="O_element : 053"  # scripted group (container) (typed FeaturePython)
  n = 4
  ref = O_element
FEATURE [App::DocumentObjectGroupPython] P_element012  label="P_element : 1"  # scripted group (container) (typed FeaturePython)
  n = 1
  ref = P_element
FEATURE [App::DocumentObjectGroupPython] G4_TRIETHYL_PHOSPHATE  # scripted group (container) (typed FeaturePython)
  Dunit = g/cm3
  Dvalue = 1.07
  Group = -> [C_element116,H_element106,O_element099,P_element012]
  conduct = 2
  density = 1
  expand = 3
  formula = G4_TRIETHYL_PHOSPHATE
  name = G4_TRIETHYL_PHOSPHATE
  specific = 4
FEATURE [App::DocumentObjectGroupPython] W_element003  label="W_element : 003"  # scripted group (container) (typed FeaturePython)
  n = 1
  ref = W_element
FEATURE [App::DocumentObjectGroupPython] F_element017  label="F_element : 6"  # scripted group (container) (typed FeaturePython)
  n = 6
  ref = F_element
FEATURE [App::DocumentObjectGroupPython] G4_TUNGSTEN_HEXAFLUORIDE  # scripted group (container) (typed FeaturePython)
  Dunit = g/cm3
  Dvalue = 2.4
  Group = -> [W_element003,F_element017]
  conduct = 2
  density = 1
  expand = 3
  formula = G4_TUNGSTEN_HEXAFLUORIDE
  name = G4_TUNGSTEN_HEXAFLUORIDE
  specific = 4
FEATURE [App::DocumentObjectGroupPython] U_element001  label="U_element : 1"  # scripted group (container) (typed FeaturePython)
  n = 1
  ref = U_element
FEATURE [App::DocumentObjectGroupPython] C_element117  label="C_element : 064"  # scripted group (container) (typed FeaturePython)
  n = 2
  ref = C_element
FEATURE [App::DocumentObjectGroupPython] G4_URANIUM_DICARBIDE  # scripted group (container) (typed FeaturePython)
  Dunit = g/cm3
  Dvalue = 11.28
  Group = -> [U_element001,C_element117]
  conduct = 2
  density = 1
  expand = 3
  formula = G4_URANIUM_DICARBIDE
  name = G4_URANIUM_DICARBIDE
  specific = 4
FEATURE [App::DocumentObjectGroupPython] U_element002  label="U_element : 002"  # scripted group (container) (typed FeaturePython)
  n = 1
  ref = U_element
FEATURE [App::DocumentObjectGroupPython] C_element118  label="C_element : 065"  # scripted group (container) (typed FeaturePython)
  n = 1
  ref = C_element
FEATURE [App::DocumentObjectGroupPython] G4_URANIUM_MONOCARBIDE  # scripted group (container) (typed FeaturePython)
  Dunit = g/cm3
  Dvalue = 13.63
  Group = -> [U_element002,C_element118]
  conduct = 2
  density = 1
  expand = 3
  formula = G4_URANIUM_MONOCARBIDE
  name = G4_URANIUM_MONOCARBIDE
  specific = 4
FEATURE [App::DocumentObjectGroupPython] U_element003  label="U_element : 003"  # scripted group (container) (typed FeaturePython)
  n = 1
  ref = U_element
FEATURE [App::DocumentObjectGroupPython] O_element100  label="O_element : 054"  # scripted group (container) (typed FeaturePython)
  n = 2
  ref = O_element
FEATURE [App::DocumentObjectGroupPython] G4_URANIUM_OXIDE  # scripted group (container) (typed FeaturePython)
  Dunit = g/cm3
  Dvalue = 10.96
  Group = -> [U_element003,O_element100]
  conduct = 2
  density = 1
  expand = 3
  formula = G4_URANIUM_OXIDE
  name = G4_URANIUM_OXIDE
  specific = 4
FEATURE [App::DocumentObjectGroupPython] C_element119  label="C_element : 066"  # scripted group (container) (typed FeaturePython)
  n = 1
  ref = C_element
FEATURE [App::DocumentObjectGroupPython] H_element107  label="H_element : 057"  # scripted group (container) (typed FeaturePython)
  n = 4
  ref = H_element
FEATURE [App::DocumentObjectGroupPython] N_element046  label="N_element : 019"  # scripted group (container) (typed FeaturePython)
  n = 2
  ref = N_element
FEATURE [App::DocumentObjectGroupPython] O_element101  label="O_element : 055"  # scripted group (container) (typed FeaturePython)
  n = 1
  ref = O_element
FEATURE [App::DocumentObjectGroupPython] G4_UREA  # scripted group (container) (typed FeaturePython)
  Dunit = g/cm3
  Dvalue = 1.323
  Group = -> [C_element119,H_element107,N_element046,O_element101]
  conduct = 2
  density = 1
  expand = 3
  formula = G4_UREA
  name = G4_UREA
  specific = 4
FEATURE [App::DocumentObjectGroupPython] C_element120  label="C_element : 067"  # scripted group (container) (typed FeaturePython)
  n = 5
  ref = C_element
FEATURE [App::DocumentObjectGroupPython] H_element108  label="H_element : 058"  # scripted group (container) (typed FeaturePython)
  n = 11
  ref = H_element
FEATURE [App::DocumentObjectGroupPython] N_element047  label="N_element : 020"  # scripted group (container) (typed FeaturePython)
  n = 1
  ref = N_element
FEATURE [App::DocumentObjectGroupPython] O_element102  label="O_element : 056"  # scripted group (container) (typed FeaturePython)
  n = 2
  ref = O_element
FEATURE [App::DocumentObjectGroupPython] G4_VALINE  # scripted group (container) (typed FeaturePython)
  Dunit = g/cm3
  Dvalue = 1.23
  Group = -> [C_element120,H_element108,N_element047,O_element102]
  conduct = 2
  density = 1
  expand = 3
  formula = G4_VALINE
  name = G4_VALINE
  specific = 4
FEATURE [App::DocumentObjectGroupPython] H_element109  label="H_element : 0.009"  # scripted group (container) (typed FeaturePython)
  n = 0.009417
FEATURE [App::DocumentObjectGroupPython] C_element121  label="C_element : 0.281"  # scripted group (container) (typed FeaturePython)
  n = 0.280555
FEATURE [App::DocumentObjectGroupPython] F_element018  label="F_element : 0.710"  # scripted group (container) (typed FeaturePython)
  n = 0.710028
FEATURE [App::DocumentObjectGroupPython] G4_VITON  # scripted group (container) (typed FeaturePython)
  Dunit = g/cm3
  Dvalue = 1.8
  Group = -> [H_element109,C_element121,F_element018]
  conduct = 2
  density = 1
  expand = 3
  formula = G4_VITON
  name = G4_VITON
  specific = 4
FEATURE [App::DocumentObjectGroupPython] H_element110  label="H_element : 059"  # scripted group (container) (typed FeaturePython)
  n = 2
  ref = H_element
FEATURE [App::DocumentObjectGroupPython] O_element103  label="O_element : 057"  # scripted group (container) (typed FeaturePython)
  n = 1
  ref = O_element
FEATURE [App::DocumentObjectGroupPython] G4_WATER  # scripted group (container) (typed FeaturePython)
  Dunit = g/cm3
  Dvalue = 1
  Group = -> [H_element110,O_element103]
  conduct = 2
  density = 1
  expand = 3
  formula = G4_WATER
  name = G4_WATER
  specific = 4
FEATURE [App::DocumentObjectGroupPython] H_element111  label="H_element : 060"  # scripted group (container) (typed FeaturePython)
  n = 2
  ref = H_element
FEATURE [App::DocumentObjectGroupPython] O_element104  label="O_element : 058"  # scripted group (container) (typed FeaturePython)
  n = 1
  ref = O_element
FEATURE [App::DocumentObjectGroupPython] G4_WATER_VAPOR  # scripted group (container) (typed FeaturePython)
  Dunit = g/cm3
  Dvalue = 0.000756182
  Group = -> [H_element111,O_element104]
  conduct = 2
  density = 1
  expand = 3
  formula = G4_WATER_VAPOR
  name = G4_WATER_VAPOR
  specific = 4
FEATURE [App::DocumentObjectGroupPython] C_element122  label="C_element : 068"  # scripted group (container) (typed FeaturePython)
  n = 8
  ref = C_element
FEATURE [App::DocumentObjectGroupPython] H_element112  label="H_element : 061"  # scripted group (container) (typed FeaturePython)
  n = 10
  ref = H_element
FEATURE [App::DocumentObjectGroupPython] G4_XYLENE  # scripted group (container) (typed FeaturePython)
  Dunit = g/cm3
  Dvalue = 0.87
  Group = -> [C_element122,H_element112]
  conduct = 2
  density = 1
  expand = 3
  formula = G4_XYLENE
  name = G4_XYLENE
  specific = 4
FEATURE [App::DocumentObjectGroupPython] C_element123  label="C_element : 069"  # scripted group (container) (typed FeaturePython)
  n = 1
  ref = C_element
FEATURE [App::DocumentObjectGroupPython] G4_GRAPHITE  # scripted group (container) (typed FeaturePython)
  Dunit = g/cm3
  Dvalue = 2.21
  Group = -> [C_element123]
  conduct = 2
  density = 1
  expand = 3
  formula = G4_GRAPHITE
  name = G4_GRAPHITE
  specific = 4
FEATURE [App::DocumentObjectGroupPython] NIST  # scripted group (container) (typed FeaturePython)
  Group = -> [G4_A_150_TISSUE,G4_ACETONE,G4_ACETYLENE,G4_ADENINE,G4_ADIPOSE_TISSUE_ICRP,G4_AIR,G4_ALANINE,G4_ALUMINUM_OXIDE,G4_AMBER,G4_AMMONIA,G4_ANILINE,G4_ANTHRACENE,G4_B_100_BONE,G4_BAKELITE,G4_BARIUM_FLUORIDE,G4_BARIUM_SULFATE,G4_BENZENE,G4_BERYLLIUM_OXIDE,G4_BGO,G4_BLOOD_ICRP,G4_BONE_COMPACT_ICRU,G4_BONE_CORTICAL_ICRP,G4_BORON_CARBIDE,G4_BORON_OXIDE,G4_BRAIN_ICRP,G4_BUTANE,G4_N_BUTYL_ALCOHOL,G4_C_552,+152 more]
FEATURE [App::DocumentObjectGroupPython] H_element113  label="H_element : 062"  # scripted group (container) (typed FeaturePython)
  n = 1
  ref = H_element
FEATURE [App::DocumentObjectGroupPython] G4_H  # scripted group (container) (typed FeaturePython)
  Dunit = g/cm3
  Dvalue = 8.3748e-05
  Group = -> [H_element113]
  conduct = 2
  density = 1
  expand = 3
  formula = H
  name = G4_H
  specific = 4
FEATURE [App::DocumentObjectGroupPython] He_element001  label="He_element : 1"  # scripted group (container) (typed FeaturePython)
  n = 1
  ref = He_element
FEATURE [App::DocumentObjectGroupPython] G4_He  # scripted group (container) (typed FeaturePython)
  Dunit = g/cm3
  Dvalue = 0.000166322
  Group = -> [He_element001]
  conduct = 2
  density = 1
  expand = 3
  formula = He
  name = G4_He
  specific = 4
FEATURE [App::DocumentObjectGroupPython] Li_element008  label="Li_element : 008"  # scripted group (container) (typed FeaturePython)
  n = 1
  ref = Li_element
FEATURE [App::DocumentObjectGroupPython] G4_Li  # scripted group (container) (typed FeaturePython)
  Dunit = g/cm3
  Dvalue = 0.534
  Group = -> [Li_element008]
  conduct = 2
  density = 1
  expand = 3
  formula = Li
  name = G4_Li
  specific = 4
FEATURE [App::DocumentObjectGroupPython] Be_element002  label="Be_element : 002"  # scripted group (container) (typed FeaturePython)
  n = 1
  ref = Be_element
FEATURE [App::DocumentObjectGroupPython] G4_Be  # scripted group (container) (typed FeaturePython)
  Dunit = g/cm3
  Dvalue = 1.848
  Group = -> [Be_element002]
  conduct = 2
  density = 1
  expand = 3
  formula = Be
  name = G4_Be
  specific = 4
FEATURE [App::DocumentObjectGroupPython] B_element007  label="B_element : 007"  # scripted group (container) (typed FeaturePython)
  n = 1
  ref = B_element
FEATURE [App::DocumentObjectGroupPython] G4_B  # scripted group (container) (typed FeaturePython)
  Dunit = g/cm3
  Dvalue = 2.37
  Group = -> [B_element007]
  conduct = 2
  density = 1
  expand = 3
  formula = B
  name = G4_B
  specific = 4
FEATURE [App::DocumentObjectGroupPython] C_element124  label="C_element : 070"  # scripted group (container) (typed FeaturePython)
  n = 1
  ref = C_element
FEATURE [App::DocumentObjectGroupPython] G4_C  # scripted group (container) (typed FeaturePython)
  Dunit = g/cm3
  Dvalue = 2
  Group = -> [C_element124]
  conduct = 2
  density = 1
  expand = 3
  formula = C
  name = G4_C
  specific = 4
FEATURE [App::DocumentObjectGroupPython] N_element048  label="N_element : 021"  # scripted group (container) (typed FeaturePython)
  n = 1
  ref = N_element
FEATURE [App::DocumentObjectGroupPython] G4_N  # scripted group (container) (typed FeaturePython)
  Dunit = g/cm3
  Dvalue = 0.0011652
  Group = -> [N_element048]
  conduct = 2
  density = 1
  expand = 3
  formula = N
  name = G4_N
  specific = 4
FEATURE [App::DocumentObjectGroupPython] O_element105  label="O_element : 059"  # scripted group (container) (typed FeaturePython)
  n = 1
  ref = O_element
FEATURE [App::DocumentObjectGroupPython] G4_O  # scripted group (container) (typed FeaturePython)
  Dunit = g/cm3
  Dvalue = 0.00133151
  Group = -> [O_element105]
  conduct = 2
  density = 1
  expand = 3
  formula = O
  name = G4_O
  specific = 4
FEATURE [App::DocumentObjectGroupPython] F_element019  label="F_element : 008"  # scripted group (container) (typed FeaturePython)
  n = 1
  ref = F_element
FEATURE [App::DocumentObjectGroupPython] G4_F  # scripted group (container) (typed FeaturePython)
  Dunit = g/cm3
  Dvalue = 0.00158029
  Group = -> [F_element019]
  conduct = 2
  density = 1
  expand = 3
  formula = F
  name = G4_F
  specific = 4
FEATURE [App::DocumentObjectGroupPython] Ne_element001  label="Ne_element : 1"  # scripted group (container) (typed FeaturePython)
  n = 1
  ref = Ne_element
FEATURE [App::DocumentObjectGroupPython] G4_Ne  # scripted group (container) (typed FeaturePython)
  Dunit = g/cm3
  Dvalue = 0.000838505
  Group = -> [Ne_element001]
  conduct = 2
  density = 1
  expand = 3
  formula = Ne
  name = G4_Ne
  specific = 4
FEATURE [App::DocumentObjectGroupPython] Na_element020  label="Na_element : 005"  # scripted group (container) (typed FeaturePython)
  n = 1
  ref = Na_element
FEATURE [App::DocumentObjectGroupPython] G4_Na  # scripted group (container) (typed FeaturePython)
  Dunit = g/cm3
  Dvalue = 0.971
  Group = -> [Na_element020]
  conduct = 2
  density = 1
  expand = 3
  formula = Na
  name = G4_Na
  specific = 4
FEATURE [App::DocumentObjectGroupPython] Mg_element011  label="Mg_element : 005"  # scripted group (container) (typed FeaturePython)
  n = 1
  ref = Mg_element
FEATURE [App::DocumentObjectGroupPython] G4_Mg  # scripted group (container) (typed FeaturePython)
  Dunit = g/cm3
  Dvalue = 1.74
  Group = -> [Mg_element011]
  conduct = 2
  density = 1
  expand = 3
  formula = Mg
  name = G4_Mg
  specific = 4
FEATURE [App::DocumentObjectGroupPython] Al_element004  label="Al_element : 1"  # scripted group (container) (typed FeaturePython)
  n = 1
  ref = Al_element
FEATURE [App::DocumentObjectGroupPython] G4_Al  # scripted group (container) (typed FeaturePython)
  Dunit = g/cm3
  Dvalue = 2.699
  Group = -> [Al_element004]
  conduct = 2
  density = 1
  expand = 3
  formula = Al
  name = G4_Al
  specific = 4
FEATURE [App::DocumentObjectGroupPython] Si_element007  label="Si_element : 002"  # scripted group (container) (typed FeaturePython)
  n = 1
  ref = Si_element
FEATURE [App::DocumentObjectGroupPython] G4_Si  # scripted group (container) (typed FeaturePython)
  Dunit = g/cm3
  Dvalue = 2.33
  Group = -> [Si_element007]
  conduct = 2
  density = 1
  expand = 3
  formula = Si
  name = G4_Si
  specific = 4
FEATURE [App::DocumentObjectGroupPython] P_element013  label="P_element : 002"  # scripted group (container) (typed FeaturePython)
  n = 1
  ref = P_element
FEATURE [App::DocumentObjectGroupPython] G4_P  # scripted group (container) (typed FeaturePython)
  Dunit = g/cm3
  Dvalue = 2.2
  Group = -> [P_element013]
  conduct = 2
  density = 1
  expand = 3
  formula = P
  name = G4_P
  specific = 4
FEATURE [App::DocumentObjectGroupPython] S_element023  label="S_element : 007"  # scripted group (container) (typed FeaturePython)
  n = 1
  ref = S_element
FEATURE [App::DocumentObjectGroupPython] G4_S  # scripted group (container) (typed FeaturePython)
  Dunit = g/cm3
  Dvalue = 2
  Group = -> [S_element023]
  conduct = 2
  density = 1
  expand = 3
  formula = S
  name = G4_S
  specific = 4
FEATURE [App::DocumentObjectGroupPython] Cl_element029  label="Cl_element : 015"  # scripted group (container) (typed FeaturePython)
  n = 1
  ref = Cl_element
FEATURE [App::DocumentObjectGroupPython] G4_Cl  # scripted group (container) (typed FeaturePython)
  Dunit = g/cm3
  Dvalue = 0.00299473
  Group = -> [Cl_element029]
  conduct = 2
  density = 1
  expand = 3
  formula = Cl
  name = G4_Cl
  specific = 4
FEATURE [App::DocumentObjectGroupPython] Ar_element002  label="Ar_element : 1"  # scripted group (container) (typed FeaturePython)
  n = 1
  ref = Ar_element
FEATURE [App::DocumentObjectGroupPython] G4_Ar  # scripted group (container) (typed FeaturePython)
  Dunit = g/cm3
  Dvalue = 0.00166201
  Group = -> [Ar_element002]
  conduct = 2
  density = 1
  expand = 3
  formula = Ar
  name = G4_Ar
  specific = 4
FEATURE [App::DocumentObjectGroupPython] K_element013  label="K_element : 003"  # scripted group (container) (typed FeaturePython)
  n = 1
  ref = K_element
FEATURE [App::DocumentObjectGroupPython] G4_K  # scripted group (container) (typed FeaturePython)
  Dunit = g/cm3
  Dvalue = 0.862
  Group = -> [K_element013]
  conduct = 2
  density = 1
  expand = 3
  formula = K
  name = G4_K
  specific = 4
FEATURE [App::DocumentObjectGroupPython] Ca_element014  label="Ca_element : 007"  # scripted group (container) (typed FeaturePython)
  n = 1
  ref = Ca_element
FEATURE [App::DocumentObjectGroupPython] G4_Ca  # scripted group (container) (typed FeaturePython)
  Dunit = g/cm3
  Dvalue = 1.55
  Group = -> [Ca_element014]
  conduct = 2
  density = 1
  expand = 3
  formula = Ca
  name = G4_Ca
  specific = 4
FEATURE [App::DocumentObjectGroupPython] Sc_element001  label="Sc_element : 1"  # scripted group (container) (typed FeaturePython)
  n = 1
  ref = Sc_element
FEATURE [App::DocumentObjectGroupPython] G4_Sc  # scripted group (container) (typed FeaturePython)
  Dunit = g/cm3
  Dvalue = 2.989
  Group = -> [Sc_element001]
  conduct = 2
  density = 1
  expand = 3
  formula = Sc
  name = G4_Sc
  specific = 4
FEATURE [App::DocumentObjectGroupPython] Ti_element004  label="Ti_element : 002"  # scripted group (container) (typed FeaturePython)
  n = 1
  ref = Ti_element
FEATURE [App::DocumentObjectGroupPython] G4_Ti  # scripted group (container) (typed FeaturePython)
  Dunit = g/cm3
  Dvalue = 4.54
  Group = -> [Ti_element004]
  conduct = 2
  density = 1
  expand = 3
  formula = Ti
  name = G4_Ti
  specific = 4
FEATURE [App::DocumentObjectGroupPython] V_element001  label="V_element : 1"  # scripted group (container) (typed FeaturePython)
  n = 1
  ref = V_element
FEATURE [App::DocumentObjectGroupPython] G4_V  # scripted group (container) (typed FeaturePython)
  Dunit = g/cm3
  Dvalue = 6.11
  Group = -> [V_element001]
  conduct = 2
  density = 1
  expand = 3
  formula = V
  name = G4_V
  specific = 4
FEATURE [App::DocumentObjectGroupPython] Cr_element001  label="Cr_element : 1"  # scripted group (container) (typed FeaturePython)
  n = 1
  ref = Cr_element
FEATURE [App::DocumentObjectGroupPython] G4_Cr  # scripted group (container) (typed FeaturePython)
  Dunit = g/cm3
  Dvalue = 7.18
  Group = -> [Cr_element001]
  conduct = 2
  density = 1
  expand = 3
  formula = Cr
  name = G4_Cr
  specific = 4
FEATURE [App::DocumentObjectGroupPython] Mn_element001  label="Mn_element : 1"  # scripted group (container) (typed FeaturePython)
  n = 1
  ref = Mn_element
FEATURE [App::DocumentObjectGroupPython] G4_Mn  # scripted group (container) (typed FeaturePython)
  Dunit = g/cm3
  Dvalue = 7.44
  Group = -> [Mn_element001]
  conduct = 2
  density = 1
  expand = 3
  formula = Mn
  name = G4_Mn
  specific = 4
FEATURE [App::DocumentObjectGroupPython] Fe_element007  label="Fe_element : 004"  # scripted group (container) (typed FeaturePython)
  n = 1
  ref = Fe_element
FEATURE [App::DocumentObjectGroupPython] G4_Fe  # scripted group (container) (typed FeaturePython)
  Dunit = g/cm3
  Dvalue = 7.874
  Group = -> [Fe_element007]
  conduct = 2
  density = 1
  expand = 3
  formula = Fe
  name = G4_Fe
  specific = 4
FEATURE [App::DocumentObjectGroupPython] Co_element001  label="Co_element : 1"  # scripted group (container) (typed FeaturePython)
  n = 1
  ref = Co_element
FEATURE [App::DocumentObjectGroupPython] G4_Co  # scripted group (container) (typed FeaturePython)
  Dunit = g/cm3
  Dvalue = 8.9
  Group = -> [Co_element001]
  conduct = 2
  density = 1
  expand = 3
  formula = Co
  name = G4_Co
  specific = 4
FEATURE [App::DocumentObjectGroupPython] Ni_element001  label="Ni_element : 1"  # scripted group (container) (typed FeaturePython)
  n = 1
  ref = Ni_element
FEATURE [App::DocumentObjectGroupPython] G4_Ni  # scripted group (container) (typed FeaturePython)
  Dunit = g/cm3
  Dvalue = 8.902
  Group = -> [Ni_element001]
  conduct = 2
  density = 1
  expand = 3
  formula = Ni
  name = G4_Ni
  specific = 4
FEATURE [App::DocumentObjectGroupPython] Cu_element001  label="Cu_element : 1"  # scripted group (container) (typed FeaturePython)
  n = 1
  ref = Cu_element
FEATURE [App::DocumentObjectGroupPython] G4_Cu  # scripted group (container) (typed FeaturePython)
  Dunit = g/cm3
  Dvalue = 8.96
  Group = -> [Cu_element001]
  conduct = 2
  density = 1
  expand = 3
  formula = Cu
  name = G4_Cu
  specific = 4
FEATURE [App::DocumentObjectGroupPython] Zn_element001  label="Zn_element : 1"  # scripted group (container) (typed FeaturePython)
  n = 1
  ref = Zn_element
FEATURE [App::DocumentObjectGroupPython] G4_Zn  # scripted group (container) (typed FeaturePython)
  Dunit = g/cm3
  Dvalue = 7.133
  Group = -> [Zn_element001]
  conduct = 2
  density = 1
  expand = 3
  formula = Zn
  name = G4_Zn
  specific = 4
FEATURE [App::DocumentObjectGroupPython] Ga_element002  label="Ga_element : 002"  # scripted group (container) (typed FeaturePython)
  n = 1
  ref = Ga_element
FEATURE [App::DocumentObjectGroupPython] G4_Ga  # scripted group (container) (typed FeaturePython)
  Dunit = g/cm3
  Dvalue = 5.904
  Group = -> [Ga_element002]
  conduct = 2
  density = 1
  expand = 3
  formula = Ga
  name = G4_Ga
  specific = 4
FEATURE [App::DocumentObjectGroupPython] Ge_element002  label="Ge_element : 1"  # scripted group (container) (typed FeaturePython)
  n = 1
  ref = Ge_element
FEATURE [App::DocumentObjectGroupPython] G4_Ge  # scripted group (container) (typed FeaturePython)
  Dunit = g/cm3
  Dvalue = 5.323
  Group = -> [Ge_element002]
  conduct = 2
  density = 1
  expand = 3
  formula = Ge
  name = G4_Ge
  specific = 4
FEATURE [App::DocumentObjectGroupPython] As_element003  label="As_element : 002"  # scripted group (container) (typed FeaturePython)
  n = 1
  ref = As_element
FEATURE [App::DocumentObjectGroupPython] G4_As  # scripted group (container) (typed FeaturePython)
  Dunit = g/cm3
  Dvalue = 5.73
  Group = -> [As_element003]
  conduct = 2
  density = 1
  expand = 3
  formula = As
  name = G4_As
  specific = 4
FEATURE [App::DocumentObjectGroupPython] Se_element001  label="Se_element : 1"  # scripted group (container) (typed FeaturePython)
  n = 1
  ref = Se_element
FEATURE [App::DocumentObjectGroupPython] G4_Se  # scripted group (container) (typed FeaturePython)
  Dunit = g/cm3
  Dvalue = 4.5
  Group = -> [Se_element001]
  conduct = 2
  density = 1
  expand = 3
  formula = Se
  name = G4_Se
  specific = 4
FEATURE [App::DocumentObjectGroupPython] Br_element007  label="Br_element : 004"  # scripted group (container) (typed FeaturePython)
  n = 1
  ref = Br_element
FEATURE [App::DocumentObjectGroupPython] G4_Br  # scripted group (container) (typed FeaturePython)
  Dunit = g/cm3
  Dvalue = 0.0070721
  Group = -> [Br_element007]
  conduct = 2
  density = 1
  expand = 3
  formula = Br
  name = G4_Br
  specific = 4
FEATURE [App::DocumentObjectGroupPython] Kr_element001  label="Kr_element : 1"  # scripted group (container) (typed FeaturePython)
  n = 1
  ref = Kr_element
FEATURE [App::DocumentObjectGroupPython] G4_Kr  # scripted group (container) (typed FeaturePython)
  Dunit = g/cm3
  Dvalue = 0.00347832
  Group = -> [Kr_element001]
  conduct = 2
  density = 1
  expand = 3
  formula = Kr
  name = G4_Kr
  specific = 4
FEATURE [App::DocumentObjectGroupPython] Rb_element001  label="Rb_element : 1"  # scripted group (container) (typed FeaturePython)
  n = 1
  ref = Rb_element
FEATURE [App::DocumentObjectGroupPython] G4_Rb  # scripted group (container) (typed FeaturePython)
  Dunit = g/cm3
  Dvalue = 1.532
  Group = -> [Rb_element001]
  conduct = 2
  density = 1
  expand = 3
  formula = Rb
  name = G4_Rb
  specific = 4
FEATURE [App::DocumentObjectGroupPython] Sr_element001  label="Sr_element : 1"  # scripted group (container) (typed FeaturePython)
  n = 1
  ref = Sr_element
FEATURE [App::DocumentObjectGroupPython] G4_Sr  # scripted group (container) (typed FeaturePython)
  Dunit = g/cm3
  Dvalue = 2.54
  Group = -> [Sr_element001]
  conduct = 2
  density = 1
  expand = 3
  formula = Sr
  name = G4_Sr
  specific = 4
FEATURE [App::DocumentObjectGroupPython] Y_element001  label="Y_element : 1"  # scripted group (container) (typed FeaturePython)
  n = 1
  ref = Y_element
FEATURE [App::DocumentObjectGroupPython] G4_Y  # scripted group (container) (typed FeaturePython)
  Dunit = g/cm3
  Dvalue = 4.469
  Group = -> [Y_element001]
  conduct = 2
  density = 1
  expand = 3
  formula = Y
  name = G4_Y
  specific = 4
FEATURE [App::DocumentObjectGroupPython] Zr_element001  label="Zr_element : 1"  # scripted group (container) (typed FeaturePython)
  n = 1
  ref = Zr_element
FEATURE [App::DocumentObjectGroupPython] G4_Zr  # scripted group (container) (typed FeaturePython)
  Dunit = g/cm3
  Dvalue = 6.506
  Group = -> [Zr_element001]
  conduct = 2
  density = 1
  expand = 3
  formula = Zr
  name = G4_Zr
  specific = 4
FEATURE [App::DocumentObjectGroupPython] Nb_element001  label="Nb_element : 1"  # scripted group (container) (typed FeaturePython)
  n = 1
  ref = Nb_element
FEATURE [App::DocumentObjectGroupPython] G4_Nb  # scripted group (container) (typed FeaturePython)
  Dunit = g/cm3
  Dvalue = 8.57
  Group = -> [Nb_element001]
  conduct = 2
  density = 1
  expand = 3
  formula = Nb
  name = G4_Nb
  specific = 4
FEATURE [App::DocumentObjectGroupPython] Mo_element001  label="Mo_element : 1"  # scripted group (container) (typed FeaturePython)
  n = 1
  ref = Mo_element
FEATURE [App::DocumentObjectGroupPython] G4_Mo  # scripted group (container) (typed FeaturePython)
  Dunit = g/cm3
  Dvalue = 10.22
  Group = -> [Mo_element001]
  conduct = 2
  density = 1
  expand = 3
  formula = Mo
  name = G4_Mo
  specific = 4
FEATURE [App::DocumentObjectGroupPython] Tc_element001  label="Tc_element : 1"  # scripted group (container) (typed FeaturePython)
  n = 1
  ref = Tc_element
FEATURE [App::DocumentObjectGroupPython] G4_Tc  # scripted group (container) (typed FeaturePython)
  Dunit = g/cm3
  Dvalue = 11.5
  Group = -> [Tc_element001]
  conduct = 2
  density = 1
  expand = 3
  formula = Tc
  name = G4_Tc
  specific = 4
FEATURE [App::DocumentObjectGroupPython] Ru_element001  label="Ru_element : 1"  # scripted group (container) (typed FeaturePython)
  n = 1
  ref = Ru_element
FEATURE [App::DocumentObjectGroupPython] G4_Ru  # scripted group (container) (typed FeaturePython)
  Dunit = g/cm3
  Dvalue = 12.41
  Group = -> [Ru_element001]
  conduct = 2
  density = 1
  expand = 3
  formula = Ru
  name = G4_Ru
  specific = 4
FEATURE [App::DocumentObjectGroupPython] Rh_element001  label="Rh_element : 1"  # scripted group (container) (typed FeaturePython)
  n = 1
  ref = Rh_element
FEATURE [App::DocumentObjectGroupPython] G4_Rh  # scripted group (container) (typed FeaturePython)
  Dunit = g/cm3
  Dvalue = 12.41
  Group = -> [Rh_element001]
  conduct = 2
  density = 1
  expand = 3
  formula = Rh
  name = G4_Rh
  specific = 4
FEATURE [App::DocumentObjectGroupPython] Pd_element001  label="Pd_element : 1"  # scripted group (container) (typed FeaturePython)
  n = 1
  ref = Pd_element
FEATURE [App::DocumentObjectGroupPython] G4_Pd  # scripted group (container) (typed FeaturePython)
  Dunit = g/cm3
  Dvalue = 12.02
  Group = -> [Pd_element001]
  conduct = 2
  density = 1
  expand = 3
  formula = Pd
  name = G4_Pd
  specific = 4
FEATURE [App::DocumentObjectGroupPython] Ag_element006  label="Ag_element : 004"  # scripted group (container) (typed FeaturePython)
  n = 1
  ref = Ag_element
FEATURE [App::DocumentObjectGroupPython] G4_Ag  # scripted group (container) (typed FeaturePython)
  Dunit = g/cm3
  Dvalue = 10.5
  Group = -> [Ag_element006]
  conduct = 2
  density = 1
  expand = 3
  formula = Ag
  name = G4_Ag
  specific = 4
FEATURE [App::DocumentObjectGroupPython] Cd_element003  label="Cd_element : 003"  # scripted group (container) (typed FeaturePython)
  n = 1
  ref = Cd_element
FEATURE [App::DocumentObjectGroupPython] G4_Cd  # scripted group (container) (typed FeaturePython)
  Dunit = g/cm3
  Dvalue = 8.65
  Group = -> [Cd_element003]
  conduct = 2
  density = 1
  expand = 3
  formula = Cd
  name = G4_Cd
  specific = 4
FEATURE [App::DocumentObjectGroupPython] In_element001  label="In_element : 1"  # scripted group (container) (typed FeaturePython)
  n = 1
  ref = In_element
FEATURE [App::DocumentObjectGroupPython] G4_In  # scripted group (container) (typed FeaturePython)
  Dunit = g/cm3
  Dvalue = 7.31
  Group = -> [In_element001]
  conduct = 2
  density = 1
  expand = 3
  formula = In
  name = G4_In
  specific = 4
FEATURE [App::DocumentObjectGroupPython] Sn_element001  label="Sn_element : 1"  # scripted group (container) (typed FeaturePython)
  n = 1
  ref = Sn_element
FEATURE [App::DocumentObjectGroupPython] G4_Sn  # scripted group (container) (typed FeaturePython)
  Dunit = g/cm3
  Dvalue = 7.31
  Group = -> [Sn_element001]
  conduct = 2
  density = 1
  expand = 3
  formula = Sn
  name = G4_Sn
  specific = 4
FEATURE [App::DocumentObjectGroupPython] Sb_element001  label="Sb_element : 1"  # scripted group (container) (typed FeaturePython)
  n = 1
  ref = Sb_element
FEATURE [App::DocumentObjectGroupPython] G4_Sb  # scripted group (container) (typed FeaturePython)
  Dunit = g/cm3
  Dvalue = 6.691
  Group = -> [Sb_element001]
  conduct = 2
  density = 1
  expand = 3
  formula = Sb
  name = G4_Sb
  specific = 4
FEATURE [App::DocumentObjectGroupPython] Te_element002  label="Te_element : 002"  # scripted group (container) (typed FeaturePython)
  n = 1
  ref = Te_element
FEATURE [App::DocumentObjectGroupPython] G4_Te  # scripted group (container) (typed FeaturePython)
  Dunit = g/cm3
  Dvalue = 6.24
  Group = -> [Te_element002]
  conduct = 2
  density = 1
  expand = 3
  formula = Te
  name = G4_Te
  specific = 4
FEATURE [App::DocumentObjectGroupPython] I_element010  label="I_element : 006"  # scripted group (container) (typed FeaturePython)
  n = 1
  ref = I_element
FEATURE [App::DocumentObjectGroupPython] G4_I  # scripted group (container) (typed FeaturePython)
  Dunit = g/cm3
  Dvalue = 4.93
  Group = -> [I_element010]
  conduct = 2
  density = 1
  expand = 3
  formula = I
  name = G4_I
  specific = 4
FEATURE [App::DocumentObjectGroupPython] Xe_element001  label="Xe_element : 1"  # scripted group (container) (typed FeaturePython)
  n = 1
  ref = Xe_element
FEATURE [App::DocumentObjectGroupPython] G4_Xe  # scripted group (container) (typed FeaturePython)
  Dunit = g/cm3
  Dvalue = 0.00548536
  Group = -> [Xe_element001]
  conduct = 2
  density = 1
  expand = 3
  formula = Xe
  name = G4_Xe
  specific = 4
FEATURE [App::DocumentObjectGroupPython] Cs_element003  label="Cs_element : 003"  # scripted group (container) (typed FeaturePython)
  n = 1
  ref = Cs_element
FEATURE [App::DocumentObjectGroupPython] G4_Cs  # scripted group (container) (typed FeaturePython)
  Dunit = g/cm3
  Dvalue = 1.873
  Group = -> [Cs_element003]
  conduct = 2
  density = 1
  expand = 3
  formula = Cs
  name = G4_Cs
  specific = 4
FEATURE [App::DocumentObjectGroupPython] Ba_element003  label="Ba_element : 003"  # scripted group (container) (typed FeaturePython)
  n = 1
  ref = Ba_element
FEATURE [App::DocumentObjectGroupPython] G4_Ba  # scripted group (container) (typed FeaturePython)
  Dunit = g/cm3
  Dvalue = 3.5
  Group = -> [Ba_element003]
  conduct = 2
  density = 1
  expand = 3
  formula = Ba
  name = G4_Ba
  specific = 4
FEATURE [App::DocumentObjectGroupPython] La_element003  label="La_element : 003"  # scripted group (container) (typed FeaturePython)
  n = 1
  ref = La_element
FEATURE [App::DocumentObjectGroupPython] G4_La  # scripted group (container) (typed FeaturePython)
  Dunit = g/cm3
  Dvalue = 6.154
  Group = -> [La_element003]
  conduct = 2
  density = 1
  expand = 3
  formula = La
  name = G4_La
  specific = 4
FEATURE [App::DocumentObjectGroupPython] Ce_element002  label="Ce_element : 1"  # scripted group (container) (typed FeaturePython)
  n = 1
  ref = Ce_element
FEATURE [App::DocumentObjectGroupPython] G4_Ce  # scripted group (container) (typed FeaturePython)
  Dunit = g/cm3
  Dvalue = 6.657
  Group = -> [Ce_element002]
  conduct = 2
  density = 1
  expand = 3
  formula = Ce
  name = G4_Ce
  specific = 4
FEATURE [App::DocumentObjectGroupPython] Pr_element001  label="Pr_element : 1"  # scripted group (container) (typed FeaturePython)
  n = 1
  ref = Pr_element
FEATURE [App::DocumentObjectGroupPython] G4_Pr  # scripted group (container) (typed FeaturePython)
  Dunit = g/cm3
  Dvalue = 6.71
  Group = -> [Pr_element001]
  conduct = 2
  density = 1
  expand = 3
  formula = Pr
  name = G4_Pr
  specific = 4
FEATURE [App::DocumentObjectGroupPython] Nd_element001  label="Nd_element : 1"  # scripted group (container) (typed FeaturePython)
  n = 1
  ref = Nd_element
FEATURE [App::DocumentObjectGroupPython] G4_Nd  # scripted group (container) (typed FeaturePython)
  Dunit = g/cm3
  Dvalue = 6.9
  Group = -> [Nd_element001]
  conduct = 2
  density = 1
  expand = 3
  formula = Nd
  name = G4_Nd
  specific = 4
FEATURE [App::DocumentObjectGroupPython] Pm_element001  label="Pm_element : 1"  # scripted group (container) (typed FeaturePython)
  n = 1
  ref = Pm_element
FEATURE [App::DocumentObjectGroupPython] G4_Pm  # scripted group (container) (typed FeaturePython)
  Dunit = g/cm3
  Dvalue = 7.22
  Group = -> [Pm_element001]
  conduct = 2
  density = 1
  expand = 3
  formula = Pm
  name = G4_Pm
  specific = 4
FEATURE [App::DocumentObjectGroupPython] Sm_element001  label="Sm_element : 1"  # scripted group (container) (typed FeaturePython)
  n = 1
  ref = Sm_element
FEATURE [App::DocumentObjectGroupPython] G4_Sm  # scripted group (container) (typed FeaturePython)
  Dunit = g/cm3
  Dvalue = 7.46
  Group = -> [Sm_element001]
  conduct = 2
  density = 1
  expand = 3
  formula = Sm
  name = G4_Sm
  specific = 4
FEATURE [App::DocumentObjectGroupPython] Eu_element001  label="Eu_element : 1"  # scripted group (container) (typed FeaturePython)
  n = 1
  ref = Eu_element
FEATURE [App::DocumentObjectGroupPython] G4_Eu  # scripted group (container) (typed FeaturePython)
  Dunit = g/cm3
  Dvalue = 5.243
  Group = -> [Eu_element001]
  conduct = 2
  density = 1
  expand = 3
  formula = Eu
  name = G4_Eu
  specific = 4
FEATURE [App::DocumentObjectGroupPython] Gd_element002  label="Gd_element : 1"  # scripted group (container) (typed FeaturePython)
  n = 1
  ref = Gd_element
FEATURE [App::DocumentObjectGroupPython] G4_Gd  # scripted group (container) (typed FeaturePython)
  Dunit = g/cm3
  Dvalue = 7.9004
  Group = -> [Gd_element002]
  conduct = 2
  density = 1
  expand = 3
  formula = Gd
  name = G4_Gd
  specific = 4
FEATURE [App::DocumentObjectGroupPython] Tb_element001  label="Tb_element : 1"  # scripted group (container) (typed FeaturePython)
  n = 1
  ref = Tb_element
FEATURE [App::DocumentObjectGroupPython] G4_Tb  # scripted group (container) (typed FeaturePython)
  Dunit = g/cm3
  Dvalue = 8.229
  Group = -> [Tb_element001]
  conduct = 2
  density = 1
  expand = 3
  formula = Tb
  name = G4_Tb
  specific = 4
FEATURE [App::DocumentObjectGroupPython] Dy_element001  label="Dy_element : 1"  # scripted group (container) (typed FeaturePython)
  n = 1
  ref = Dy_element
FEATURE [App::DocumentObjectGroupPython] G4_Dy  # scripted group (container) (typed FeaturePython)
  Dunit = g/cm3
  Dvalue = 8.55
  Group = -> [Dy_element001]
  conduct = 2
  density = 1
  expand = 3
  formula = Dy
  name = G4_Dy
  specific = 4
FEATURE [App::DocumentObjectGroupPython] Ho_element001  label="Ho_element : 1"  # scripted group (container) (typed FeaturePython)
  n = 1
  ref = Ho_element
FEATURE [App::DocumentObjectGroupPython] G4_Ho  # scripted group (container) (typed FeaturePython)
  Dunit = g/cm3
  Dvalue = 8.795
  Group = -> [Ho_element001]
  conduct = 2
  density = 1
  expand = 3
  formula = Ho
  name = G4_Ho
  specific = 4
FEATURE [App::DocumentObjectGroupPython] Er_element001  label="Er_element : 1"  # scripted group (container) (typed FeaturePython)
  n = 1
  ref = Er_element
FEATURE [App::DocumentObjectGroupPython] G4_Er  # scripted group (container) (typed FeaturePython)
  Dunit = g/cm3
  Dvalue = 9.066
  Group = -> [Er_element001]
  conduct = 2
  density = 1
  expand = 3
  formula = Er
  name = G4_Er
  specific = 4
FEATURE [App::DocumentObjectGroupPython] Tm_element001  label="Tm_element : 1"  # scripted group (container) (typed FeaturePython)
  n = 1
  ref = Tm_element
FEATURE [App::DocumentObjectGroupPython] G4_Tm  # scripted group (container) (typed FeaturePython)
  Dunit = g/cm3
  Dvalue = 9.321
  Group = -> [Tm_element001]
  conduct = 2
  density = 1
  expand = 3
  formula = Tm
  name = G4_Tm
  specific = 4
FEATURE [App::DocumentObjectGroupPython] Yb_element001  label="Yb_element : 1"  # scripted group (container) (typed FeaturePython)
  n = 1
  ref = Yb_element
FEATURE [App::DocumentObjectGroupPython] G4_Yb  # scripted group (container) (typed FeaturePython)
  Dunit = g/cm3
  Dvalue = 6.73
  Group = -> [Yb_element001]
  conduct = 2
  density = 1
  expand = 3
  formula = Yb
  name = G4_Yb
  specific = 4
FEATURE [App::DocumentObjectGroupPython] Lu_element001  label="Lu_element : 1"  # scripted group (container) (typed FeaturePython)
  n = 1
  ref = Lu_element
FEATURE [App::DocumentObjectGroupPython] G4_Lu  # scripted group (container) (typed FeaturePython)
  Dunit = g/cm3
  Dvalue = 9.84
  Group = -> [Lu_element001]
  conduct = 2
  density = 1
  expand = 3
  formula = Lu
  name = G4_Lu
  specific = 4
FEATURE [App::DocumentObjectGroupPython] Hf_element001  label="Hf_element : 1"  # scripted group (container) (typed FeaturePython)
  n = 1
  ref = Hf_element
FEATURE [App::DocumentObjectGroupPython] G4_Hf  # scripted group (container) (typed FeaturePython)
  Dunit = g/cm3
  Dvalue = 13.31
  Group = -> [Hf_element001]
  conduct = 2
  density = 1
  expand = 3
  formula = Hf
  name = G4_Hf
  specific = 4
FEATURE [App::DocumentObjectGroupPython] Ta_element001  label="Ta_element : 1"  # scripted group (container) (typed FeaturePython)
  n = 1
  ref = Ta_element
FEATURE [App::DocumentObjectGroupPython] G4_Ta  # scripted group (container) (typed FeaturePython)
  Dunit = g/cm3
  Dvalue = 16.654
  Group = -> [Ta_element001]
  conduct = 2
  density = 1
  expand = 3
  formula = Ta
  name = G4_Ta
  specific = 4
FEATURE [App::DocumentObjectGroupPython] W_element004  label="W_element : 004"  # scripted group (container) (typed FeaturePython)
  n = 1
  ref = W_element
FEATURE [App::DocumentObjectGroupPython] G4_W  # scripted group (container) (typed FeaturePython)
  Dunit = g/cm3
  Dvalue = 19.3
  Group = -> [W_element004]
  conduct = 2
  density = 1
  expand = 3
  formula = W
  name = G4_W
  specific = 4
FEATURE [App::DocumentObjectGroupPython] Re_element001  label="Re_element : 1"  # scripted group (container) (typed FeaturePython)
  n = 1
  ref = Re_element
FEATURE [App::DocumentObjectGroupPython] G4_Re  # scripted group (container) (typed FeaturePython)
  Dunit = g/cm3
  Dvalue = 21.02
  Group = -> [Re_element001]
  conduct = 2
  density = 1
  expand = 3
  formula = Re
  name = G4_Re
  specific = 4
FEATURE [App::DocumentObjectGroupPython] Os_element001  label="Os_element : 1"  # scripted group (container) (typed FeaturePython)
  n = 1
  ref = Os_element
FEATURE [App::DocumentObjectGroupPython] G4_Os  # scripted group (container) (typed FeaturePython)
  Dunit = g/cm3
  Dvalue = 22.57
  Group = -> [Os_element001]
  conduct = 2
  density = 1
  expand = 3
  formula = Os
  name = G4_Os
  specific = 4
FEATURE [App::DocumentObjectGroupPython] Ir_element001  label="Ir_element : 1"  # scripted group (container) (typed FeaturePython)
  n = 1
  ref = Ir_element
FEATURE [App::DocumentObjectGroupPython] G4_Ir  # scripted group (container) (typed FeaturePython)
  Dunit = g/cm3
  Dvalue = 22.42
  Group = -> [Ir_element001]
  conduct = 2
  density = 1
  expand = 3
  formula = Ir
  name = G4_Ir
  specific = 4
FEATURE [App::DocumentObjectGroupPython] Pt_element001  label="Pt_element : 1"  # scripted group (container) (typed FeaturePython)
  n = 1
  ref = Pt_element
FEATURE [App::DocumentObjectGroupPython] G4_Pt  # scripted group (container) (typed FeaturePython)
  Dunit = g/cm3
  Dvalue = 21.45
  Group = -> [Pt_element001]
  conduct = 2
  density = 1
  expand = 3
  formula = Pt
  name = G4_Pt
  specific = 4
FEATURE [App::DocumentObjectGroupPython] Au_element001  label="Au_element : 1"  # scripted group (container) (typed FeaturePython)
  n = 1
  ref = Au_element
FEATURE [App::DocumentObjectGroupPython] G4_Au  # scripted group (container) (typed FeaturePython)
  Dunit = g/cm3
  Dvalue = 19.32
  Group = -> [Au_element001]
  conduct = 2
  density = 1
  expand = 3
  formula = Au
  name = G4_Au
  specific = 4
FEATURE [App::DocumentObjectGroupPython] Hg_element002  label="Hg_element : 002"  # scripted group (container) (typed FeaturePython)
  n = 1
  ref = Hg_element
FEATURE [App::DocumentObjectGroupPython] G4_Hg  # scripted group (container) (typed FeaturePython)
  Dunit = g/cm3
  Dvalue = 13.546
  Group = -> [Hg_element002]
  conduct = 2
  density = 1
  expand = 3
  formula = Hg
  name = G4_Hg
  specific = 4
FEATURE [App::DocumentObjectGroupPython] Tl_element002  label="Tl_element : 002"  # scripted group (container) (typed FeaturePython)
  n = 1
  ref = Tl_element
FEATURE [App::DocumentObjectGroupPython] G4_Tl  # scripted group (container) (typed FeaturePython)
  Dunit = g/cm3
  Dvalue = 11.72
  Group = -> [Tl_element002]
  conduct = 2
  density = 1
  expand = 3
  formula = Tl
  name = G4_Tl
  specific = 4
FEATURE [App::DocumentObjectGroupPython] Pb_element003  label="Pb_element : 1"  # scripted group (container) (typed FeaturePython)
  n = 1
  ref = Pb_element
FEATURE [App::DocumentObjectGroupPython] G4_Pb  # scripted group (container) (typed FeaturePython)
  Dunit = g/cm3
  Dvalue = 11.35
  Group = -> [Pb_element003]
  conduct = 2
  density = 1
  expand = 3
  formula = Pb
  name = G4_Pb
  specific = 4
FEATURE [App::DocumentObjectGroupPython] Bi_element002  label="Bi_element : 1"  # scripted group (container) (typed FeaturePython)
  n = 1
  ref = Bi_element
FEATURE [App::DocumentObjectGroupPython] G4_Bi  # scripted group (container) (typed FeaturePython)
  Dunit = g/cm3
  Dvalue = 9.747
  Group = -> [Bi_element002]
  conduct = 2
  density = 1
  expand = 3
  formula = Bi
  name = G4_Bi
  specific = 4
FEATURE [App::DocumentObjectGroupPython] Po_element001  label="Po_element : 1"  # scripted group (container) (typed FeaturePython)
  n = 1
  ref = Po_element
FEATURE [App::DocumentObjectGroupPython] G4_Po  # scripted group (container) (typed FeaturePython)
  Dunit = g/cm3
  Dvalue = 9.32
  Group = -> [Po_element001]
  conduct = 2
  density = 1
  expand = 3
  formula = Po
  name = G4_Po
  specific = 4
FEATURE [App::DocumentObjectGroupPython] At_element001  label="At_element : 1"  # scripted group (container) (typed FeaturePython)
  n = 1
  ref = At_element
FEATURE [App::DocumentObjectGroupPython] G4_At  # scripted group (container) (typed FeaturePython)
  Dunit = g/cm3
  Dvalue = 9.32
  Group = -> [At_element001]
  conduct = 2
  density = 1
  expand = 3
  formula = At
  name = G4_At
  specific = 4
FEATURE [App::DocumentObjectGroupPython] Rn_element001  label="Rn_element : 1"  # scripted group (container) (typed FeaturePython)
  n = 1
  ref = Rn_element
FEATURE [App::DocumentObjectGroupPython] G4_Rn  # scripted group (container) (typed FeaturePython)
  Dunit = g/cm3
  Dvalue = 0.00900662
  Group = -> [Rn_element001]
  conduct = 2
  density = 1
  expand = 3
  formula = Rn
  name = G4_Rn
  specific = 4
FEATURE [App::DocumentObjectGroupPython] Fr_element001  label="Fr_element : 1"  # scripted group (container) (typed FeaturePython)
  n = 1
  ref = Fr_element
FEATURE [App::DocumentObjectGroupPython] G4_Fr  # scripted group (container) (typed FeaturePython)
  Dunit = g/cm3
  Dvalue = 1
  Group = -> [Fr_element001]
  conduct = 2
  density = 1
  expand = 3
  formula = Fr
  name = G4_Fr
  specific = 4
FEATURE [App::DocumentObjectGroupPython] Ra_element001  label="Ra_element : 1"  # scripted group (container) (typed FeaturePython)
  n = 1
  ref = Ra_element
FEATURE [App::DocumentObjectGroupPython] G4_Ra  # scripted group (container) (typed FeaturePython)
  Dunit = g/cm3
  Dvalue = 5
  Group = -> [Ra_element001]
  conduct = 2
  density = 1
  expand = 3
  formula = Ra
  name = G4_Ra
  specific = 4
FEATURE [App::DocumentObjectGroupPython] Ac_element001  label="Ac_element : 1"  # scripted group (container) (typed FeaturePython)
  n = 1
  ref = Ac_element
FEATURE [App::DocumentObjectGroupPython] G4_Ac  # scripted group (container) (typed FeaturePython)
  Dunit = g/cm3
  Dvalue = 10.07
  Group = -> [Ac_element001]
  conduct = 2
  density = 1
  expand = 3
  formula = Ac
  name = G4_Ac
  specific = 4
FEATURE [App::DocumentObjectGroupPython] Th_element001  label="Th_element : 1"  # scripted group (container) (typed FeaturePython)
  n = 1
  ref = Th_element
FEATURE [App::DocumentObjectGroupPython] G4_Th  # scripted group (container) (typed FeaturePython)
  Dunit = g/cm3
  Dvalue = 11.72
  Group = -> [Th_element001]
  conduct = 2
  density = 1
  expand = 3
  formula = Th
  name = G4_Th
  specific = 4
FEATURE [App::DocumentObjectGroupPython] Pa_element001  label="Pa_element : 1"  # scripted group (container) (typed FeaturePython)
  n = 1
  ref = Pa_element
FEATURE [App::DocumentObjectGroupPython] G4_Pa  # scripted group (container) (typed FeaturePython)
  Dunit = g/cm3
  Dvalue = 15.37
  Group = -> [Pa_element001]
  conduct = 2
  density = 1
  expand = 3
  formula = Pa
  name = G4_Pa
  specific = 4
FEATURE [App::DocumentObjectGroupPython] U_element004  label="U_element : 004"  # scripted group (container) (typed FeaturePython)
  n = 1
  ref = U_element
FEATURE [App::DocumentObjectGroupPython] G4_U  # scripted group (container) (typed FeaturePython)
  Dunit = g/cm3
  Dvalue = 18.95
  Group = -> [U_element004]
  conduct = 2
  density = 1
  expand = 3
  formula = U
  name = G4_U
  specific = 4
FEATURE [App::DocumentObjectGroupPython] Np_element001  label="Np_element : 1"  # scripted group (container) (typed FeaturePython)
  n = 1
  ref = Np_element
FEATURE [App::DocumentObjectGroupPython] G4_Np  # scripted group (container) (typed FeaturePython)
  Dunit = g/cm3
  Dvalue = 20.25
  Group = -> [Np_element001]
  conduct = 2
  density = 1
  expand = 3
  formula = Np
  name = G4_Np
  specific = 4
FEATURE [App::DocumentObjectGroupPython] Pu_element002  label="Pu_element : 002"  # scripted group (container) (typed FeaturePython)
  n = 1
  ref = Pu_element
FEATURE [App::DocumentObjectGroupPython] G4_Pu  # scripted group (container) (typed FeaturePython)
  Dunit = g/cm3
  Dvalue = 19.84
  Group = -> [Pu_element002]
  conduct = 2
  density = 1
  expand = 3
  formula = Pu
  name = G4_Pu
  specific = 4
FEATURE [App::DocumentObjectGroupPython] Am_element001  label="Am_element : 1"  # scripted group (container) (typed FeaturePython)
  n = 1
  ref = Am_element
FEATURE [App::DocumentObjectGroupPython] G4_Am  # scripted group (container) (typed FeaturePython)
  Dunit = g/cm3
  Dvalue = 13.67
  Group = -> [Am_element001]
  conduct = 2
  density = 1
  expand = 3
  formula = Am
  name = G4_Am
  specific = 4
FEATURE [App::DocumentObjectGroupPython] Cm_element001  label="Cm_element : 1"  # scripted group (container) (typed FeaturePython)
  n = 1
  ref = Cm_element
FEATURE [App::DocumentObjectGroupPython] G4_Cm  # scripted group (container) (typed FeaturePython)
  Dunit = g/cm3
  Dvalue = 13.51
  Group = -> [Cm_element001]
  conduct = 2
  density = 1
  expand = 3
  formula = Cm
  name = G4_Cm
  specific = 4
FEATURE [App::DocumentObjectGroupPython] Bk_element001  label="Bk_element : 1"  # scripted group (container) (typed FeaturePython)
  n = 1
  ref = Bk_element
FEATURE [App::DocumentObjectGroupPython] G4_Bk  # scripted group (container) (typed FeaturePython)
  Dunit = g/cm3
  Dvalue = 14
  Group = -> [Bk_element001]
  conduct = 2
  density = 1
  expand = 3
  formula = Bk
  name = G4_Bk
  specific = 4
FEATURE [App::DocumentObjectGroupPython] Cf_element001  label="Cf_element : 1"  # scripted group (container) (typed FeaturePython)
  n = 1
  ref = Cf_element
FEATURE [App::DocumentObjectGroupPython] G4_Cf  # scripted group (container) (typed FeaturePython)
  Dunit = g/cm3
  Dvalue = 10
  Group = -> [Cf_element001]
  conduct = 2
  density = 1
  expand = 3
  formula = Cf
  name = G4_Cf
  specific = 4
FEATURE [App::DocumentObjectGroupPython] Element  # scripted group (container) (typed FeaturePython)
  Group = -> [G4_H,G4_He,G4_Li,G4_Be,G4_B,G4_C,G4_N,G4_O,G4_F,G4_Ne,G4_Na,G4_Mg,G4_Al,G4_Si,G4_P,G4_S,G4_Cl,G4_Ar,G4_K,G4_Ca,G4_Sc,G4_Ti,G4_V,G4_Cr,G4_Mn,G4_Fe,G4_Co,G4_Ni,G4_Cu,G4_Zn,G4_Ga,G4_Ge,G4_As,G4_Se,G4_Br,G4_Kr,G4_Rb,G4_Sr,G4_Y,G4_Zr,G4_Nb,G4_Mo,G4_Tc,G4_Ru,G4_Rh,G4_Pd,G4_Ag,G4_Cd,G4_In,G4_Sn,G4_Sb,G4_Te,G4_I,G4_Xe,G4_Cs,G4_Ba,G4_La,G4_Ce,G4_Pr,G4_Nd,G4_Pm,G4_Sm,G4_Eu,G4_Gd,G4_Tb,G4_Dy,G4_Ho,G4_Er,+30 more]
FEATURE [App::DocumentObjectGroupPython] H_element114  label="H_element : 063"  # scripted group (container) (typed FeaturePython)
  n = 2
  ref = H_element
FEATURE [App::DocumentObjectGroupPython] G4_lH2  # scripted group (container) (typed FeaturePython)
  Dunit = g/cm3
  Dvalue = 0.0708
  Group = -> [H_element114]
  conduct = 2
  density = 1
  expand = 3
  formula = G4_lH2
  name = G4_lH2
  specific = 4
FEATURE [App::DocumentObjectGroupPython] N_element049  label="N_element : 022"  # scripted group (container) (typed FeaturePython)
  n = 2
  ref = N_element
FEATURE [App::DocumentObjectGroupPython] G4_lN2  # scripted group (container) (typed FeaturePython)
  Dunit = g/cm3
  Dvalue = 0.807
  Group = -> [N_element049]
  conduct = 2
  density = 1
  expand = 3
  formula = G4_lN2
  name = G4_lN2
  specific = 4
FEATURE [App::DocumentObjectGroupPython] O_element106  label="O_element : 060"  # scripted group (container) (typed FeaturePython)
  n = 2
  ref = O_element
FEATURE [App::DocumentObjectGroupPython] G4_lO2  # scripted group (container) (typed FeaturePython)
  Dunit = g/cm3
  Dvalue = 1.141
  Group = -> [O_element106]
  conduct = 2
  density = 1
  expand = 3
  formula = G4_lO2
  name = G4_lO2
  specific = 4
FEATURE [App::DocumentObjectGroupPython] Ar_element003  label="Ar_element : 002"  # scripted group (container) (typed FeaturePython)
  n = 1
  ref = Ar_element
FEATURE [App::DocumentObjectGroupPython] G4_lAr  # scripted group (container) (typed FeaturePython)
  Dunit = g/cm3
  Dvalue = 1.396
  Group = -> [Ar_element003]
  conduct = 2
  density = 1
  expand = 3
  formula = G4_lAr
  name = G4_lAr
  specific = 4
FEATURE [App::DocumentObjectGroupPython] Br_element008  label="Br_element : 005"  # scripted group (container) (typed FeaturePython)
  n = 1
  ref = Br_element
FEATURE [App::DocumentObjectGroupPython] G4_lBr  # scripted group (container) (typed FeaturePython)
  Dunit = g/cm3
  Dvalue = 3.1028
  Group = -> [Br_element008]
  conduct = 2
  density = 1
  expand = 3
  formula = G4_lBr
  name = G4_lBr
  specific = 4
FEATURE [App::DocumentObjectGroupPython] Kr_element002  label="Kr_element : 002"  # scripted group (container) (typed FeaturePython)
  n = 1
  ref = Kr_element
FEATURE [App::DocumentObjectGroupPython] G4_lKr  # scripted group (container) (typed FeaturePython)
  Dunit = g/cm3
  Dvalue = 2.418
  Group = -> [Kr_element002]
  conduct = 2
  density = 1
  expand = 3
  formula = G4_lKr
  name = G4_lKr
  specific = 4
FEATURE [App::DocumentObjectGroupPython] Xe_element002  label="Xe_element : 002"  # scripted group (container) (typed FeaturePython)
  n = 1
  ref = Xe_element
FEATURE [App::DocumentObjectGroupPython] G4_lXe  # scripted group (container) (typed FeaturePython)
  Dunit = g/cm3
  Dvalue = 2.953
  Group = -> [Xe_element002]
  conduct = 2
  density = 1
  expand = 3
  formula = G4_lXe
  name = G4_lXe
  specific = 4
FEATURE [App::DocumentObjectGroupPython] O_element107  label="O_element : 061"  # scripted group (container) (typed FeaturePython)
  n = 4
  ref = O_element
FEATURE [App::DocumentObjectGroupPython] Pb_element004  label="Pb_element : 002"  # scripted group (container) (typed FeaturePython)
  n = 1
  ref = Pb_element
FEATURE [App::DocumentObjectGroupPython] W_element005  label="W_element : 005"  # scripted group (container) (typed FeaturePython)
  n = 1
  ref = W_element
FEATURE [App::DocumentObjectGroupPython] G4_PbWO4  # scripted group (container) (typed FeaturePython)
  Dunit = g/cm3
  Dvalue = 8.28
  Group = -> [O_element107,Pb_element004,W_element005]
  conduct = 2
  density = 1
  expand = 3
  formula = G4_PbWO4
  name = G4_PbWO4
  specific = 4
FEATURE [App::DocumentObjectGroupPython] H_element115  label="H_element : 064"  # scripted group (container) (typed FeaturePython)
  n = 1
  ref = H_element
FEATURE [App::DocumentObjectGroupPython] G4_Galactic  # scripted group (container) (typed FeaturePython)
  Dunit = g/cm3
  Dvalue = 0
  Group = -> [H_element115]
  conduct = 2
  density = 1
  expand = 3
  formula = G4_Galactic
  name = G4_Galactic
  specific = 4
FEATURE [App::DocumentObjectGroupPython] C_element125  label="C_element : 071"  # scripted group (container) (typed FeaturePython)
  n = 1
  ref = C_element
FEATURE [App::DocumentObjectGroupPython] G4_GRAPHITE_POROUS  # scripted group (container) (typed FeaturePython)
  Dunit = g/cm3
  Dvalue = 1.7
  Group = -> [C_element125]
  conduct = 2
  density = 1
  expand = 3
  formula = G4_GRAPHITE_POROUS
  name = G4_GRAPHITE_POROUS
  specific = 4
FEATURE [App::DocumentObjectGroupPython] H_element116  label="H_element : 0.150"  # scripted group (container) (typed FeaturePython)
  n = 0.080538
FEATURE [App::DocumentObjectGroupPython] C_element126  label="C_element : 0.600"  # scripted group (container) (typed FeaturePython)
  n = 0.599848
FEATURE [App::DocumentObjectGroupPython] O_element108  label="O_element : 0.320"  # scripted group (container) (typed FeaturePython)
  n = 0.319614
FEATURE [App::DocumentObjectGroupPython] G4_LUCITE  # scripted group (container) (typed FeaturePython)
  Dunit = g/cm3
  Dvalue = 1.19
  Group = -> [H_element116,C_element126,O_element108]
  conduct = 2
  density = 1
  expand = 3
  formula = G4_LUCITE
  name = G4_LUCITE
  specific = 4
FEATURE [App::DocumentObjectGroupPython] Cu_element002  label="Cu_element : 62"  # scripted group (container) (typed FeaturePython)
  n = 62
  ref = Cu_element
FEATURE [App::DocumentObjectGroupPython] Zn_element002  label="Zn_element : 35"  # scripted group (container) (typed FeaturePython)
  n = 35
  ref = Zn_element
FEATURE [App::DocumentObjectGroupPython] Pb_element005  label="Pb_element : 3"  # scripted group (container) (typed FeaturePython)
  n = 3
  ref = Pb_element
FEATURE [App::DocumentObjectGroupPython] G4_BRASS  # scripted group (container) (typed FeaturePython)
  Dunit = g/cm3
  Dvalue = 8.52
  Group = -> [Cu_element002,Zn_element002,Pb_element005]
  conduct = 2
  density = 1
  expand = 3
  formula = G4_BRASS
  name = G4_BRASS
  specific = 4
FEATURE [App::DocumentObjectGroupPython] Cu_element003  label="Cu_element : 89"  # scripted group (container) (typed FeaturePython)
  n = 89
  ref = Cu_element
FEATURE [App::DocumentObjectGroupPython] Zn_element003  label="Zn_element : 9"  # scripted group (container) (typed FeaturePython)
  n = 9
  ref = Zn_element
FEATURE [App::DocumentObjectGroupPython] Pb_element006  label="Pb_element : 2"  # scripted group (container) (typed FeaturePython)
  n = 2
  ref = Pb_element
FEATURE [App::DocumentObjectGroupPython] G4_BRONZE  # scripted group (container) (typed FeaturePython)
  Dunit = g/cm3
  Dvalue = 8.82
  Group = -> [Cu_element003,Zn_element003,Pb_element006]
  conduct = 2
  density = 1
  expand = 3
  formula = G4_BRONZE
  name = G4_BRONZE
  specific = 4
FEATURE [App::DocumentObjectGroupPython] Fe_element008  label="Fe_element : 74"  # scripted group (container) (typed FeaturePython)
  n = 74
  ref = Fe_element
FEATURE [App::DocumentObjectGroupPython] Cr_element002  label="Cr_element : 18"  # scripted group (container) (typed FeaturePython)
  n = 18
  ref = Cr_element
FEATURE [App::DocumentObjectGroupPython] Ni_element002  label="Ni_element : 8"  # scripted group (container) (typed FeaturePython)
  n = 8
  ref = Ni_element
FEATURE [App::DocumentObjectGroupPython] G4_STAINLESS_STEEL  label="G4_STAINLESS-STEEL"  # scripted group (container) (typed FeaturePython)
  Dunit = g/cm3
  Dvalue = 8
  Group = -> [Fe_element008,Cr_element002,Ni_element002]
  conduct = 2
  density = 1
  expand = 3
  formula = G4_STAINLESS-STEEL
  name = G4_STAINLESS-STEEL
  specific = 4
FEATURE [App::DocumentObjectGroupPython] H_element117  label="H_element : 065"  # scripted group (container) (typed FeaturePython)
  n = 18
  ref = H_element
FEATURE [App::DocumentObjectGroupPython] C_element127  label="C_element : 072"  # scripted group (container) (typed FeaturePython)
  n = 12
  ref = C_element
FEATURE [App::DocumentObjectGroupPython] O_element109  label="O_element : 062"  # scripted group (container) (typed FeaturePython)
  n = 7
  ref = O_element
FEATURE [App::DocumentObjectGroupPython] G4_CR39  # scripted group (container) (typed FeaturePython)
  Dunit = g/cm3
  Dvalue = 1.32
  Group = -> [H_element117,C_element127,O_element109]
  conduct = 2
  density = 1
  expand = 3
  formula = G4_CR39
  name = G4_CR39
  specific = 4
FEATURE [App::DocumentObjectGroupPython] H_element118  label="H_element : 38"  # scripted group (container) (typed FeaturePython)
  n = 38
  ref = H_element
FEATURE [App::DocumentObjectGroupPython] C_element128  label="C_element : 073"  # scripted group (container) (typed FeaturePython)
  n = 18
  ref = C_element
FEATURE [App::DocumentObjectGroupPython] O_element110  label="O_element : 063"  # scripted group (container) (typed FeaturePython)
  n = 1
  ref = O_element
FEATURE [App::DocumentObjectGroupPython] G4_OCTADECANOL  # scripted group (container) (typed FeaturePython)
  Dunit = g/cm3
  Dvalue = 0.812
  Group = -> [H_element118,C_element128,O_element110]
  conduct = 2
  density = 1
  expand = 3
  formula = G4_OCTADECANOL
  name = G4_OCTADECANOL
  specific = 4
FEATURE [App::DocumentObjectGroupPython] HEP  # scripted group (container) (typed FeaturePython)
  Group = -> [G4_lH2,G4_lN2,G4_lO2,G4_lAr,G4_lBr,G4_lKr,G4_lXe,G4_PbWO4,G4_Galactic,G4_GRAPHITE_POROUS,G4_LUCITE,G4_BRASS,G4_BRONZE,G4_STAINLESS_STEEL,G4_CR39,G4_OCTADECANOL]
FEATURE [App::DocumentObjectGroupPython] C_element129  label="C_element : 074"  # scripted group (container) (typed FeaturePython)
  n = 14
  ref = C_element
FEATURE [App::DocumentObjectGroupPython] H_element119  label="H_element : 066"  # scripted group (container) (typed FeaturePython)
  n = 10
  ref = H_element
FEATURE [App::DocumentObjectGroupPython] O_element111  label="O_element : 064"  # scripted group (container) (typed FeaturePython)
  n = 2
  ref = O_element
FEATURE [App::DocumentObjectGroupPython] N_element050  label="N_element : 023"  # scripted group (container) (typed FeaturePython)
  n = 2
  ref = N_element
FEATURE [App::DocumentObjectGroupPython] G4_KEVLAR  # scripted group (container) (typed FeaturePython)
  Dunit = g/cm3
  Dvalue = 1.44
  Group = -> [C_element129,H_element119,O_element111,N_element050]
  conduct = 2
  density = 1
  expand = 3
  formula = G4_KEVLAR
  name = G4_KEVLAR
  specific = 4
FEATURE [App::DocumentObjectGroupPython] C_element130  label="C_element : 075"  # scripted group (container) (typed FeaturePython)
  n = 10
  ref = C_element
FEATURE [App::DocumentObjectGroupPython] H_element120  label="H_element : 067"  # scripted group (container) (typed FeaturePython)
  n = 8
  ref = H_element
FEATURE [App::DocumentObjectGroupPython] O_element112  label="O_element : 065"  # scripted group (container) (typed FeaturePython)
  n = 4
  ref = O_element
FEATURE [App::DocumentObjectGroupPython] G4_DACRON  # scripted group (container) (typed FeaturePython)
  Dunit = g/cm3
  Dvalue = 1.4
  Group = -> [C_element130,H_element120,O_element112]
  conduct = 2
  density = 1
  expand = 3
  formula = G4_DACRON
  name = G4_DACRON
  specific = 4
FEATURE [App::DocumentObjectGroupPython] C_element131  label="C_element : 076"  # scripted group (container) (typed FeaturePython)
  n = 4
  ref = C_element
FEATURE [App::DocumentObjectGroupPython] H_element121  label="H_element : 068"  # scripted group (container) (typed FeaturePython)
  n = 5
  ref = H_element
FEATURE [App::DocumentObjectGroupPython] Cl_element030  label="Cl_element : 016"  # scripted group (container) (typed FeaturePython)
  n = 1
  ref = Cl_element
FEATURE [App::DocumentObjectGroupPython] G4_NEOPRENE  # scripted group (container) (typed FeaturePython)
  Dunit = g/cm3
  Dvalue = 1.23
  Group = -> [C_element131,H_element121,Cl_element030]
  conduct = 2
  density = 1
  expand = 3
  formula = G4_NEOPRENE
  name = G4_NEOPRENE
  specific = 4
FEATURE [App::DocumentObjectGroupPython] Space  # scripted group (container) (typed FeaturePython)
  Group = -> [G4_KEVLAR,G4_DACRON,G4_NEOPRENE]
FEATURE [App::DocumentObjectGroupPython] H_element122  label="H_element : 069"  # scripted group (container) (typed FeaturePython)
  n = 5
  ref = H_element
FEATURE [App::DocumentObjectGroupPython] C_element132  label="C_element : 077"  # scripted group (container) (typed FeaturePython)
  n = 4
  ref = C_element
FEATURE [App::DocumentObjectGroupPython] N_element051  label="N_element : 3"  # scripted group (container) (typed FeaturePython)
  n = 3
  ref = N_element
FEATURE [App::DocumentObjectGroupPython] O_element113  label="O_element : 066"  # scripted group (container) (typed FeaturePython)
  n = 1
  ref = O_element
FEATURE [App::DocumentObjectGroupPython] G4_CYTOSINE  # scripted group (container) (typed FeaturePython)
  Dunit = g/cm3
  Dvalue = 1.55
  Group = -> [H_element122,C_element132,N_element051,O_element113]
  conduct = 2
  density = 1
  expand = 3
  formula = G4_CYTOSINE
  name = G4_CYTOSINE
  specific = 4
FEATURE [App::DocumentObjectGroupPython] H_element123  label="H_element : 070"  # scripted group (container) (typed FeaturePython)
  n = 6
  ref = H_element
FEATURE [App::DocumentObjectGroupPython] C_element133  label="C_element : 078"  # scripted group (container) (typed FeaturePython)
  n = 5
  ref = C_element
FEATURE [App::DocumentObjectGroupPython] N_element052  label="N_element : 024"  # scripted group (container) (typed FeaturePython)
  n = 2
  ref = N_element
FEATURE [App::DocumentObjectGroupPython] O_element114  label="O_element : 067"  # scripted group (container) (typed FeaturePython)
  n = 2
  ref = O_element
FEATURE [App::DocumentObjectGroupPython] G4_THYMINE  # scripted group (container) (typed FeaturePython)
  Dunit = g/cm3
  Dvalue = 1.23
  Group = -> [H_element123,C_element133,N_element052,O_element114]
  conduct = 2
  density = 1
  expand = 3
  formula = G4_THYMINE
  name = G4_THYMINE
  specific = 4
FEATURE [App::DocumentObjectGroupPython] H_element124  label="H_element : 071"  # scripted group (container) (typed FeaturePython)
  n = 4
  ref = H_element
FEATURE [App::DocumentObjectGroupPython] C_element134  label="C_element : 079"  # scripted group (container) (typed FeaturePython)
  n = 4
  ref = C_element
FEATURE [App::DocumentObjectGroupPython] N_element053  label="N_element : 025"  # scripted group (container) (typed FeaturePython)
  n = 2
  ref = N_element
FEATURE [App::DocumentObjectGroupPython] O_element115  label="O_element : 068"  # scripted group (container) (typed FeaturePython)
  n = 2
  ref = O_element
FEATURE [App::DocumentObjectGroupPython] G4_URACIL  # scripted group (container) (typed FeaturePython)
  Dunit = g/cm3
  Dvalue = 1.32
  Group = -> [H_element124,C_element134,N_element053,O_element115]
  conduct = 2
  density = 1
  expand = 3
  formula = G4_URACIL
  name = G4_URACIL
  specific = 4
FEATURE [App::DocumentObjectGroupPython] H_element125  label="H_element : 072"  # scripted group (container) (typed FeaturePython)
  n = 4
  ref = H_element
FEATURE [App::DocumentObjectGroupPython] C_element135  label="C_element : 080"  # scripted group (container) (typed FeaturePython)
  n = 5
  ref = C_element
FEATURE [App::DocumentObjectGroupPython] N_element054  label="N_element : 026"  # scripted group (container) (typed FeaturePython)
  n = 5
  ref = N_element
FEATURE [App::DocumentObjectGroupPython] G4_DNA_ADENINE  # scripted group (container) (typed FeaturePython)
  Dunit = g/cm3
  Dvalue = 1
  Group = -> [H_element125,C_element135,N_element054]
  conduct = 2
  density = 1
  expand = 3
  formula = G4_DNA_ADENINE
  name = G4_DNA_ADENINE
  specific = 4
FEATURE [App::DocumentObjectGroupPython] H_element126  label="H_element : 073"  # scripted group (container) (typed FeaturePython)
  n = 4
  ref = H_element
FEATURE [App::DocumentObjectGroupPython] C_element136  label="C_element : 081"  # scripted group (container) (typed FeaturePython)
  n = 5
  ref = C_element
FEATURE [App::DocumentObjectGroupPython] N_element055  label="N_element : 027"  # scripted group (container) (typed FeaturePython)
  n = 5
  ref = N_element
FEATURE [App::DocumentObjectGroupPython] O_element116  label="O_element : 069"  # scripted group (container) (typed FeaturePython)
  n = 1
  ref = O_element
FEATURE [App::DocumentObjectGroupPython] G4_DNA_GUANINE  # scripted group (container) (typed FeaturePython)
  Dunit = g/cm3
  Dvalue = 1
  Group = -> [H_element126,C_element136,N_element055,O_element116]
  conduct = 2
  density = 1
  expand = 3
  formula = G4_DNA_GUANINE
  name = G4_DNA_GUANINE
  specific = 4
FEATURE [App::DocumentObjectGroupPython] H_element127  label="H_element : 074"  # scripted group (container) (typed FeaturePython)
  n = 4
  ref = H_element
FEATURE [App::DocumentObjectGroupPython] C_element137  label="C_element : 082"  # scripted group (container) (typed FeaturePython)
  n = 4
  ref = C_element
FEATURE [App::DocumentObjectGroupPython] N_element056  label="N_element : 028"  # scripted group (container) (typed FeaturePython)
  n = 3
  ref = N_element
FEATURE [App::DocumentObjectGroupPython] O_element117  label="O_element : 070"  # scripted group (container) (typed FeaturePython)
  n = 1
  ref = O_element
FEATURE [App::DocumentObjectGroupPython] G4_DNA_CYTOSINE  # scripted group (container) (typed FeaturePython)
  Dunit = g/cm3
  Dvalue = 1
  Group = -> [H_element127,C_element137,N_element056,O_element117]
  conduct = 2
  density = 1
  expand = 3
  formula = G4_DNA_CYTOSINE
  name = G4_DNA_CYTOSINE
  specific = 4
FEATURE [App::DocumentObjectGroupPython] H_element128  label="H_element : 075"  # scripted group (container) (typed FeaturePython)
  n = 5
  ref = H_element
FEATURE [App::DocumentObjectGroupPython] C_element138  label="C_element : 083"  # scripted group (container) (typed FeaturePython)
  n = 5
  ref = C_element
FEATURE [App::DocumentObjectGroupPython] N_element057  label="N_element : 029"  # scripted group (container) (typed FeaturePython)
  n = 2
  ref = N_element
FEATURE [App::DocumentObjectGroupPython] O_element118  label="O_element : 071"  # scripted group (container) (typed FeaturePython)
  n = 2
  ref = O_element
FEATURE [App::DocumentObjectGroupPython] G4_DNA_THYMINE  # scripted group (container) (typed FeaturePython)
  Dunit = g/cm3
  Dvalue = 1
  Group = -> [H_element128,C_element138,N_element057,O_element118]
  conduct = 2
  density = 1
  expand = 3
  formula = G4_DNA_THYMINE
  name = G4_DNA_THYMINE
  specific = 4
FEATURE [App::DocumentObjectGroupPython] H_element129  label="H_element : 076"  # scripted group (container) (typed FeaturePython)
  n = 3
  ref = H_element
FEATURE [App::DocumentObjectGroupPython] C_element139  label="C_element : 084"  # scripted group (container) (typed FeaturePython)
  n = 4
  ref = C_element
FEATURE [App::DocumentObjectGroupPython] N_element058  label="N_element : 030"  # scripted group (container) (typed FeaturePython)
  n = 2
  ref = N_element
FEATURE [App::DocumentObjectGroupPython] O_element119  label="O_element : 072"  # scripted group (container) (typed FeaturePython)
  n = 2
  ref = O_element
FEATURE [App::DocumentObjectGroupPython] G4_DNA_URACIL  # scripted group (container) (typed FeaturePython)
  Dunit = g/cm3
  Dvalue = 1
  Group = -> [H_element129,C_element139,N_element058,O_element119]
  conduct = 2
  density = 1
  expand = 3
  formula = G4_DNA_URACIL
  name = G4_DNA_URACIL
  specific = 4
FEATURE [App::DocumentObjectGroupPython] H_element130  label="H_element : 077"  # scripted group (container) (typed FeaturePython)
  n = 10
  ref = H_element
FEATURE [App::DocumentObjectGroupPython] C_element140  label="C_element : 085"  # scripted group (container) (typed FeaturePython)
  n = 10
  ref = C_element
FEATURE [App::DocumentObjectGroupPython] N_element059  label="N_element : 031"  # scripted group (container) (typed FeaturePython)
  n = 5
  ref = N_element
FEATURE [App::DocumentObjectGroupPython] O_element120  label="O_element : 073"  # scripted group (container) (typed FeaturePython)
  n = 4
  ref = O_element
FEATURE [App::DocumentObjectGroupPython] G4_DNA_ADENOSINE  # scripted group (container) (typed FeaturePython)
  Dunit = g/cm3
  Dvalue = 1
  Group = -> [H_element130,C_element140,N_element059,O_element120]
  conduct = 2
  density = 1
  expand = 3
  formula = G4_DNA_ADENOSINE
  name = G4_DNA_ADENOSINE
  specific = 4
FEATURE [App::DocumentObjectGroupPython] H_element131  label="H_element : 078"  # scripted group (container) (typed FeaturePython)
  n = 10
  ref = H_element
FEATURE [App::DocumentObjectGroupPython] C_element141  label="C_element : 086"  # scripted group (container) (typed FeaturePython)
  n = 10
  ref = C_element
FEATURE [App::DocumentObjectGroupPython] N_element060  label="N_element : 032"  # scripted group (container) (typed FeaturePython)
  n = 5
  ref = N_element
FEATURE [App::DocumentObjectGroupPython] O_element121  label="O_element : 074"  # scripted group (container) (typed FeaturePython)
  n = 5
  ref = O_element
FEATURE [App::DocumentObjectGroupPython] G4_DNA_GUANOSINE  # scripted group (container) (typed FeaturePython)
  Dunit = g/cm3
  Dvalue = 1
  Group = -> [H_element131,C_element141,N_element060,O_element121]
  conduct = 2
  density = 1
  expand = 3
  formula = G4_DNA_GUANOSINE
  name = G4_DNA_GUANOSINE
  specific = 4
FEATURE [App::DocumentObjectGroupPython] H_element132  label="H_element : 079"  # scripted group (container) (typed FeaturePython)
  n = 10
  ref = H_element
FEATURE [App::DocumentObjectGroupPython] C_element142  label="C_element : 087"  # scripted group (container) (typed FeaturePython)
  n = 9
  ref = C_element
FEATURE [App::DocumentObjectGroupPython] N_element061  label="N_element : 033"  # scripted group (container) (typed FeaturePython)
  n = 3
  ref = N_element
FEATURE [App::DocumentObjectGroupPython] O_element122  label="O_element : 075"  # scripted group (container) (typed FeaturePython)
  n = 5
  ref = O_element
FEATURE [App::DocumentObjectGroupPython] G4_DNA_CYTIDINE  # scripted group (container) (typed FeaturePython)
  Dunit = g/cm3
  Dvalue = 1
  Group = -> [H_element132,C_element142,N_element061,O_element122]
  conduct = 2
  density = 1
  expand = 3
  formula = G4_DNA_CYTIDINE
  name = G4_DNA_CYTIDINE
  specific = 4
FEATURE [App::DocumentObjectGroupPython] H_element133  label="H_element : 080"  # scripted group (container) (typed FeaturePython)
  n = 9
  ref = H_element
FEATURE [App::DocumentObjectGroupPython] C_element143  label="C_element : 088"  # scripted group (container) (typed FeaturePython)
  n = 9
  ref = C_element
FEATURE [App::DocumentObjectGroupPython] N_element062  label="N_element : 034"  # scripted group (container) (typed FeaturePython)
  n = 2
  ref = N_element
FEATURE [App::DocumentObjectGroupPython] O_element123  label="O_element : 076"  # scripted group (container) (typed FeaturePython)
  n = 6
  ref = O_element
FEATURE [App::DocumentObjectGroupPython] G4_DNA_URIDINE  # scripted group (container) (typed FeaturePython)
  Dunit = g/cm3
  Dvalue = 1
  Group = -> [H_element133,C_element143,N_element062,O_element123]
  conduct = 2
  density = 1
  expand = 3
  formula = G4_DNA_URIDINE
  name = G4_DNA_URIDINE
  specific = 4
FEATURE [App::DocumentObjectGroupPython] H_element134  label="H_element : 081"  # scripted group (container) (typed FeaturePython)
  n = 11
  ref = H_element
FEATURE [App::DocumentObjectGroupPython] C_element144  label="C_element : 089"  # scripted group (container) (typed FeaturePython)
  n = 10
  ref = C_element
FEATURE [App::DocumentObjectGroupPython] N_element063  label="N_element : 035"  # scripted group (container) (typed FeaturePython)
  n = 2
  ref = N_element
FEATURE [App::DocumentObjectGroupPython] O_element124  label="O_element : 077"  # scripted group (container) (typed FeaturePython)
  n = 6
  ref = O_element
FEATURE [App::DocumentObjectGroupPython] G4_DNA_METHYLURIDINE  # scripted group (container) (typed FeaturePython)
  Dunit = g/cm3
  Dvalue = 1
  Group = -> [H_element134,C_element144,N_element063,O_element124]
  conduct = 2
  density = 1
  expand = 3
  formula = G4_DNA_METHYLURIDINE
  name = G4_DNA_METHYLURIDINE
  specific = 4
FEATURE [App::DocumentObjectGroupPython] P_element014  label="P_element : 003"  # scripted group (container) (typed FeaturePython)
  n = 1
  ref = P_element
FEATURE [App::DocumentObjectGroupPython] O_element125  label="O_element : 078"  # scripted group (container) (typed FeaturePython)
  n = 3
  ref = O_element
FEATURE [App::DocumentObjectGroupPython] G4_DNA_MONOPHOSPHATE  # scripted group (container) (typed FeaturePython)
  Dunit = g/cm3
  Dvalue = 1
  Group = -> [P_element014,O_element125]
  conduct = 2
  density = 1
  expand = 3
  formula = G4_DNA_MONOPHOSPHATE
  name = G4_DNA_MONOPHOSPHATE
  specific = 4
FEATURE [App::DocumentObjectGroupPython] H_element135  label="H_element : 082"  # scripted group (container) (typed FeaturePython)
  n = 10
  ref = H_element
FEATURE [App::DocumentObjectGroupPython] C_element145  label="C_element : 090"  # scripted group (container) (typed FeaturePython)
  n = 10
  ref = C_element
FEATURE [App::DocumentObjectGroupPython] N_element064  label="N_element : 036"  # scripted group (container) (typed FeaturePython)
  n = 5
  ref = N_element
FEATURE [App::DocumentObjectGroupPython] O_element126  label="O_element : 079"  # scripted group (container) (typed FeaturePython)
  n = 7
  ref = O_element
FEATURE [App::DocumentObjectGroupPython] P_element015  label="P_element : 004"  # scripted group (container) (typed FeaturePython)
  n = 1
  ref = P_element
FEATURE [App::DocumentObjectGroupPython] G4_DNA_A  # scripted group (container) (typed FeaturePython)
  Dunit = g/cm3
  Dvalue = 1
  Group = -> [H_element135,C_element145,N_element064,O_element126,P_element015]
  conduct = 2
  density = 1
  expand = 3
  formula = G4_DNA_A
  name = G4_DNA_A
  specific = 4
FEATURE [App::DocumentObjectGroupPython] H_element136  label="H_element : 083"  # scripted group (container) (typed FeaturePython)
  n = 10
  ref = H_element
FEATURE [App::DocumentObjectGroupPython] C_element146  label="C_element : 091"  # scripted group (container) (typed FeaturePython)
  n = 10
  ref = C_element
FEATURE [App::DocumentObjectGroupPython] N_element065  label="N_element : 037"  # scripted group (container) (typed FeaturePython)
  n = 5
  ref = N_element
FEATURE [App::DocumentObjectGroupPython] O_element127  label="O_element : 8"  # scripted group (container) (typed FeaturePython)
  n = 8
  ref = O_element
FEATURE [App::DocumentObjectGroupPython] P_element016  label="P_element : 005"  # scripted group (container) (typed FeaturePython)
  n = 1
  ref = P_element
FEATURE [App::DocumentObjectGroupPython] G4_DNA_G  # scripted group (container) (typed FeaturePython)
  Dunit = g/cm3
  Dvalue = 1
  Group = -> [H_element136,C_element146,N_element065,O_element127,P_element016]
  conduct = 2
  density = 1
  expand = 3
  formula = G4_DNA_G
  name = G4_DNA_G
  specific = 4
FEATURE [App::DocumentObjectGroupPython] H_element137  label="H_element : 084"  # scripted group (container) (typed FeaturePython)
  n = 10
  ref = H_element
FEATURE [App::DocumentObjectGroupPython] C_element147  label="C_element : 092"  # scripted group (container) (typed FeaturePython)
  n = 9
  ref = C_element
FEATURE [App::DocumentObjectGroupPython] N_element066  label="N_element : 038"  # scripted group (container) (typed FeaturePython)
  n = 3
  ref = N_element
FEATURE [App::DocumentObjectGroupPython] O_element128  label="O_element : 080"  # scripted group (container) (typed FeaturePython)
  n = 8
  ref = O_element
FEATURE [App::DocumentObjectGroupPython] P_element017  label="P_element : 006"  # scripted group (container) (typed FeaturePython)
  n = 1
  ref = P_element
FEATURE [App::DocumentObjectGroupPython] G4_DNA_C  # scripted group (container) (typed FeaturePython)
  Dunit = g/cm3
  Dvalue = 1
  Group = -> [H_element137,C_element147,N_element066,O_element128,P_element017]
  conduct = 2
  density = 1
  expand = 3
  formula = G4_DNA_C
  name = G4_DNA_C
  specific = 4
FEATURE [App::DocumentObjectGroupPython] H_element138  label="H_element : 085"  # scripted group (container) (typed FeaturePython)
  n = 9
  ref = H_element
FEATURE [App::DocumentObjectGroupPython] C_element148  label="C_element : 093"  # scripted group (container) (typed FeaturePython)
  n = 9
  ref = C_element
FEATURE [App::DocumentObjectGroupPython] N_element067  label="N_element : 039"  # scripted group (container) (typed FeaturePython)
  n = 2
  ref = N_element
FEATURE [App::DocumentObjectGroupPython] O_element129  label="O_element : 9"  # scripted group (container) (typed FeaturePython)
  n = 9
  ref = O_element
FEATURE [App::DocumentObjectGroupPython] P_element018  label="P_element : 007"  # scripted group (container) (typed FeaturePython)
  n = 1
  ref = P_element
FEATURE [App::DocumentObjectGroupPython] G4_DNA_U  # scripted group (container) (typed FeaturePython)
  Dunit = g/cm3
  Dvalue = 1
  Group = -> [H_element138,C_element148,N_element067,O_element129,P_element018]
  conduct = 2
  density = 1
  expand = 3
  formula = G4_DNA_U
  name = G4_DNA_U
  specific = 4
FEATURE [App::DocumentObjectGroupPython] H_element139  label="H_element : 086"  # scripted group (container) (typed FeaturePython)
  n = 11
  ref = H_element
FEATURE [App::DocumentObjectGroupPython] C_element149  label="C_element : 094"  # scripted group (container) (typed FeaturePython)
  n = 10
  ref = C_element
FEATURE [App::DocumentObjectGroupPython] N_element068  label="N_element : 040"  # scripted group (container) (typed FeaturePython)
  n = 2
  ref = N_element
FEATURE [App::DocumentObjectGroupPython] O_element130  label="O_element : 081"  # scripted group (container) (typed FeaturePython)
  n = 9
  ref = O_element
FEATURE [App::DocumentObjectGroupPython] P_element019  label="P_element : 008"  # scripted group (container) (typed FeaturePython)
  n = 1
  ref = P_element
FEATURE [App::DocumentObjectGroupPython] G4_DNA_MU  # scripted group (container) (typed FeaturePython)
  Dunit = g/cm3
  Dvalue = 1
  Group = -> [H_element139,C_element149,N_element068,O_element130,P_element019]
  conduct = 2
  density = 1
  expand = 3
  formula = G4_DNA_MU
  name = G4_DNA_MU
  specific = 4
FEATURE [App::DocumentObjectGroupPython] BioChemical  # scripted group (container) (typed FeaturePython)
  Group = -> [G4_CYTOSINE,G4_THYMINE,G4_URACIL,G4_DNA_ADENINE,G4_DNA_GUANINE,G4_DNA_CYTOSINE,G4_DNA_THYMINE,G4_DNA_URACIL,G4_DNA_ADENOSINE,G4_DNA_GUANOSINE,G4_DNA_CYTIDINE,G4_DNA_URIDINE,G4_DNA_METHYLURIDINE,G4_DNA_MONOPHOSPHATE,G4_DNA_A,G4_DNA_G,G4_DNA_C,G4_DNA_U,G4_DNA_MU]
FEATURE [App::DocumentObjectGroupPython] G4Materials  # scripted group (container) (typed FeaturePython)
  Group = -> [NIST,Element,HEP,Space,BioChemical]
  version = 1
FEATURE [App::DocumentObjectGroupPython] Geant4  # scripted group (container) (typed FeaturePython)
  Group = -> [G4Isotopes,G4Elements,G4Materials]
FEATURE [App::DocumentObjectGroupPython] Materials  # scripted group (container) (typed FeaturePython)
  Group = -> [Geant4]
FEATURE [Part::FeaturePython] GDMLBox_WorldBox  # WARN: FeaturePython — macro-defined, semantics opaque (R4)
  lunit = 2
  material = 5
  x = 145.922
  y = 145.922
  z = 130
FEATURE [Part::FeaturePython] GDMLBox_Box  # WARN: FeaturePython — macro-defined, semantics opaque (R4)
  lunit = 2
  material = 0
  x = 15
  y = 10
  z = 10
FEATURE [App::Part] LV_Box
  Group = -> [GDMLBox_Box]
  Origin = -> Origin001
  Placement = pos=(0,0,0) rot=(0,0,1;0.261799rad)
FEATURE [Part::FeaturePython] Array  # Draft array (typed FeaturePython)
  AlwaysSyncPlacement = false
  Angle = 360
  ArrayType = 0
  Axis = (0,0,1)
  Base = -> LV_Box
  Center = (0,0,0)
  Count = 4
  ExpandArray = false
  Fuse = false
  IntervalAxis = (0,0,0)
  IntervalX = (50,0,0)
  IntervalY = (0,50,0)
  IntervalZ = (0,0,100)
  NumberCircles = 3
  NumberPolar = 5
  NumberX = 2
  NumberY = 2
  NumberZ = 1
  PlacementList = 4 placements: [(0,0,0),(0,50,0),(50,0,0),(50,50,0)]
  RadialDistance = 50
  ScaleList = (4) [(1,1,1),(1,1,1),(1,1,1),(1,1,1)]
  Symmetry = 1
  TangentialDistance = 25
FEATURE [App::Part] Part
  Group = -> [LV_Box,Array]
  Origin = -> Origin002
FEATURE [App::Part] worldVOL
  Group = -> [GDMLBox_WorldBox,Part]
  Origin = -> Origin
